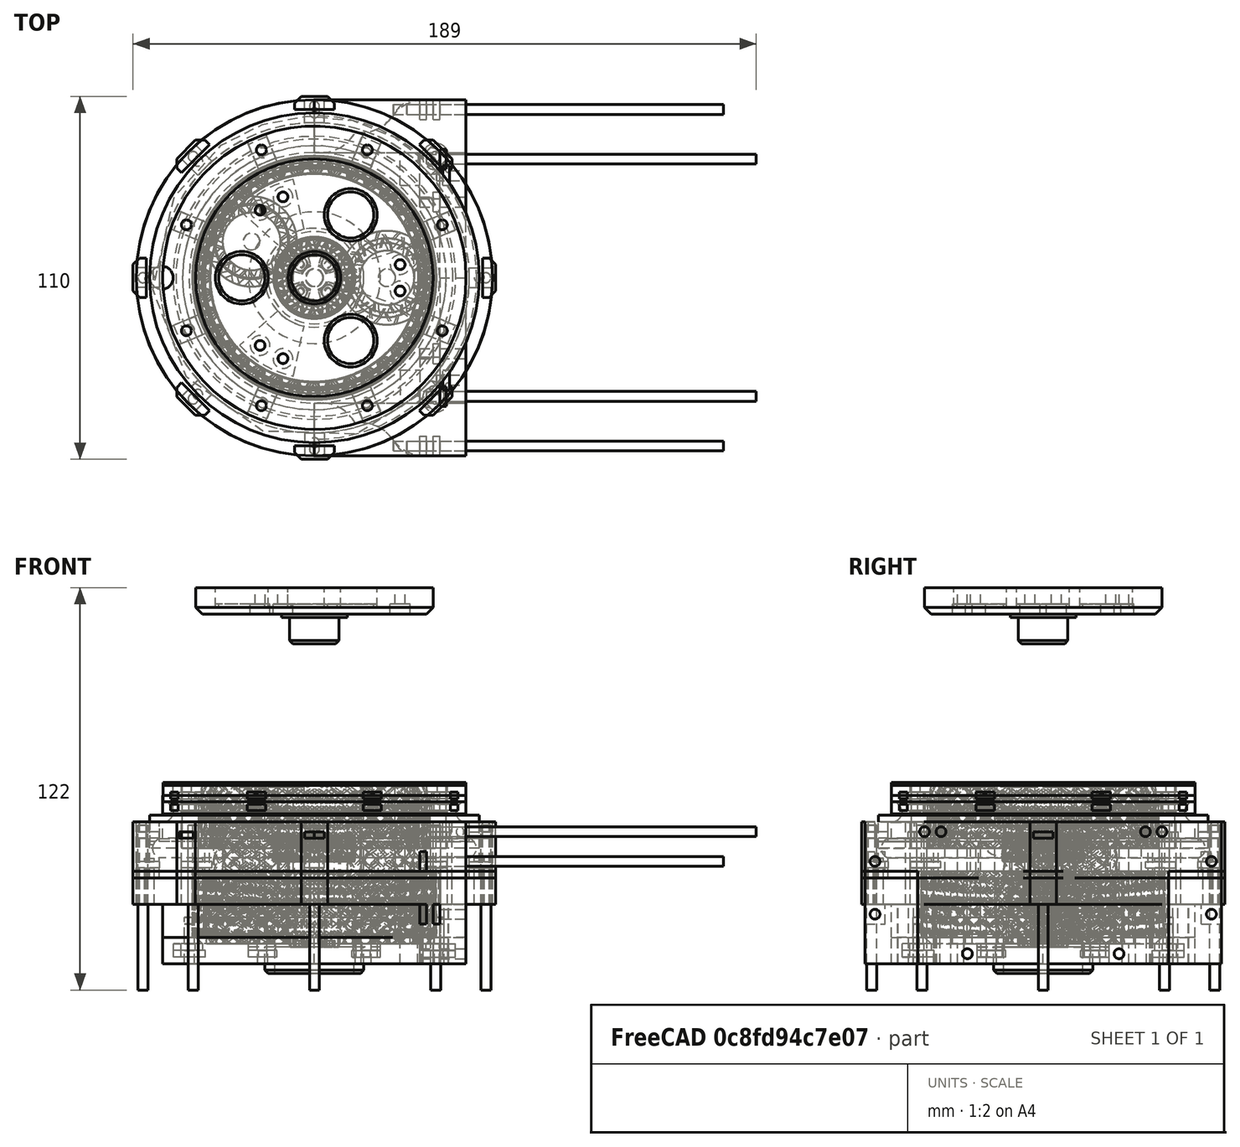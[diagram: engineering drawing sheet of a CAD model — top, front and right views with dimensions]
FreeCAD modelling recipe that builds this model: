
FCSTD DOCUMENT  (FreeCAD 0.19R24276 (Git))
Label: J-midi-thin_039
License: All rights reserved
LicenseURL: http://en.wikipedia.org/wiki/All_rights_reserved
objects: Part::Cylinder×488, Part::Box×269, Part::Compound×195, Part::Cut×182, Part::FeaturePython×78, Part::Chamfer×34, Part::Wedge×24, Part::Fillet×4, Part::Torus×3, Part::Mirroring×3, Mesh::Feature×1
note: 1280 computed .brp shape members not serialized (recipe doc carries the construction recipe); baked Part::Feature solids carry a one-line shape summary decoded from their .brp

FEATURE [Part::Torus] Torus004  label="Anuloid004"
  Angle1 = -180
  Angle2 = 180
  Angle3 = 360
  AttacherType = Attacher::AttachEngine3D
  Placement = pos=(0,0,29) rot=(0,0,1;0rad)
  Radius1 = 46
  Radius2 = 3.1
FEATURE [Part::Torus] Torus005  label="Anuloid005"
  Angle1 = -180
  Angle2 = 180
  Angle3 = 360
  AttacherType = Attacher::AttachEngine3D
  Placement = pos=(0,0,29) rot=(0,0,1;0rad)
  Radius1 = 46
  Radius2 = 3.1
FEATURE [Part::FeaturePython] Tube002  # WARN: FeaturePython — macro-defined, semantics opaque (R4)
  AttacherType = Attacher::AttachEngine3D
  Height = 17
  InnerRadius = 47
  OuterRadius = 54
  Placement = pos=(0,0,20) rot=(0,0,1;0rad)
FEATURE [Part::Cut] Cut009
  Base = -> Tube002
  Tool = -> Torus004
FEATURE [Part::Cylinder] Cylinder006  label="Válec006"
  Angle = 360
  AttacherType = Attacher::AttachEngine3D
  Height = 10
  Placement = pos=(-46.3,0,30) rot=(0,0,1;0rad)
  Radius = 3.5
FEATURE [Part::Cut] Cut010
  Base = -> Cut009
  Tool = -> Cylinder006
FEATURE [Part::Box] Box156  label="Krychle156"
  AttacherType = Attacher::AttachEngine3D
  Height = 17
  Length = 46
  Placement = pos=(0,-54,20) rot=(0,0,1;0rad)
  Width = 108
FEATURE [Part::Box] Box157  label="Krychle157"
  AttacherType = Attacher::AttachEngine3D
  Height = 2
  Length = 8
  Placement = pos=(46,-3,23) rot=(0,0,1;0rad)
  Width = 6
FEATURE [Part::Box] Box158  label="Krychle158"
  AttacherType = Attacher::AttachEngine3D
  Height = 2
  Length = 8
  Placement = pos=(34.6482,30.4056,23) rot=(0,0,1;0.785398rad)
  Width = 6
FEATURE [Part::Box] Box159  label="Krychle159"
  AttacherType = Attacher::AttachEngine3D
  Height = 2
  Length = 8
  Placement = pos=(3,46,23) rot=(0,0,1;1.5708rad)
  Width = 6
FEATURE [Part::Box] Box160  label="Krychle160"
  AttacherType = Attacher::AttachEngine3D
  Height = 2
  Length = 8
  Placement = pos=(-30.4056,34.6482,23) rot=(0,0,1;2.35619rad)
  Width = 6
FEATURE [Part::Box] Box161  label="Krychle161"
  AttacherType = Attacher::AttachEngine3D
  Height = 2
  Length = 8
  Placement = pos=(-46,3,23) rot=(0,0,1;3.14159rad)
  Width = 6
FEATURE [Part::Box] Box162  label="Krychle162"
  AttacherType = Attacher::AttachEngine3D
  Height = 2
  Length = 8
  Placement = pos=(-34.6482,-30.4056,23) rot=(0,0,1;3.92699rad)
  Width = 6
FEATURE [Part::Box] Box163  label="Krychle163"
  AttacherType = Attacher::AttachEngine3D
  Height = 2
  Length = 8
  Placement = pos=(-3,-46,23) rot=(0,0,-1;1.5708rad)
  Width = 6
FEATURE [Part::Box] Box164  label="Krychle164"
  AttacherType = Attacher::AttachEngine3D
  Height = 2
  Length = 8
  Placement = pos=(30.4056,-34.6482,23) rot=(0,0,-1;0.785398rad)
  Width = 6
FEATURE [Part::Compound] Compound297
  Links = -> [Box157,Box158,Box159,Box160,Box161,Box162,Box163,Box164]
FEATURE [Part::Cut] Cut151
  Base = -> Cut010
  Tool = -> Compound297
FEATURE [Part::Cylinder] Cylinder374  label="Válec374"
  Angle = 360
  AttacherType = Attacher::AttachEngine3D
  Height = 50
  Placement = pos=(50,0,-15) rot=(0,0,1;0rad)
  Radius = 1.5
FEATURE [Part::Cylinder] Cylinder375  label="Válec375"
  Angle = 360
  AttacherType = Attacher::AttachEngine3D
  Height = 50
  Placement = pos=(35.3553,35.3553,-15) rot=(0,0,1;0.785398rad)
  Radius = 1.5
FEATURE [Part::Cylinder] Cylinder376  label="Válec376"
  Angle = 360
  AttacherType = Attacher::AttachEngine3D
  Height = 50
  Placement = pos=(-7e-15,50,-15) rot=(0,0,1;1.5708rad)
  Radius = 1.5
FEATURE [Part::Cylinder] Cylinder377  label="Válec377"
  Angle = 360
  AttacherType = Attacher::AttachEngine3D
  Height = 50
  Placement = pos=(-35.3553,35.3553,-15) rot=(0,0,1;2.35619rad)
  Radius = 1.5
FEATURE [Part::Cylinder] Cylinder378  label="Válec378"
  Angle = 360
  AttacherType = Attacher::AttachEngine3D
  Height = 50
  Placement = pos=(-50,-2.3e-14,-15) rot=(0,0,1;3.14159rad)
  Radius = 1.5
FEATURE [Part::Cylinder] Cylinder379  label="Válec379"
  Angle = 360
  AttacherType = Attacher::AttachEngine3D
  Height = 50
  Placement = pos=(-35.3553,-35.3553,-15) rot=(0,0,1;3.92699rad)
  Radius = 1.5
FEATURE [Part::Cylinder] Cylinder380  label="Válec380"
  Angle = 360
  AttacherType = Attacher::AttachEngine3D
  Height = 50
  Placement = pos=(2.5e-14,-50,-15) rot=(0,0,-1;1.5708rad)
  Radius = 1.5
FEATURE [Part::Cylinder] Cylinder381  label="Válec381"
  Angle = 360
  AttacherType = Attacher::AttachEngine3D
  Height = 50
  Placement = pos=(35.3553,-35.3553,-15) rot=(0,0,-1;0.785398rad)
  Radius = 1.5
FEATURE [Part::Compound] Compound298
  Links = -> [Cylinder374,Cylinder375,Cylinder376,Cylinder377,Cylinder378,Cylinder379,Cylinder380,Cylinder381]
  Placement = pos=(0,0,-9) rot=(0,0,1;0rad)
FEATURE [Part::Cut] Cut152
  Base = -> Cut151
  Tool = -> Compound298
FEATURE [Part::Box] Box165  label="Krychle165"
  AttacherType = Attacher::AttachEngine3D
  Height = 2
  Length = 8
  Placement = pos=(3,46,23) rot=(0,0,1;1.5708rad)
  Width = 6
FEATURE [Part::Box] Box166  label="Krychle166"
  AttacherType = Attacher::AttachEngine3D
  Height = 2
  Length = 8
  Placement = pos=(-30.4056,34.6482,23) rot=(0,0,1;2.35619rad)
  Width = 6
FEATURE [Part::Box] Box167  label="Krychle167"
  AttacherType = Attacher::AttachEngine3D
  Height = 2
  Length = 8
  Placement = pos=(46,-3,23) rot=(0,0,1;0rad)
  Width = 6
FEATURE [Part::Box] Box168  label="Krychle168"
  AttacherType = Attacher::AttachEngine3D
  Height = 2
  Length = 8
  Placement = pos=(-46,3,23) rot=(0,0,1;3.14159rad)
  Width = 6
FEATURE [Part::Box] Box169  label="Krychle169"
  AttacherType = Attacher::AttachEngine3D
  Height = 2
  Length = 8
  Placement = pos=(-34.6482,-30.4056,23) rot=(0,0,1;3.92699rad)
  Width = 6
FEATURE [Part::Box] Box170  label="Krychle170"
  AttacherType = Attacher::AttachEngine3D
  Height = 2
  Length = 8
  Placement = pos=(30.4056,-34.6482,23) rot=(0,0,-1;0.785398rad)
  Width = 6
FEATURE [Part::Box] Box171  label="Krychle171"
  AttacherType = Attacher::AttachEngine3D
  Height = 2
  Length = 8
  Placement = pos=(34.6482,30.4056,23) rot=(0,0,1;0.785398rad)
  Width = 6
FEATURE [Part::Box] Box172  label="Krychle172"
  AttacherType = Attacher::AttachEngine3D
  Height = 2
  Length = 8
  Placement = pos=(-3,-46,23) rot=(0,0,-1;1.5708rad)
  Width = 6
FEATURE [Part::Compound] Compound300
  Links = -> [Box167,Box171,Box165,Box166,Box168,Box169,Box172,Box170]
FEATURE [Part::Cylinder] Cylinder  label="Válec"
  Angle = 360
  AttacherType = Attacher::AttachEngine3D
  Height = 17
  Placement = pos=(0,0,20) rot=(0,0,1;0rad)
  Radius = 47
FEATURE [Part::Cut] Cut153
  Base = -> Box156
  Tool = -> Cylinder
FEATURE [Part::Cut] Cut154
  Base = -> Cut153
  Tool = -> Torus005
FEATURE [Part::Box] Box173  label="Krychle173"
  AttacherType = Attacher::AttachEngine3D
  Height = 6
  Length = 2
  Placement = pos=(32,48,22) rot=(0,0,1;0rad)
  Width = 6
FEATURE [Part::Cylinder] Cylinder391  label="Válec391"
  Angle = 360
  AttacherType = Attacher::AttachEngine3D
  Height = 100
  Placement = pos=(24,51,25) rot=(0,1,0;1.5708rad)
  Radius = 1.5
FEATURE [Part::Cylinder] Cylinder392  label="Válec392"
  Angle = 360
  AttacherType = Attacher::AttachEngine3D
  Height = 100
  Placement = pos=(24,-51,25) rot=(0,1,0;1.5708rad)
  Radius = 1.5
FEATURE [Part::Box] Box174  label="Krychle174"
  AttacherType = Attacher::AttachEngine3D
  Height = 6
  Length = 2
  Placement = pos=(32,-54,22) rot=(0,0,1;0rad)
  Width = 6
FEATURE [Part::Box] Box175  label="Krychle175"
  AttacherType = Attacher::AttachEngine3D
  Height = 6
  Length = 2
  Placement = pos=(38,33,31) rot=(0,0,1;0rad)
  Width = 6
FEATURE [Part::Cylinder] Cylinder393  label="Válec393"
  Angle = 360
  AttacherType = Attacher::AttachEngine3D
  Height = 100
  Placement = pos=(34,36,34) rot=(0,1,0;1.5708rad)
  Radius = 1.5
FEATURE [Part::Cylinder] Cylinder394  label="Válec394"
  Angle = 360
  AttacherType = Attacher::AttachEngine3D
  Height = 100
  Placement = pos=(34,-36,34) rot=(0,1,0;1.5708rad)
  Radius = 1.5
FEATURE [Part::Compound] Compound301
  Links = -> [Cylinder391,Cylinder392,Cylinder393,Cylinder394]
FEATURE [Part::Box] Box176  label="Krychle176"
  AttacherType = Attacher::AttachEngine3D
  Height = 6
  Length = 2
  Placement = pos=(38,-39,31) rot=(0,0,1;0rad)
  Width = 6
FEATURE [Part::Compound] Compound302
  Links = -> [Box173,Box174,Box175,Box176]
FEATURE [Part::Cylinder] Cylinder395  label="Válec395"
  Angle = 360
  AttacherType = Attacher::AttachEngine3D
  Height = 100
  Placement = pos=(34,-36,34) rot=(0,1,0;1.5708rad)
  Radius = 1.5
FEATURE [Part::Cylinder] Cylinder396  label="Válec396"
  Angle = 360
  AttacherType = Attacher::AttachEngine3D
  Height = 100
  Placement = pos=(24,51,25) rot=(0,1,0;1.5708rad)
  Radius = 1.5
FEATURE [Part::Cylinder] Cylinder397  label="Válec397"
  Angle = 360
  AttacherType = Attacher::AttachEngine3D
  Height = 100
  Placement = pos=(24,-51,25) rot=(0,1,0;1.5708rad)
  Radius = 1.5
FEATURE [Part::Cylinder] Cylinder398  label="Válec398"
  Angle = 360
  AttacherType = Attacher::AttachEngine3D
  Height = 100
  Placement = pos=(34,36,34) rot=(0,1,0;1.5708rad)
  Radius = 1.5
FEATURE [Part::Compound] Compound303
  Links = -> [Cylinder396,Cylinder397,Cylinder398,Cylinder395]
FEATURE [Part::Box] Box177  label="Krychle177"
  AttacherType = Attacher::AttachEngine3D
  Height = 6
  Length = 2
  Placement = pos=(32,48,22) rot=(0,0,1;0rad)
  Width = 6
FEATURE [Part::Box] Box178  label="Krychle178"
  AttacherType = Attacher::AttachEngine3D
  Height = 6
  Length = 2
  Placement = pos=(32,-54,22) rot=(0,0,1;0rad)
  Width = 6
FEATURE [Part::Box] Box179  label="Krychle179"
  AttacherType = Attacher::AttachEngine3D
  Height = 6
  Length = 2
  Placement = pos=(38,33,31) rot=(0,0,1;0rad)
  Width = 6
FEATURE [Part::Box] Box180  label="Krychle180"
  AttacherType = Attacher::AttachEngine3D
  Height = 6
  Length = 2
  Placement = pos=(38,-39,31) rot=(0,0,1;0rad)
  Width = 6
FEATURE [Part::Compound] Compound304
  Links = -> [Box177,Box178,Box179,Box180]
FEATURE [Part::Cut] Cut155
  Base = -> Cut154
  Tool = -> Compound298
FEATURE [Part::Cut] Cut156
  Base = -> Cut155
  Tool = -> Compound300
FEATURE [Part::Cut] Cut157
  Base = -> Cut156
  Tool = -> Compound301
FEATURE [Part::Cut] Cut158
  Base = -> Cut157
  Tool = -> Compound304
FEATURE [Part::Cut] Cut159
  Base = -> Cut152
  Tool = -> Compound303
FEATURE [Part::Cut] Cut160
  Base = -> Cut159
  Tool = -> Compound302
FEATURE [Part::Compound] Compound305  label="J-midi_bearing-ring"
  Links = -> [Cut158,Cut160]
FEATURE [Part::Box] Box181  label="Krychle181"
  AttacherType = Attacher::AttachEngine3D
  Height = 17
  Length = 46
  Placement = pos=(0,-54,20) rot=(0,0,1;0rad)
  Width = 108
FEATURE [Part::Cylinder] Cylinder399  label="Válec399"
  Angle = 360
  AttacherType = Attacher::AttachEngine3D
  Height = 17
  Placement = pos=(0,0,20) rot=(0,0,1;0rad)
  Radius = 47
FEATURE [Part::Cut] Cut161
  Base = -> Box181
  Tool = -> Cylinder399
FEATURE [Part::Cylinder] Cylinder400  label="Válec400"
  Angle = 360
  AttacherType = Attacher::AttachEngine3D
  Height = 100
  Placement = pos=(24,51,25) rot=(0,1,0;1.5708rad)
  Radius = 1.5
FEATURE [Part::Cylinder] Cylinder401  label="Válec401"
  Angle = 360
  AttacherType = Attacher::AttachEngine3D
  Height = 100
  Placement = pos=(24,-51,25) rot=(0,1,0;1.5708rad)
  Radius = 1.5
FEATURE [Part::Cylinder] Cylinder402  label="Válec402"
  Angle = 360
  AttacherType = Attacher::AttachEngine3D
  Height = 100
  Placement = pos=(34,36,34) rot=(0,1,0;1.5708rad)
  Radius = 1.5
FEATURE [Part::Cylinder] Cylinder403  label="Válec403"
  Angle = 360
  AttacherType = Attacher::AttachEngine3D
  Height = 100
  Placement = pos=(34,-36,34) rot=(0,1,0;1.5708rad)
  Radius = 1.5
FEATURE [Part::Box] Box182  label="Krychle182"
  AttacherType = Attacher::AttachEngine3D
  Height = 6
  Length = 2
  Placement = pos=(32,48,22) rot=(0,0,1;0rad)
  Width = 6
FEATURE [Part::Box] Box183  label="Krychle183"
  AttacherType = Attacher::AttachEngine3D
  Height = 6
  Length = 2
  Placement = pos=(32,-54,22) rot=(0,0,1;0rad)
  Width = 6
FEATURE [Part::Box] Box184  label="Krychle184"
  AttacherType = Attacher::AttachEngine3D
  Height = 6
  Length = 2
  Placement = pos=(38,33,31) rot=(0,0,1;0rad)
  Width = 6
FEATURE [Part::Box] Box185  label="Krychle185"
  AttacherType = Attacher::AttachEngine3D
  Height = 6
  Length = 2
  Placement = pos=(38,-39,31) rot=(0,0,1;0rad)
  Width = 6
FEATURE [Part::Compound] Compound306
  Links = -> [Cylinder400,Cylinder401,Cylinder402,Cylinder403]
FEATURE [Part::Compound] Compound307
  Links = -> [Box182,Box183,Box184,Box185]
FEATURE [Part::FeaturePython] Tube109  label="ZKL-61816-003"  # WARN: FeaturePython — macro-defined, semantics opaque (R4)
  AttacherType = Attacher::AttachEngine3D
  Height = 11
  InnerRadius = 40
  OuterRadius = 50
  Placement = pos=(0,0,20) rot=(0,0,1;0rad)
FEATURE [Part::Cylinder] Cylinder1160  label="Válec1160"
  Angle = 360
  AttacherType = Attacher::AttachEngine3D
  Height = 50
  Placement = pos=(52,0,0) rot=(0,0,1;0rad)
  Radius = 1.5
FEATURE [Part::Cylinder] Cylinder1161  label="Válec1161"
  Angle = 360
  AttacherType = Attacher::AttachEngine3D
  Height = 50
  Placement = pos=(36.7696,36.7696,0) rot=(0,0,1;0.785398rad)
  Radius = 1.5
FEATURE [Part::Cylinder] Cylinder1162  label="Válec1162"
  Angle = 360
  AttacherType = Attacher::AttachEngine3D
  Height = 50
  Placement = pos=(-7e-15,52,0) rot=(0,0,1;1.5708rad)
  Radius = 1.5
FEATURE [Part::Cylinder] Cylinder1163  label="Válec1163"
  Angle = 360
  AttacherType = Attacher::AttachEngine3D
  Height = 50
  Placement = pos=(-36.7696,36.7696,0) rot=(0,0,1;2.35619rad)
  Radius = 1.5
FEATURE [Part::Cylinder] Cylinder1164  label="Válec1164"
  Angle = 360
  AttacherType = Attacher::AttachEngine3D
  Height = 50
  Placement = pos=(-52,-2.1e-14,0) rot=(0,0,1;3.14159rad)
  Radius = 1.5
FEATURE [Part::Cylinder] Cylinder1165  label="Válec1165"
  Angle = 360
  AttacherType = Attacher::AttachEngine3D
  Height = 50
  Placement = pos=(-36.7696,-36.7696,0) rot=(0,0,1;3.92699rad)
  Radius = 1.5
FEATURE [Part::Cylinder] Cylinder1166  label="Válec1166"
  Angle = 360
  AttacherType = Attacher::AttachEngine3D
  Height = 50
  Placement = pos=(2e-14,-52,0) rot=(0,0,-1;1.5708rad)
  Radius = 1.5
FEATURE [Part::Cylinder] Cylinder1167  label="Válec1167"
  Angle = 360
  AttacherType = Attacher::AttachEngine3D
  Height = 50
  Placement = pos=(36.7696,-36.7696,0) rot=(0,0,-1;0.785398rad)
  Radius = 1.5
FEATURE [Part::Compound] Compound879
  Links = -> [Cylinder1160,Cylinder1161,Cylinder1162,Cylinder1163,Cylinder1164,Cylinder1165,Cylinder1166,Cylinder1167]
  Placement = pos=(0,0,-14) rot=(0,0,1;0rad)
FEATURE [Part::Box] Box459  label="Krychle459"
  AttacherType = Attacher::AttachEngine3D
  Height = 2
  Length = 8
  Placement = pos=(47,-3,34) rot=(0,0,1;0rad)
  Width = 6
FEATURE [Part::Box] Box460  label="Krychle460"
  AttacherType = Attacher::AttachEngine3D
  Height = 2
  Length = 8
  Placement = pos=(35.3553,31.1127,34) rot=(0,0,1;0.785398rad)
  Width = 6
FEATURE [Part::Box] Box461  label="Krychle461"
  AttacherType = Attacher::AttachEngine3D
  Height = 2
  Length = 8
  Placement = pos=(3,47,34) rot=(0,0,1;1.5708rad)
  Width = 6
FEATURE [Part::Box] Box462  label="Krychle462"
  AttacherType = Attacher::AttachEngine3D
  Height = 2
  Length = 8
  Placement = pos=(-31.1127,35.3553,34) rot=(0,0,1;2.35619rad)
  Width = 6
FEATURE [Part::Box] Box463  label="Krychle463"
  AttacherType = Attacher::AttachEngine3D
  Height = 2
  Length = 8
  Placement = pos=(-47,3,34) rot=(0,0,1;3.14159rad)
  Width = 6
FEATURE [Part::Box] Box464  label="Krychle464"
  AttacherType = Attacher::AttachEngine3D
  Height = 2
  Length = 8
  Placement = pos=(-35.3553,-31.1127,34) rot=(0,0,1;3.92699rad)
  Width = 6
FEATURE [Part::Box] Box465  label="Krychle465"
  AttacherType = Attacher::AttachEngine3D
  Height = 2
  Length = 8
  Placement = pos=(-3,-47,34) rot=(0,0,-1;1.5708rad)
  Width = 6
FEATURE [Part::Box] Box466  label="Krychle466"
  AttacherType = Attacher::AttachEngine3D
  Height = 2
  Length = 8
  Placement = pos=(31.1127,-35.3553,34) rot=(0,0,-1;0.785398rad)
  Width = 6
FEATURE [Part::Compound] Compound881
  Links = -> [Box459,Box460,Box461,Box462,Box463,Box464,Box465,Box466]
  Placement = pos=(0,0,-2) rot=(0,0,1;0rad)
FEATURE [Part::Box] Box458  label="Krychle458"
  AttacherType = Attacher::AttachEngine3D
  Height = 17
  Length = 4
  Placement = pos=(51,-6,20) rot=(0,0,1;0rad)
  Width = 12
FEATURE [Part::Chamfer] Chamfer001
  Base = -> Box458
  Edges = 2 edges r=2: [Edge5,Edge7]
FEATURE [Part::Chamfer] Chamfer002
  Base = -> Box458
  Edges = 2 edges r=2: [Edge5,Edge7]
  Placement = pos=(0,0,0) rot=(0,0,1;0.785398rad)
FEATURE [Part::Chamfer] Chamfer003
  Base = -> Box458
  Edges = 2 edges r=2: [Edge5,Edge7]
  Placement = pos=(0,0,0) rot=(0,0,1;1.5708rad)
FEATURE [Part::Chamfer] Chamfer004
  Base = -> Box458
  Edges = 2 edges r=2: [Edge5,Edge7]
  Placement = pos=(0,0,0) rot=(0,0,1;2.35619rad)
FEATURE [Part::Chamfer] Chamfer005
  Base = -> Box458
  Edges = 2 edges r=2: [Edge5,Edge7]
  Placement = pos=(0,0,0) rot=(0,0,1;3.14159rad)
FEATURE [Part::Chamfer] Chamfer006
  Base = -> Box458
  Edges = 2 edges r=2: [Edge5,Edge7]
  Placement = pos=(0,0,0) rot=(0,0,1;3.92699rad)
FEATURE [Part::Chamfer] Chamfer007
  Base = -> Box458
  Edges = 2 edges r=2: [Edge5,Edge7]
  Placement = pos=(0,0,0) rot=(0,0,-1;1.5708rad)
FEATURE [Part::Chamfer] Chamfer008
  Base = -> Box458
  Edges = 2 edges r=2: [Edge5,Edge7]
  Placement = pos=(0,0,0) rot=(0,0,-1;0.785398rad)
FEATURE [Part::Compound] Compound878
  Links = -> [Chamfer001,Chamfer002,Chamfer003,Chamfer004,Chamfer005,Chamfer006,Chamfer007,Chamfer008]
FEATURE [Part::Box] Box467  label="Krychle467"
  AttacherType = Attacher::AttachEngine3D
  Height = 2
  Length = 8
  Placement = pos=(47,-3,34) rot=(0,0,1;0rad)
  Width = 6
FEATURE [Part::Box] Box468  label="Krychle468"
  AttacherType = Attacher::AttachEngine3D
  Height = 2
  Length = 8
  Placement = pos=(35.3553,31.1127,34) rot=(0,0,1;0.785398rad)
  Width = 6
FEATURE [Part::Box] Box469  label="Krychle469"
  AttacherType = Attacher::AttachEngine3D
  Height = 2
  Length = 8
  Placement = pos=(3,47,34) rot=(0,0,1;1.5708rad)
  Width = 6
FEATURE [Part::Box] Box470  label="Krychle470"
  AttacherType = Attacher::AttachEngine3D
  Height = 2
  Length = 8
  Placement = pos=(-31.1127,35.3553,34) rot=(0,0,1;2.35619rad)
  Width = 6
FEATURE [Part::Box] Box471  label="Krychle471"
  AttacherType = Attacher::AttachEngine3D
  Height = 2
  Length = 8
  Placement = pos=(-47,3,34) rot=(0,0,1;3.14159rad)
  Width = 6
FEATURE [Part::Box] Box472  label="Krychle472"
  AttacherType = Attacher::AttachEngine3D
  Height = 2
  Length = 8
  Placement = pos=(-35.3553,-31.1127,34) rot=(0,0,1;3.92699rad)
  Width = 6
FEATURE [Part::Box] Box473  label="Krychle473"
  AttacherType = Attacher::AttachEngine3D
  Height = 2
  Length = 8
  Placement = pos=(-3,-47,34) rot=(0,0,-1;1.5708rad)
  Width = 6
FEATURE [Part::Box] Box474  label="Krychle474"
  AttacherType = Attacher::AttachEngine3D
  Height = 2
  Length = 8
  Placement = pos=(31.1127,-35.3553,34) rot=(0,0,-1;0.785398rad)
  Width = 6
FEATURE [Part::Compound] Compound882
  Links = -> [Box467,Box468,Box469,Box470,Box471,Box472,Box473,Box474]
  Placement = pos=(0,0,-2) rot=(0,0,1;0rad)
FEATURE [Part::Cylinder] Cylinder1168  label="Válec1168"
  Angle = 360
  AttacherType = Attacher::AttachEngine3D
  Height = 50
  Placement = pos=(52,0,0) rot=(0,0,1;0rad)
  Radius = 1.5
FEATURE [Part::Cylinder] Cylinder1169  label="Válec1169"
  Angle = 360
  AttacherType = Attacher::AttachEngine3D
  Height = 50
  Placement = pos=(36.7696,36.7696,0) rot=(0,0,1;0.785398rad)
  Radius = 1.5
FEATURE [Part::Cylinder] Cylinder1170  label="Válec1170"
  Angle = 360
  AttacherType = Attacher::AttachEngine3D
  Height = 50
  Placement = pos=(-7e-15,52,0) rot=(0,0,1;1.5708rad)
  Radius = 1.5
FEATURE [Part::Cylinder] Cylinder1171  label="Válec1171"
  Angle = 360
  AttacherType = Attacher::AttachEngine3D
  Height = 50
  Placement = pos=(-36.7696,36.7696,0) rot=(0,0,1;2.35619rad)
  Radius = 1.5
FEATURE [Part::Cylinder] Cylinder1172  label="Válec1172"
  Angle = 360
  AttacherType = Attacher::AttachEngine3D
  Height = 50
  Placement = pos=(-52,-2.1e-14,0) rot=(0,0,1;3.14159rad)
  Radius = 1.5
FEATURE [Part::Cylinder] Cylinder1173  label="Válec1173"
  Angle = 360
  AttacherType = Attacher::AttachEngine3D
  Height = 50
  Placement = pos=(-36.7696,-36.7696,0) rot=(0,0,1;3.92699rad)
  Radius = 1.5
FEATURE [Part::Cylinder] Cylinder1174  label="Válec1174"
  Angle = 360
  AttacherType = Attacher::AttachEngine3D
  Height = 50
  Placement = pos=(2e-14,-52,0) rot=(0,0,-1;1.5708rad)
  Radius = 1.5
FEATURE [Part::Cylinder] Cylinder1175  label="Válec1175"
  Angle = 360
  AttacherType = Attacher::AttachEngine3D
  Height = 50
  Placement = pos=(36.7696,-36.7696,0) rot=(0,0,-1;0.785398rad)
  Radius = 1.5
FEATURE [Part::Compound] Compound883
  Links = -> [Cylinder1168,Cylinder1169,Cylinder1170,Cylinder1171,Cylinder1172,Cylinder1173,Cylinder1174,Cylinder1175]
  Placement = pos=(0,0,-14) rot=(0,0,1;0rad)
FEATURE [Part::FeaturePython] Tube110  label="ZKL-61816-004"  # WARN: FeaturePython — macro-defined, semantics opaque (R4)
  AttacherType = Attacher::AttachEngine3D
  Height = 11
  InnerRadius = 40
  OuterRadius = 50
  Placement = pos=(0,0,20) rot=(0,0,1;0rad)
FEATURE [Part::Cut] Cut
  Base = -> Cut161
  Tool = -> Tube109
FEATURE [Part::Cut] Cut162
  Base = -> Cut
  Tool = -> Compound881
FEATURE [Part::Cylinder] Cylinder714  label="Válec714"
  Angle = 360
  AttacherType = Attacher::AttachEngine3D
  Height = 60
  Placement = pos=(41,0,-54) rot=(0,0,1;0rad)
  Radius = 1.5
FEATURE [Part::Cylinder] Cylinder715  label="Válec715"
  Angle = 360
  AttacherType = Attacher::AttachEngine3D
  Height = 40
  Placement = pos=(202,50,-30) rot=(0,0,1;0rad)
  Radius = 12
FEATURE [Part::Box] Box334  label="Krychle334"
  AttacherType = Attacher::AttachEngine3D
  Height = 2
  Length = 8
  Placement = pos=(37,-3,-4) rot=(0,0,1;0rad)
  Width = 6
FEATURE [Part::Cylinder] Cylinder716  label="Válec716"
  Angle = 360
  AttacherType = Attacher::AttachEngine3D
  Height = 40
  Placement = pos=(214,56,-30) rot=(0,0,1;0rad)
  Radius = 12
FEATURE [Part::Cylinder] Cylinder717  label="Válec717"
  Angle = 360
  AttacherType = Attacher::AttachEngine3D
  Height = 10
  Radius = 46
FEATURE [Part::Box] Box335  label="Krychle335"
  AttacherType = Attacher::AttachEngine3D
  Height = 28
  Length = 6
  Placement = pos=(26,28,-8) rot=(0,0,1;0rad)
  Width = 10
FEATURE [Part::Cylinder] Cylinder718  label="Válec718"
  Angle = 360
  AttacherType = Attacher::AttachEngine3D
  Height = 40
  Placement = pos=(256,0,-30) rot=(0,0,1;0rad)
  Radius = 10
FEATURE [Part::Box] Box336  label="Krychle336"
  AttacherType = Attacher::AttachEngine3D
  Height = 28
  Length = 8
  Placement = pos=(238,0,-8) rot=(0,0,1;0rad)
  Width = 38
FEATURE [Part::Cylinder] Cylinder719  label="Válec719"
  Angle = 360
  AttacherType = Attacher::AttachEngine3D
  Height = 10
  Radius = 54
FEATURE [Part::Box] Box337  label="Krychle337"
  AttacherType = Attacher::AttachEngine3D
  Height = 28
  Length = 6
  Placement = pos=(32,24,-8) rot=(0,0,1;0rad)
  Width = 14
FEATURE [Part::Cylinder] Cylinder720  label="Válec720"
  Angle = 360
  AttacherType = Attacher::AttachEngine3D
  Height = 40
  Placement = pos=(202,50,-30) rot=(0,0,1;0rad)
  Radius = 12
FEATURE [Part::Box] Box338  label="Krychle338"
  AttacherType = Attacher::AttachEngine3D
  Height = 28
  Length = 8
  Placement = pos=(238,0,-8) rot=(0,0,1;0rad)
  Width = 38
FEATURE [Part::Box] Box339  label="Krychle339"
  AttacherType = Attacher::AttachEngine3D
  Height = 2
  Length = 8
  Placement = pos=(28.2843,24.0416,-4) rot=(0,0,1;0.785398rad)
  Width = 6
FEATURE [Part::Box] Box340  label="Krychle340"
  AttacherType = Attacher::AttachEngine3D
  Height = 2
  Length = 8
  Placement = pos=(-28.2843,-24.0416,-4) rot=(0,0,1;3.92699rad)
  Width = 6
FEATURE [Part::Cylinder] Cylinder721  label="Válec721"
  Angle = 360
  AttacherType = Attacher::AttachEngine3D
  Height = 40
  Placement = pos=(214,56,-30) rot=(0,0,1;0rad)
  Radius = 12
FEATURE [Part::Box] Box341  label="Krychle341"
  AttacherType = Attacher::AttachEngine3D
  Height = 28
  Length = 6
  Placement = pos=(26,28,-8) rot=(0,0,1;0rad)
  Width = 10
FEATURE [Part::Compound] Compound705
  Links = -> [Box341,Box337]
FEATURE [Part::Box] Box342  label="Krychle342"
  AttacherType = Attacher::AttachEngine3D
  Height = 28
  Length = 46
  Placement = pos=(200,38,-8) rot=(0,0,1;0rad)
  Width = 16
FEATURE [Part::Compound] Compound709
  Links = -> [Box336,Box342]
FEATURE [Part::Box] Box343  label="Krychle343"
  AttacherType = Attacher::AttachEngine3D
  Height = 28
  Length = 6
  Placement = pos=(32,24,-8) rot=(0,0,1;0rad)
  Width = 14
FEATURE [Part::Box] Box344  label="Krychle344"
  AttacherType = Attacher::AttachEngine3D
  Height = 2
  Length = 8
  Placement = pos=(3,37,-4) rot=(0,0,1;1.5708rad)
  Width = 6
FEATURE [Part::Cylinder] Cylinder722  label="Válec722"
  Angle = 360
  AttacherType = Attacher::AttachEngine3D
  Height = 40
  Placement = pos=(256,0,-30) rot=(0,0,1;0rad)
  Radius = 10
FEATURE [Part::Compound] Compound711
  Links = -> [Cylinder722,Cylinder721]
FEATURE [Part::Cylinder] Cylinder723  label="Válec723"
  Angle = 360
  AttacherType = Attacher::AttachEngine3D
  Height = 60
  Placement = pos=(28.9914,28.9914,-54) rot=(0,0,1;0.785398rad)
  Radius = 1.5
FEATURE [Part::Box] Box345  label="Krychle345"
  AttacherType = Attacher::AttachEngine3D
  Height = 28
  Length = 46
  Placement = pos=(200,38,-8) rot=(0,0,1;0rad)
  Width = 16
FEATURE [Part::Compound] Compound706
  Links = -> [Box338,Box345]
FEATURE [Part::Cut] Cut337
  Base = -> Compound706
  Tool = -> Compound711
FEATURE [Part::Box] Box346  label="Krychle346"
  AttacherType = Attacher::AttachEngine3D
  Height = 2
  Length = 8
  Placement = pos=(24.0416,-28.2843,-4) rot=(0,0,-1;0.785398rad)
  Width = 6
FEATURE [Part::Cylinder] Cylinder724  label="Válec724"
  Angle = 360
  AttacherType = Attacher::AttachEngine3D
  Height = 60
  Placement = pos=(28.9914,-28.9914,-54) rot=(0,0,-1;0.785398rad)
  Radius = 1.5
FEATURE [Part::Box] Box347  label="Krychle347"
  AttacherType = Attacher::AttachEngine3D
  Height = 2
  Length = 8
  Placement = pos=(-3,-37,-4) rot=(0,0,-1;1.5708rad)
  Width = 6
FEATURE [Part::Cylinder] Cylinder725  label="Válec725"
  Angle = 360
  AttacherType = Attacher::AttachEngine3D
  Height = 60
  Placement = pos=(-41,-1.1e-14,-54) rot=(0,0,1;3.14159rad)
  Radius = 1.5
FEATURE [Part::Cylinder] Cylinder726  label="Válec726"
  Angle = 360
  AttacherType = Attacher::AttachEngine3D
  Height = 60
  Placement = pos=(1.2e-14,-41,-54) rot=(0,0,-1;1.5708rad)
  Radius = 1.5
FEATURE [Part::Cylinder] Cylinder727  label="Válec727"
  Angle = 360
  AttacherType = Attacher::AttachEngine3D
  Height = 60
  Placement = pos=(-28.9914,-28.9914,-54) rot=(0,0,1;3.92699rad)
  Radius = 1.5
FEATURE [Part::Cylinder] Cylinder728  label="Válec728"
  Angle = 360
  AttacherType = Attacher::AttachEngine3D
  Height = 60
  Placement = pos=(28.9914,-28.9914,-54) rot=(0,0,-1;0.785398rad)
  Radius = 1.5
FEATURE [Part::Box] Box348  label="Krychle348"
  AttacherType = Attacher::AttachEngine3D
  Height = 2
  Length = 8
  Placement = pos=(37,-3,-4) rot=(0,0,1;0rad)
  Width = 6
FEATURE [Part::Cylinder] Cylinder729  label="Válec729"
  Angle = 360
  AttacherType = Attacher::AttachEngine3D
  Height = 60
  Placement = pos=(41,0,-54) rot=(0,0,1;0rad)
  Radius = 1.5
FEATURE [Part::Box] Box349  label="Krychle349"
  AttacherType = Attacher::AttachEngine3D
  Height = 2
  Length = 8
  Placement = pos=(-37,3,-4) rot=(0,0,1;3.14159rad)
  Width = 6
FEATURE [Part::Cylinder] Cylinder730  label="Válec730"
  Angle = 360
  AttacherType = Attacher::AttachEngine3D
  Height = 60
  Placement = pos=(1.2e-14,-41,-54) rot=(0,0,-1;1.5708rad)
  Radius = 1.5
FEATURE [Part::Box] Box350  label="Krychle350"
  AttacherType = Attacher::AttachEngine3D
  Height = 2
  Length = 8
  Placement = pos=(28.2843,24.0416,-4) rot=(0,0,1;0.785398rad)
  Width = 6
FEATURE [Part::Box] Box351  label="Krychle351"
  AttacherType = Attacher::AttachEngine3D
  Height = 2
  Length = 8
  Placement = pos=(-28.2843,-24.0416,-4) rot=(0,0,1;3.92699rad)
  Width = 6
FEATURE [Part::Cylinder] Cylinder731  label="Válec731"
  Angle = 360
  AttacherType = Attacher::AttachEngine3D
  Height = 60
  Placement = pos=(-4e-15,41,-54) rot=(0,0,1;1.5708rad)
  Radius = 1.5
FEATURE [Part::Box] Box352  label="Krychle352"
  AttacherType = Attacher::AttachEngine3D
  Height = 2
  Length = 8
  Placement = pos=(-3,-37,-4) rot=(0,0,-1;1.5708rad)
  Width = 6
FEATURE [Part::Box] Box353  label="Krychle353"
  AttacherType = Attacher::AttachEngine3D
  Height = 2
  Length = 8
  Placement = pos=(-24.0416,28.2843,-4) rot=(0,0,1;2.35619rad)
  Width = 6
FEATURE [Part::Cylinder] Cylinder732  label="Válec732"
  Angle = 360
  AttacherType = Attacher::AttachEngine3D
  Height = 60
  Placement = pos=(-28.9914,28.9914,-54) rot=(0,0,1;2.35619rad)
  Radius = 1.5
FEATURE [Part::Cylinder] Cylinder733  label="Válec733"
  Angle = 360
  AttacherType = Attacher::AttachEngine3D
  Height = 60
  Placement = pos=(28.9914,-28.9914,-54) rot=(0,0,-1;0.785398rad)
  Radius = 1.5
FEATURE [Part::Box] Box354  label="Krychle354"
  AttacherType = Attacher::AttachEngine3D
  Height = 2
  Length = 8
  Placement = pos=(-24.0416,28.2843,-4) rot=(0,0,1;2.35619rad)
  Width = 6
FEATURE [Part::Cylinder] Cylinder734  label="Válec734"
  Angle = 360
  AttacherType = Attacher::AttachEngine3D
  Height = 60
  Placement = pos=(-41,-1.1e-14,-54) rot=(0,0,1;3.14159rad)
  Radius = 1.5
FEATURE [Part::Cylinder] Cylinder735  label="Válec735"
  Angle = 360
  AttacherType = Attacher::AttachEngine3D
  Height = 60
  Placement = pos=(28.9914,28.9914,-54) rot=(0,0,1;0.785398rad)
  Radius = 1.5
FEATURE [Part::Box] Box355  label="Krychle355"
  AttacherType = Attacher::AttachEngine3D
  Height = 2
  Length = 8
  Placement = pos=(24.0416,-28.2843,-4) rot=(0,0,-1;0.785398rad)
  Width = 6
FEATURE [Part::Cylinder] Cylinder736  label="Válec736"
  Angle = 360
  AttacherType = Attacher::AttachEngine3D
  Height = 60
  Placement = pos=(-28.9914,28.9914,-54) rot=(0,0,1;2.35619rad)
  Radius = 1.5
FEATURE [Part::Cylinder] Cylinder737  label="Válec737"
  Angle = 360
  AttacherType = Attacher::AttachEngine3D
  Height = 60
  Placement = pos=(-4e-15,41,-54) rot=(0,0,1;1.5708rad)
  Radius = 1.5
FEATURE [Part::Box] Box356  label="Krychle356"
  AttacherType = Attacher::AttachEngine3D
  Height = 2
  Length = 8
  Placement = pos=(3,37,-4) rot=(0,0,1;1.5708rad)
  Width = 6
FEATURE [Part::Cylinder] Cylinder738  label="Válec738"
  Angle = 360
  AttacherType = Attacher::AttachEngine3D
  Height = 60
  Placement = pos=(-28.9914,-28.9914,-54) rot=(0,0,1;3.92699rad)
  Radius = 1.5
FEATURE [Part::Cylinder] Cylinder739  label="Válec739"
  Angle = 360
  AttacherType = Attacher::AttachEngine3D
  Height = 60
  Placement = pos=(28,-51,7) rot=(0,1,0;1.5708rad)
  Radius = 1.5
FEATURE [Part::Cylinder] Cylinder740  label="Válec740"
  Angle = 360
  AttacherType = Attacher::AttachEngine3D
  Height = 60
  Placement = pos=(-4e-15,41,-54) rot=(0,0,1;1.5708rad)
  Radius = 1.5
FEATURE [Part::Box] Box357  label="Krychle357"
  AttacherType = Attacher::AttachEngine3D
  Height = 2
  Length = 8
  Placement = pos=(-37,3,-4) rot=(0,0,1;3.14159rad)
  Width = 6
FEATURE [Part::Box] Box358  label="Krychle358"
  AttacherType = Attacher::AttachEngine3D
  Height = 6
  Length = 2
  Placement = pos=(36,18,-8) rot=(0,0,1;0rad)
  Width = 6
FEATURE [Part::Box] Box359  label="Krychle359"
  AttacherType = Attacher::AttachEngine3D
  Height = 6
  Length = 2
  Placement = pos=(32,-54,4) rot=(0,0,1;0rad)
  Width = 6
FEATURE [Part::Cylinder] Cylinder741  label="Válec741"
  Angle = 360
  AttacherType = Attacher::AttachEngine3D
  Height = 50
  Placement = pos=(-50,-2.3e-14,-15) rot=(0,0,1;3.14159rad)
  Radius = 1.5
FEATURE [Part::Cylinder] Cylinder742  label="Válec742"
  Angle = 360
  AttacherType = Attacher::AttachEngine3D
  Height = 60
  Placement = pos=(28,51,7) rot=(0,1,0;1.5708rad)
  Radius = 1.5
FEATURE [Part::Box] Box360  label="Krychle360"
  AttacherType = Attacher::AttachEngine3D
  Height = 6
  Length = 2
  Placement = pos=(36,20,-8) rot=(0,0,1;0rad)
  Width = 6
FEATURE [Part::Cylinder] Cylinder743  label="Válec743"
  Angle = 360
  AttacherType = Attacher::AttachEngine3D
  Height = 60
  Placement = pos=(41,0,-54) rot=(0,0,1;0rad)
  Radius = 1.5
FEATURE [Part::Cylinder] Cylinder744  label="Válec744"
  Angle = 360
  AttacherType = Attacher::AttachEngine3D
  Height = 60
  Placement = pos=(-28.9914,-28.9914,-54) rot=(0,0,1;3.92699rad)
  Radius = 1.5
FEATURE [Part::Cylinder] Cylinder745  label="Válec745"
  Angle = 360
  AttacherType = Attacher::AttachEngine3D
  Height = 60
  Placement = pos=(28,-51,7) rot=(0,1,0;1.5708rad)
  Radius = 1.5
FEATURE [Part::Box] Box361  label="Krychle361"
  AttacherType = Attacher::AttachEngine3D
  Height = 6
  Length = 2
  Placement = pos=(32,-54,4) rot=(0,0,1;0rad)
  Width = 6
FEATURE [Part::Cylinder] Cylinder746  label="Válec746"
  Angle = 360
  AttacherType = Attacher::AttachEngine3D
  Height = 60
  Placement = pos=(-28.9914,28.9914,-54) rot=(0,0,1;2.35619rad)
  Radius = 1.5
FEATURE [Part::Cylinder] Cylinder747  label="Válec747"
  Angle = 360
  AttacherType = Attacher::AttachEngine3D
  Height = 60
  Placement = pos=(32,-21,-5) rot=(0,1,0;1.5708rad)
  Radius = 1.5
FEATURE [Part::Box] Box362  label="Krychle362"
  AttacherType = Attacher::AttachEngine3D
  Height = 6
  Length = 2
  Placement = pos=(36,-24,-8) rot=(0,0,1;0rad)
  Width = 6
FEATURE [Part::Cylinder] Cylinder748  label="Válec748"
  Angle = 360
  AttacherType = Attacher::AttachEngine3D
  Height = 60
  Placement = pos=(1.2e-14,-41,-54) rot=(0,0,-1;1.5708rad)
  Radius = 1.5
FEATURE [Part::Box] Box363  label="Krychle363"
  AttacherType = Attacher::AttachEngine3D
  Height = 6
  Length = 2
  Placement = pos=(32,48,4) rot=(0,0,1;0rad)
  Width = 6
FEATURE [Part::Compound] Compound703
  Links = -> [Box358,Box362,Box363,Box359]
FEATURE [Part::Cylinder] Cylinder749  label="Válec749"
  Angle = 360
  AttacherType = Attacher::AttachEngine3D
  Height = 60
  Placement = pos=(28.9914,28.9914,-54) rot=(0,0,1;0.785398rad)
  Radius = 1.5
FEATURE [Part::Cylinder] Cylinder750  label="Válec750"
  Angle = 360
  AttacherType = Attacher::AttachEngine3D
  Height = 60
  Placement = pos=(32,21,-5) rot=(0,1,0;1.5708rad)
  Radius = 1.5
FEATURE [Part::Compound] Compound710
  Links = -> [Cylinder750,Cylinder747,Cylinder742,Cylinder739]
FEATURE [Part::Cylinder] Cylinder751  label="Válec751"
  Angle = 360
  AttacherType = Attacher::AttachEngine3D
  Height = 60
  Placement = pos=(-41,-1.1e-14,-54) rot=(0,0,1;3.14159rad)
  Radius = 1.5
FEATURE [Part::Cylinder] Cylinder752  label="Válec752"
  Angle = 360
  AttacherType = Attacher::AttachEngine3D
  Height = 50
  Placement = pos=(50,0,-15) rot=(0,0,1;0rad)
  Radius = 1.5
FEATURE [Part::Box] Box364  label="Krychle364"
  AttacherType = Attacher::AttachEngine3D
  Height = 6
  Length = 2
  Placement = pos=(32,48,4) rot=(0,0,1;0rad)
  Width = 6
FEATURE [Part::Box] Box365  label="Krychle365"
  AttacherType = Attacher::AttachEngine3D
  Height = 6
  Length = 2
  Placement = pos=(36,-26,-8) rot=(0,0,1;0rad)
  Width = 6
FEATURE [Part::Cylinder] Cylinder753  label="Válec753"
  Angle = 360
  AttacherType = Attacher::AttachEngine3D
  Height = 60
  Placement = pos=(32,23,-5) rot=(0,1,0;1.5708rad)
  Radius = 1.5
FEATURE [Part::Cylinder] Cylinder754  label="Válec754"
  Angle = 360
  AttacherType = Attacher::AttachEngine3D
  Height = 50
  Placement = pos=(2.5e-14,-50,-15) rot=(0,0,-1;1.5708rad)
  Radius = 1.5
FEATURE [Part::Cylinder] Cylinder755  label="Válec755"
  Angle = 360
  AttacherType = Attacher::AttachEngine3D
  Height = 50
  Placement = pos=(-35.3553,-35.3553,-15) rot=(0,0,1;3.92699rad)
  Radius = 1.5
FEATURE [Part::Cylinder] Cylinder756  label="Válec756"
  Angle = 360
  AttacherType = Attacher::AttachEngine3D
  Height = 50
  Placement = pos=(35.3553,-35.3553,-15) rot=(0,0,-1;0.785398rad)
  Radius = 1.5
FEATURE [Part::Cylinder] Cylinder757  label="Válec757"
  Angle = 360
  AttacherType = Attacher::AttachEngine3D
  Height = 60
  Placement = pos=(28,51,7) rot=(0,1,0;1.5708rad)
  Radius = 1.5
FEATURE [Part::Cylinder] Cylinder758  label="Válec758"
  Angle = 360
  AttacherType = Attacher::AttachEngine3D
  Height = 50
  Placement = pos=(-35.3553,35.3553,-15) rot=(0,0,1;2.35619rad)
  Radius = 1.5
FEATURE [Part::Cylinder] Cylinder759  label="Válec759"
  Angle = 360
  AttacherType = Attacher::AttachEngine3D
  Height = 50
  Placement = pos=(35.3553,35.3553,-15) rot=(0,0,1;0.785398rad)
  Radius = 1.5
FEATURE [Part::Cylinder] Cylinder760  label="Válec760"
  Angle = 360
  AttacherType = Attacher::AttachEngine3D
  Height = 60
  Placement = pos=(32,-23,-5) rot=(0,1,0;1.5708rad)
  Radius = 1.5
FEATURE [Part::Cylinder] Cylinder761  label="Válec761"
  Angle = 360
  AttacherType = Attacher::AttachEngine3D
  Height = 50
  Placement = pos=(50,0,-15) rot=(0,0,1;0rad)
  Radius = 1.5
FEATURE [Part::Box] Box366  label="Krychle366"
  AttacherType = Attacher::AttachEngine3D
  Height = 6
  Length = 2
  Placement = pos=(36,20,-8) rot=(0,0,1;0rad)
  Width = 6
FEATURE [Part::Cylinder] Cylinder762  label="Válec762"
  Angle = 360
  AttacherType = Attacher::AttachEngine3D
  Height = 50
  Placement = pos=(-50,-2.3e-14,-15) rot=(0,0,1;3.14159rad)
  Radius = 1.5
FEATURE [Part::Cylinder] Cylinder763  label="Válec763"
  Angle = 360
  AttacherType = Attacher::AttachEngine3D
  Height = 50
  Placement = pos=(-35.3553,-35.3553,-15) rot=(0,0,1;3.92699rad)
  Radius = 1.5
FEATURE [Part::Cylinder] Cylinder764  label="Válec764"
  Angle = 360
  AttacherType = Attacher::AttachEngine3D
  Height = 50
  Placement = pos=(-7e-15,50,-15) rot=(0,0,1;1.5708rad)
  Radius = 1.5
FEATURE [Part::Cylinder] Cylinder765  label="Válec765"
  Angle = 360
  AttacherType = Attacher::AttachEngine3D
  Height = 50
  Placement = pos=(35.3553,-35.3553,-15) rot=(0,0,-1;0.785398rad)
  Radius = 1.5
FEATURE [Part::Box] Box367  label="Krychle367"
  AttacherType = Attacher::AttachEngine3D
  Height = 6
  Length = 2
  Placement = pos=(36,-26,-8) rot=(0,0,1;0rad)
  Width = 6
FEATURE [Part::Box] Box368  label="Krychle368"
  AttacherType = Attacher::AttachEngine3D
  Height = 6
  Length = 2
  Placement = pos=(32,48,4) rot=(0,0,1;0rad)
  Width = 6
FEATURE [Part::Cylinder] Cylinder766  label="Válec766"
  Angle = 360
  AttacherType = Attacher::AttachEngine3D
  Height = 50
  Placement = pos=(-35.3553,35.3553,-15) rot=(0,0,1;2.35619rad)
  Radius = 1.5
FEATURE [Part::Cylinder] Cylinder767  label="Válec767"
  Angle = 360
  AttacherType = Attacher::AttachEngine3D
  Height = 50
  Placement = pos=(-7e-15,50,-15) rot=(0,0,1;1.5708rad)
  Radius = 1.5
FEATURE [Part::Cylinder] Cylinder768  label="Válec768"
  Angle = 360
  AttacherType = Attacher::AttachEngine3D
  Height = 50
  Placement = pos=(35.3553,35.3553,-15) rot=(0,0,1;0.785398rad)
  Radius = 1.5
FEATURE [Part::Cylinder] Cylinder769  label="Válec769"
  Angle = 360
  AttacherType = Attacher::AttachEngine3D
  Height = 60
  Placement = pos=(28,51,7) rot=(0,1,0;1.5708rad)
  Radius = 1.5
FEATURE [Part::Compound] Compound704
  Links = -> [Cylinder753,Cylinder760,Cylinder769,Cylinder745]
FEATURE [Part::Cylinder] Cylinder770  label="Válec770"
  Angle = 360
  AttacherType = Attacher::AttachEngine3D
  Height = 60
  Placement = pos=(32,-23,-5) rot=(0,1,0;1.5708rad)
  Radius = 1.5
FEATURE [Part::Cylinder] Cylinder771  label="Válec771"
  Angle = 360
  AttacherType = Attacher::AttachEngine3D
  Height = 50
  Placement = pos=(2.5e-14,-50,-15) rot=(0,0,-1;1.5708rad)
  Radius = 1.5
FEATURE [Part::Box] Box369  label="Krychle369"
  AttacherType = Attacher::AttachEngine3D
  Height = 6
  Length = 2
  Placement = pos=(32,-54,4) rot=(0,0,1;0rad)
  Width = 6
FEATURE [Part::Cylinder] Cylinder772  label="Válec772"
  Angle = 360
  AttacherType = Attacher::AttachEngine3D
  Height = 60
  Placement = pos=(28,-51,7) rot=(0,1,0;1.5708rad)
  Radius = 1.5
FEATURE [Part::Cylinder] Cylinder773  label="Válec773"
  Angle = 360
  AttacherType = Attacher::AttachEngine3D
  Height = 50
  Placement = pos=(35.36,35.36,-40) rot=(0,0,1;0.785398rad)
  Radius = 4
FEATURE [Part::Cylinder] Cylinder774  label="Válec774"
  Angle = 360
  AttacherType = Attacher::AttachEngine3D
  Height = 60
  Placement = pos=(32,23,-5) rot=(0,1,0;1.5708rad)
  Radius = 1.5
FEATURE [Part::Cylinder] Cylinder775  label="Válec775"
  Angle = 360
  AttacherType = Attacher::AttachEngine3D
  Height = 50
  Placement = pos=(35.36,-35.36,-40) rot=(0,0,1;0.785398rad)
  Radius = 4
FEATURE [Part::Compound] Compound712
  Links = -> [Box335,Box343]
FEATURE [Part::Compound] Compound713
  Links = -> [Cylinder718,Cylinder716]
FEATURE [Part::Compound] Compound715
  Links = -> [Cylinder774,Cylinder770,Cylinder757,Cylinder772]
FEATURE [Part::Compound] Compound716
  Links = -> [Box350,Box356,Box354,Box357,Box351,Box352,Box355,Box348]
  Placement = pos=(0,0,0) rot=(0,0,1;0.392699rad)
FEATURE [Part::Compound] Compound717
  Links = -> [Cylinder749,Cylinder740,Cylinder746,Cylinder751,Cylinder744,Cylinder748,Cylinder733,Cylinder743]
  Placement = pos=(0,0,0) rot=(0,0,1;0.392699rad)
FEATURE [Part::Compound] Compound719
  Links = -> [Box339,Box344,Box353,Box349,Box340,Box347,Box346,Box334]
  Placement = pos=(0,0,0) rot=(0,0,1;0.392699rad)
FEATURE [Part::Compound] Compound721
  Links = -> [Cylinder773,Cylinder775]
FEATURE [Part::Compound] Compound722
  Links = -> [Cylinder761,Cylinder768,Cylinder764,Cylinder758,Cylinder762,Cylinder763,Cylinder771,Cylinder765]
FEATURE [Part::Compound] Compound723
  Links = -> [Cylinder752,Cylinder759,Cylinder767,Cylinder766,Cylinder741,Cylinder755,Cylinder754,Cylinder756]
FEATURE [Part::Compound] Compound724
  Links = -> [Box366,Box367,Box368,Box369]
FEATURE [Part::Compound] Compound725
  Links = -> [Box360,Box365,Box364,Box361]
FEATURE [Part::Compound] Compound726
  Links = -> [Cylinder735,Cylinder737,Cylinder732,Cylinder734,Cylinder738,Cylinder730,Cylinder724,Cylinder729]
  Placement = pos=(0,0,0) rot=(0,0,1;0.392699rad)
FEATURE [Part::Compound] Compound727
  Links = -> [Cylinder723,Cylinder731,Cylinder736,Cylinder725,Cylinder727,Cylinder726,Cylinder728,Cylinder714]
  Placement = pos=(0,0,0) rot=(0,0,1;0.392699rad)
FEATURE [Part::FeaturePython] wormgear040  # WARN: FeaturePython — macro-defined, semantics opaque (R4)
  AttacherType = Attacher::AttachEngine3D
  Placement = pos=(0,0,0) rot=(0,0,-1;0.090757rad)
  beta = 39.8457
  clearance = 0.25
  diameter = 70.1
  head = 0
  height = 20
  module = 1.5
  pressure_angle = 20
  reverse_pitch = true
  teeth = 39
  version = 0.0.3
FEATURE [Part::Cut] Cut339
  Base = -> Cylinder719
  Placement = pos=(0,0,10) rot=(0,0,1;0.034907rad)
  Tool = -> wormgear040
FEATURE [Part::FeaturePython] wormgear041  # WARN: FeaturePython — macro-defined, semantics opaque (R4)
  AttacherType = Attacher::AttachEngine3D
  beta = 39.8457
  clearance = 0.25
  diameter = 70.1
  head = 0
  height = 20
  module = 1.5
  pressure_angle = 20
  reverse_pitch = false
  teeth = 39
  version = 0.0.3
FEATURE [Part::Cut] Cut338
  Base = -> Cylinder717
  Tool = -> wormgear041
FEATURE [Part::Compound] Compound707
  Links = -> [Cut339,Cut338]
FEATURE [Part::Cut] Cut335
  Base = -> Compound707
  Tool = -> Compound717
FEATURE [Part::Cut] Cut333
  Base = -> Cut335
  Tool = -> Compound710
FEATURE [Part::FeaturePython] Tube077  # WARN: FeaturePython — macro-defined, semantics opaque (R4)
  AttacherType = Attacher::AttachEngine3D
  Height = 8
  InnerRadius = 38
  OuterRadius = 46
  Placement = pos=(0,0,-8) rot=(0,0,1;0rad)
FEATURE [Part::Cut] Cut340
  Base = -> Compound709
  Tool = -> Compound713
FEATURE [Part::Cut] Cut331
  Base = -> Cut340
  Placement = pos=(-200,0,0) rot=(0,0,1;0rad)
  Tool = -> Cylinder720
FEATURE [Part::Compound] Compound708
  Links = -> [Cut331,Compound705]
FEATURE [Part::Cut] Cut341
  Base = -> Tube077
  Tool = -> Compound727
FEATURE [Part::Cut] Cut344
  Base = -> Cut333
  Tool = -> Compound703
FEATURE [Part::Cut] Cut332
  Base = -> Cut344
  Tool = -> Compound723
FEATURE [Part::Cut] Cut345
  Base = -> Cut337
  Placement = pos=(-200,0,0) rot=(0,0,1;0rad)
  Tool = -> Cylinder715
FEATURE [Part::Compound] Compound714
  Links = -> [Cut345,Compound712]
FEATURE [Part::Mirroring] mirror012  label="Compound196 (mirrored)001"
  Base = (0,0,0)
  Normal = (1e-16,-1,0)
  Source = -> Compound714
FEATURE [Part::Compound] Compound720
  Links = -> [mirror012,Compound708]
FEATURE [Part::Cut] Cut342
  Base = -> Compound720
  Tool = -> Compound716
FEATURE [Part::Cut] Cut336
  Base = -> Cut342
  Tool = -> Compound726
FEATURE [Part::Cut] Cut346
  Base = -> Cut336
  Tool = -> Compound722
FEATURE [Part::Cut] Cut334
  Base = -> Cut346
  Tool = -> Compound724
FEATURE [Part::Cut] Cut343
  Base = -> Cut334
  Tool = -> Compound715
FEATURE [Part::Cut] Cut347
  Base = -> Cut343
  Tool = -> Compound721
FEATURE [Part::Fillet] Fillet022
  Base = -> Cut347
  Edges = 1 edges r=8: [Edge273]
FEATURE [Part::Fillet] Fillet021
  Base = -> Fillet022
  Edges = 1 edges r=8: [Edge173]
FEATURE [Part::Cut] Cut350
  Base = -> Cut341
  Tool = -> Compound719
FEATURE [Part::Cut] Cut349
  Base = -> Cut350
  Tool = -> Compound725
FEATURE [Part::Cut] Cut348
  Base = -> Cut349
  Tool = -> Compound704
FEATURE [Part::Compound] Compound718  label="J-midi_monoblok-m1.5"
  Links = -> [Cut332,Cut348,Fillet021]
  Placement = pos=(0,0,2) rot=(0,0,1;0rad)
FEATURE [Part::Cut] Cut351
  Base = -> Compound878
  Tool = -> Compound879
FEATURE [Part::Cylinder] Cylinder1176  label="Válec1176"
  Angle = 360
  AttacherType = Attacher::AttachEngine3D
  Height = 50
  Placement = pos=(52,0,0) rot=(0,0,1;0rad)
  Radius = 1.5
FEATURE [Part::Cylinder] Cylinder1177  label="Válec1177"
  Angle = 360
  AttacherType = Attacher::AttachEngine3D
  Height = 50
  Placement = pos=(36.7696,36.7696,0) rot=(0,0,1;0.785398rad)
  Radius = 1.5
FEATURE [Part::Cylinder] Cylinder1178  label="Válec1178"
  Angle = 360
  AttacherType = Attacher::AttachEngine3D
  Height = 50
  Placement = pos=(-7e-15,52,0) rot=(0,0,1;1.5708rad)
  Radius = 1.5
FEATURE [Part::Cylinder] Cylinder1179  label="Válec1179"
  Angle = 360
  AttacherType = Attacher::AttachEngine3D
  Height = 50
  Placement = pos=(-36.7696,36.7696,0) rot=(0,0,1;2.35619rad)
  Radius = 1.5
FEATURE [Part::Cylinder] Cylinder1180  label="Válec1180"
  Angle = 360
  AttacherType = Attacher::AttachEngine3D
  Height = 50
  Placement = pos=(-52,-2.1e-14,0) rot=(0,0,1;3.14159rad)
  Radius = 1.5
FEATURE [Part::Cylinder] Cylinder1181  label="Válec1181"
  Angle = 360
  AttacherType = Attacher::AttachEngine3D
  Height = 50
  Placement = pos=(-36.7696,-36.7696,0) rot=(0,0,1;3.92699rad)
  Radius = 1.5
FEATURE [Part::Cylinder] Cylinder1182  label="Válec1182"
  Angle = 360
  AttacherType = Attacher::AttachEngine3D
  Height = 50
  Placement = pos=(2e-14,-52,0) rot=(0,0,-1;1.5708rad)
  Radius = 1.5
FEATURE [Part::Cylinder] Cylinder1183  label="Válec1183"
  Angle = 360
  AttacherType = Attacher::AttachEngine3D
  Height = 50
  Placement = pos=(36.7696,-36.7696,0) rot=(0,0,-1;0.785398rad)
  Radius = 1.5
FEATURE [Part::Compound] Compound884
  Links = -> [Cylinder1176,Cylinder1177,Cylinder1178,Cylinder1179,Cylinder1180,Cylinder1181,Cylinder1182,Cylinder1183]
  Placement = pos=(0,0,-14) rot=(0,0,1;0rad)
FEATURE [Part::Cut] Cut352
  Base = -> Cut162
  Tool = -> Compound884
FEATURE [Part::Cut] Cut353
  Base = -> Cut351
  Tool = -> Compound882
FEATURE [Part::FeaturePython] Tube107  # WARN: FeaturePython — macro-defined, semantics opaque (R4)
  AttacherType = Attacher::AttachEngine3D
  Height = 17
  InnerRadius = 47
  OuterRadius = 54
  Placement = pos=(0,0,20) rot=(0,0,1;0rad)
FEATURE [Part::Cut] Cut354
  Base = -> Tube107
  Tool = -> Tube110
FEATURE [Part::Cylinder] Cylinder1184  label="Válec1184"
  Angle = 360
  AttacherType = Attacher::AttachEngine3D
  Height = 50
  Placement = pos=(52,0,0) rot=(0,0,1;0rad)
  Radius = 1.5
FEATURE [Part::Cylinder] Cylinder1185  label="Válec1185"
  Angle = 360
  AttacherType = Attacher::AttachEngine3D
  Height = 50
  Placement = pos=(36.7696,36.7696,0) rot=(0,0,1;0.785398rad)
  Radius = 1.5
FEATURE [Part::Cylinder] Cylinder1186  label="Válec1186"
  Angle = 360
  AttacherType = Attacher::AttachEngine3D
  Height = 50
  Placement = pos=(-7e-15,52,0) rot=(0,0,1;1.5708rad)
  Radius = 1.5
FEATURE [Part::Cylinder] Cylinder1187  label="Válec1187"
  Angle = 360
  AttacherType = Attacher::AttachEngine3D
  Height = 50
  Placement = pos=(-36.7696,36.7696,0) rot=(0,0,1;2.35619rad)
  Radius = 1.5
FEATURE [Part::Cylinder] Cylinder1188  label="Válec1188"
  Angle = 360
  AttacherType = Attacher::AttachEngine3D
  Height = 50
  Placement = pos=(-52,-2.1e-14,0) rot=(0,0,1;3.14159rad)
  Radius = 1.5
FEATURE [Part::Cylinder] Cylinder1189  label="Válec1189"
  Angle = 360
  AttacherType = Attacher::AttachEngine3D
  Height = 50
  Placement = pos=(-36.7696,-36.7696,0) rot=(0,0,1;3.92699rad)
  Radius = 1.5
FEATURE [Part::Cylinder] Cylinder1190  label="Válec1190"
  Angle = 360
  AttacherType = Attacher::AttachEngine3D
  Height = 50
  Placement = pos=(2e-14,-52,0) rot=(0,0,-1;1.5708rad)
  Radius = 1.5
FEATURE [Part::Cylinder] Cylinder1191  label="Válec1191"
  Angle = 360
  AttacherType = Attacher::AttachEngine3D
  Height = 50
  Placement = pos=(36.7696,-36.7696,0) rot=(0,0,-1;0.785398rad)
  Radius = 1.5
FEATURE [Part::Compound] Compound885
  Links = -> [Cylinder1184,Cylinder1185,Cylinder1186,Cylinder1187,Cylinder1188,Cylinder1189,Cylinder1190,Cylinder1191]
  Placement = pos=(0,0,-14) rot=(0,0,1;0rad)
FEATURE [Part::Box] Box475  label="Krychle475"
  AttacherType = Attacher::AttachEngine3D
  Height = 2
  Length = 8
  Placement = pos=(47,-3,34) rot=(0,0,1;0rad)
  Width = 6
FEATURE [Part::Box] Box476  label="Krychle476"
  AttacherType = Attacher::AttachEngine3D
  Height = 2
  Length = 8
  Placement = pos=(35.3553,31.1127,34) rot=(0,0,1;0.785398rad)
  Width = 6
FEATURE [Part::Box] Box477  label="Krychle477"
  AttacherType = Attacher::AttachEngine3D
  Height = 2
  Length = 8
  Placement = pos=(3,47,34) rot=(0,0,1;1.5708rad)
  Width = 6
FEATURE [Part::Box] Box478  label="Krychle478"
  AttacherType = Attacher::AttachEngine3D
  Height = 2
  Length = 8
  Placement = pos=(-31.1127,35.3553,34) rot=(0,0,1;2.35619rad)
  Width = 6
FEATURE [Part::Box] Box479  label="Krychle479"
  AttacherType = Attacher::AttachEngine3D
  Height = 2
  Length = 8
  Placement = pos=(-47,3,34) rot=(0,0,1;3.14159rad)
  Width = 6
FEATURE [Part::Box] Box480  label="Krychle480"
  AttacherType = Attacher::AttachEngine3D
  Height = 2
  Length = 8
  Placement = pos=(-35.3553,-31.1127,34) rot=(0,0,1;3.92699rad)
  Width = 6
FEATURE [Part::Box] Box481  label="Krychle481"
  AttacherType = Attacher::AttachEngine3D
  Height = 2
  Length = 8
  Placement = pos=(-3,-47,34) rot=(0,0,-1;1.5708rad)
  Width = 6
FEATURE [Part::Box] Box482  label="Krychle482"
  AttacherType = Attacher::AttachEngine3D
  Height = 2
  Length = 8
  Placement = pos=(31.1127,-35.3553,34) rot=(0,0,-1;0.785398rad)
  Width = 6
FEATURE [Part::Compound] Compound886
  Links = -> [Box475,Box476,Box477,Box478,Box479,Box480,Box481,Box482]
  Placement = pos=(0,0,-2) rot=(0,0,1;0rad)
FEATURE [Part::Cut] Cut355
  Base = -> Cut354
  Tool = -> Compound885
FEATURE [Part::Cut] Cut356
  Base = -> Cut355
  Tool = -> Compound886
FEATURE [Part::Cylinder] Cylinder1192  label="Válec1192"
  Angle = 360
  AttacherType = Attacher::AttachEngine3D
  Height = 100
  Placement = pos=(24,51,25) rot=(0,1,0;1.5708rad)
  Radius = 1.5
FEATURE [Part::Cylinder] Cylinder1193  label="Válec1193"
  Angle = 360
  AttacherType = Attacher::AttachEngine3D
  Height = 100
  Placement = pos=(24,-51,25) rot=(0,1,0;1.5708rad)
  Radius = 1.5
FEATURE [Part::Cylinder] Cylinder1194  label="Válec1194"
  Angle = 360
  AttacherType = Attacher::AttachEngine3D
  Height = 100
  Placement = pos=(37,31,34) rot=(0,1,0;1.5708rad)
  Radius = 1.5
FEATURE [Part::Cylinder] Cylinder1195  label="Válec1195"
  Angle = 360
  AttacherType = Attacher::AttachEngine3D
  Height = 100
  Placement = pos=(37,-31,34) rot=(0,1,0;1.5708rad)
  Radius = 1.5
FEATURE [Part::Compound] Compound887
  Links = -> [Cylinder1192,Cylinder1193,Cylinder1194,Cylinder1195]
FEATURE [Part::Box] Box483  label="Krychle483"
  AttacherType = Attacher::AttachEngine3D
  Height = 6
  Length = 2
  Placement = pos=(32,48,22) rot=(0,0,1;0rad)
  Width = 6
FEATURE [Part::Box] Box484  label="Krychle484"
  AttacherType = Attacher::AttachEngine3D
  Height = 6
  Length = 2
  Placement = pos=(32,-54,22) rot=(0,0,1;0rad)
  Width = 6
FEATURE [Part::Box] Box485  label="Krychle485"
  AttacherType = Attacher::AttachEngine3D
  Height = 6
  Length = 2
  Placement = pos=(39,28,31) rot=(0,0,1;0rad)
  Width = 6
FEATURE [Part::Box] Box486  label="Krychle486"
  AttacherType = Attacher::AttachEngine3D
  Height = 6
  Length = 2
  Placement = pos=(39,-34,31) rot=(0,0,1;0rad)
  Width = 6
FEATURE [Part::Compound] Compound888
  Links = -> [Box483,Box484,Box485,Box486]
FEATURE [Part::Cut] Cut357
  Base = -> Cut356
  Tool = -> Compound887
FEATURE [Part::Cut] Cut358
  Base = -> Cut357
  Tool = -> Compound888
FEATURE [Part::Cylinder] Cylinder1196  label="Válec1196"
  Angle = 360
  AttacherType = Attacher::AttachEngine3D
  Height = 100
  Placement = pos=(24,51,25) rot=(0,1,0;1.5708rad)
  Radius = 1.5
FEATURE [Part::Cylinder] Cylinder1197  label="Válec1197"
  Angle = 360
  AttacherType = Attacher::AttachEngine3D
  Height = 100
  Placement = pos=(24,-51,25) rot=(0,1,0;1.5708rad)
  Radius = 1.5
FEATURE [Part::Cylinder] Cylinder1198  label="Válec1198"
  Angle = 360
  AttacherType = Attacher::AttachEngine3D
  Height = 100
  Placement = pos=(37,31,34) rot=(0,1,0;1.5708rad)
  Radius = 1.5
FEATURE [Part::Cylinder] Cylinder1199  label="Válec1199"
  Angle = 360
  AttacherType = Attacher::AttachEngine3D
  Height = 100
  Placement = pos=(37,-31,34) rot=(0,1,0;1.5708rad)
  Radius = 1.5
FEATURE [Part::Compound] Compound889
  Links = -> [Cylinder1196,Cylinder1197,Cylinder1198,Cylinder1199]
FEATURE [Part::Box] Box487  label="Krychle487"
  AttacherType = Attacher::AttachEngine3D
  Height = 6
  Length = 2
  Placement = pos=(32,48,22) rot=(0,0,1;0rad)
  Width = 6
FEATURE [Part::Box] Box488  label="Krychle488"
  AttacherType = Attacher::AttachEngine3D
  Height = 6
  Length = 2
  Placement = pos=(32,-54,22) rot=(0,0,1;0rad)
  Width = 6
FEATURE [Part::Box] Box489  label="Krychle489"
  AttacherType = Attacher::AttachEngine3D
  Height = 6
  Length = 2
  Placement = pos=(39,28,31) rot=(0,0,1;0rad)
  Width = 6
FEATURE [Part::Box] Box490  label="Krychle490"
  AttacherType = Attacher::AttachEngine3D
  Height = 6
  Length = 2
  Placement = pos=(39,-34,31) rot=(0,0,1;0rad)
  Width = 6
FEATURE [Part::Compound] Compound890
  Links = -> [Box487,Box488,Box489,Box490]
FEATURE [Part::Cylinder] Cylinder1200  label="Válec1200"
  Angle = 360
  AttacherType = Attacher::AttachEngine3D
  Height = 100
  Placement = pos=(24,51,25) rot=(0,1,0;1.5708rad)
  Radius = 1.5
FEATURE [Part::Cylinder] Cylinder1201  label="Válec1201"
  Angle = 360
  AttacherType = Attacher::AttachEngine3D
  Height = 100
  Placement = pos=(24,-51,25) rot=(0,1,0;1.5708rad)
  Radius = 1.5
FEATURE [Part::Cylinder] Cylinder1202  label="Válec1202"
  Angle = 360
  AttacherType = Attacher::AttachEngine3D
  Height = 100
  Placement = pos=(37,31,34) rot=(0,1,0;1.5708rad)
  Radius = 1.5
FEATURE [Part::Cylinder] Cylinder1203  label="Válec1203"
  Angle = 360
  AttacherType = Attacher::AttachEngine3D
  Height = 100
  Placement = pos=(37,-31,34) rot=(0,1,0;1.5708rad)
  Radius = 1.5
FEATURE [Part::Compound] Compound891
  Links = -> [Cylinder1200,Cylinder1201,Cylinder1202,Cylinder1203]
FEATURE [Part::Box] Box491  label="Krychle491"
  AttacherType = Attacher::AttachEngine3D
  Height = 6
  Length = 2
  Placement = pos=(32,48,22) rot=(0,0,1;0rad)
  Width = 6
FEATURE [Part::Box] Box492  label="Krychle492"
  AttacherType = Attacher::AttachEngine3D
  Height = 6
  Length = 2
  Placement = pos=(32,-54,22) rot=(0,0,1;0rad)
  Width = 6
FEATURE [Part::Box] Box493  label="Krychle493"
  AttacherType = Attacher::AttachEngine3D
  Height = 6
  Length = 2
  Placement = pos=(39,28,31) rot=(0,0,1;0rad)
  Width = 6
FEATURE [Part::Box] Box494  label="Krychle494"
  AttacherType = Attacher::AttachEngine3D
  Height = 6
  Length = 2
  Placement = pos=(39,-34,31) rot=(0,0,1;0rad)
  Width = 6
FEATURE [Part::Compound] Compound892
  Links = -> [Box491,Box492,Box493,Box494]
FEATURE [Part::Cut] Cut359
  Base = -> Cut352
  Tool = -> Compound892
FEATURE [Part::Cut] Cut360
  Base = -> Cut359
  Tool = -> Compound891
FEATURE [Part::Cut] Cut361
  Base = -> Cut353
  Tool = -> Compound889
FEATURE [Part::Cut] Cut362
  Base = -> Cut361
  Tool = -> Compound890
FEATURE [Part::Compound] Compound  label="J-midi-thin_bearing-ring"
  Links = -> [Cut358,Cut360,Cut362]
FEATURE [Part::FeaturePython] wormgear067  # WARN: FeaturePython — macro-defined, semantics opaque (R4)
  AttacherType = Attacher::AttachEngine3D
  beta = 39.4866
  clearance = 0.25
  diameter = 71
  head = 0
  height = 20
  module = 1.5
  pressure_angle = 20
  reverse_pitch = false
  teeth = 39
  version = 0.0.3
FEATURE [Part::FeaturePython] wormgear068  # WARN: FeaturePython — macro-defined, semantics opaque (R4)
  AttacherType = Attacher::AttachEngine3D
  Placement = pos=(0,0,0) rot=(0,0,-1;0.176278rad)
  beta = 39.4866
  clearance = 0.25
  diameter = 71
  head = 0
  height = 20
  module = 1.5
  pressure_angle = 20
  reverse_pitch = true
  teeth = 39
  version = 0.0.3
FEATURE [Part::Cylinder] Cylinder1211  label="Válec1211"
  Angle = 360
  AttacherType = Attacher::AttachEngine3D
  Height = 10
  Radius = 46
FEATURE [Part::Cut] Cut447
  Base = -> Cylinder1211
  Placement = pos=(0,0,2) rot=(0,0,1;0rad)
  Tool = -> wormgear067
FEATURE [Part::Cylinder] Cylinder1212  label="Válec1212"
  Angle = 360
  AttacherType = Attacher::AttachEngine3D
  Height = 10
  Radius = 54
FEATURE [Part::Cut] Cut448
  Base = -> Cylinder1212
  Placement = pos=(0,0,12) rot=(0,0,1;0.034907rad)
  Tool = -> wormgear068
FEATURE [Part::Cylinder] Cylinder1213  label="Válec1213"
  Angle = 360
  AttacherType = Attacher::AttachEngine3D
  Height = 50
  Placement = pos=(-7e-15,52,0) rot=(0,0,1;1.5708rad)
  Radius = 1.5
FEATURE [Part::Cylinder] Cylinder1214  label="Válec1214"
  Angle = 360
  AttacherType = Attacher::AttachEngine3D
  Height = 50
  Placement = pos=(52,0,0) rot=(0,0,1;0rad)
  Radius = 1.5
FEATURE [Part::Cylinder] Cylinder1215  label="Válec1215"
  Angle = 360
  AttacherType = Attacher::AttachEngine3D
  Height = 50
  Placement = pos=(36.7696,36.7696,0) rot=(0,0,1;0.785398rad)
  Radius = 1.5
FEATURE [Part::Cylinder] Cylinder1216  label="Válec1216"
  Angle = 360
  AttacherType = Attacher::AttachEngine3D
  Height = 50
  Placement = pos=(-52,-2.1e-14,0) rot=(0,0,1;3.14159rad)
  Radius = 1.5
FEATURE [Part::Cylinder] Cylinder1217  label="Válec1217"
  Angle = 360
  AttacherType = Attacher::AttachEngine3D
  Height = 50
  Placement = pos=(-36.7696,-36.7696,0) rot=(0,0,1;3.92699rad)
  Radius = 1.5
FEATURE [Part::Cylinder] Cylinder1218  label="Válec1218"
  Angle = 360
  AttacherType = Attacher::AttachEngine3D
  Height = 50
  Placement = pos=(2e-14,-52,0) rot=(0,0,-1;1.5708rad)
  Radius = 1.5
FEATURE [Part::Cylinder] Cylinder1219  label="Válec1219"
  Angle = 360
  AttacherType = Attacher::AttachEngine3D
  Height = 50
  Placement = pos=(36.7696,-36.7696,0) rot=(0,0,-1;0.785398rad)
  Radius = 1.5
FEATURE [Part::Cylinder] Cylinder1220  label="Válec1220"
  Angle = 360
  AttacherType = Attacher::AttachEngine3D
  Height = 50
  Placement = pos=(-36.7696,36.7696,0) rot=(0,0,1;2.35619rad)
  Radius = 1.5
FEATURE [Part::Box] Box511  label="Krychle511"
  AttacherType = Attacher::AttachEngine3D
  Height = 10
  Length = 4
  Placement = pos=(51,-6,12) rot=(0,0,1;0rad)
  Width = 12
FEATURE [Part::Cylinder] Cylinder1221  label="Válec1221"
  Angle = 360
  AttacherType = Attacher::AttachEngine3D
  Height = 50
  Placement = pos=(36.7696,36.7696,0) rot=(0,0,1;0.785398rad)
  Radius = 1.5
FEATURE [Part::Cylinder] Cylinder1222  label="Válec1222"
  Angle = 360
  AttacherType = Attacher::AttachEngine3D
  Height = 50
  Placement = pos=(36.7696,-36.7696,0) rot=(0,0,-1;0.785398rad)
  Radius = 1.5
FEATURE [Part::Cylinder] Cylinder1223  label="Válec1223"
  Angle = 360
  AttacherType = Attacher::AttachEngine3D
  Height = 50
  Placement = pos=(52,0,0) rot=(0,0,1;0rad)
  Radius = 1.5
FEATURE [Part::Cylinder] Cylinder1224  label="Válec1224"
  Angle = 360
  AttacherType = Attacher::AttachEngine3D
  Height = 50
  Placement = pos=(-52,-2.1e-14,0) rot=(0,0,1;3.14159rad)
  Radius = 1.5
FEATURE [Part::Cylinder] Cylinder1225  label="Válec1225"
  Angle = 360
  AttacherType = Attacher::AttachEngine3D
  Height = 50
  Placement = pos=(-36.7696,-36.7696,0) rot=(0,0,1;3.92699rad)
  Radius = 1.5
FEATURE [Part::Cylinder] Cylinder1226  label="Válec1226"
  Angle = 360
  AttacherType = Attacher::AttachEngine3D
  Height = 50
  Placement = pos=(-7e-15,52,0) rot=(0,0,1;1.5708rad)
  Radius = 1.5
FEATURE [Part::Cylinder] Cylinder1227  label="Válec1227"
  Angle = 360
  AttacherType = Attacher::AttachEngine3D
  Height = 50
  Placement = pos=(2e-14,-52,0) rot=(0,0,-1;1.5708rad)
  Radius = 1.5
FEATURE [Part::Cylinder] Cylinder1228  label="Válec1228"
  Angle = 360
  AttacherType = Attacher::AttachEngine3D
  Height = 50
  Placement = pos=(-36.7696,36.7696,0) rot=(0,0,1;2.35619rad)
  Radius = 1.5
FEATURE [Part::Compound] Compound898
  Links = -> [Cut448,Cut447]
FEATURE [Part::Compound] Compound899
  Links = -> [Cylinder1214,Cylinder1215,Cylinder1213,Cylinder1220,Cylinder1216,Cylinder1217,Cylinder1218,Cylinder1219]
  Placement = pos=(0,0,-7) rot=(0,0,1;0rad)
FEATURE [Part::Chamfer] Chamfer017
  Base = -> Box511
  Edges = 2 edges r=2: [Edge5,Edge7]
FEATURE [Part::Chamfer] Chamfer018
  Base = -> Box511
  Edges = 2 edges r=2: [Edge5,Edge7]
  Placement = pos=(0,0,0) rot=(0,0,1;0.785398rad)
FEATURE [Part::Chamfer] Chamfer019
  Base = -> Box511
  Edges = 2 edges r=2: [Edge5,Edge7]
  Placement = pos=(0,0,0) rot=(0,0,1;1.5708rad)
FEATURE [Part::Chamfer] Chamfer020
  Base = -> Box511
  Edges = 2 edges r=2: [Edge5,Edge7]
  Placement = pos=(0,0,0) rot=(0,0,1;2.35619rad)
FEATURE [Part::Chamfer] Chamfer021
  Base = -> Box511
  Edges = 2 edges r=2: [Edge5,Edge7]
  Placement = pos=(0,0,0) rot=(0,0,1;3.14159rad)
FEATURE [Part::Chamfer] Chamfer022
  Base = -> Box511
  Edges = 2 edges r=2: [Edge5,Edge7]
  Placement = pos=(0,0,0) rot=(0,0,1;3.92699rad)
FEATURE [Part::Chamfer] Chamfer023
  Base = -> Box511
  Edges = 2 edges r=2: [Edge5,Edge7]
  Placement = pos=(0,0,0) rot=(0,0,-1;1.5708rad)
FEATURE [Part::Chamfer] Chamfer024
  Base = -> Box511
  Edges = 2 edges r=2: [Edge5,Edge7]
  Placement = pos=(0,0,0) rot=(0,0,-1;0.785398rad)
FEATURE [Part::Compound] Compound901
  Links = -> [Chamfer017,Chamfer018,Chamfer019,Chamfer020,Chamfer021,Chamfer022,Chamfer023,Chamfer024]
FEATURE [Part::Cut] Cut449
  Base = -> Compound901
  Tool = -> Compound899
FEATURE [Part::Compound] Compound902
  Links = -> [Cylinder1223,Cylinder1221,Cylinder1226,Cylinder1228,Cylinder1224,Cylinder1225,Cylinder1227,Cylinder1222]
  Placement = pos=(0,0,-7) rot=(0,0,1;0rad)
FEATURE [Part::Cut] Cut450
  Base = -> Compound898
  Tool = -> Compound902
FEATURE [Part::Cylinder] Cylinder1237  label="Válec1237"
  Angle = 360
  AttacherType = Attacher::AttachEngine3D
  Height = 40
  Placement = pos=(214,56,-30) rot=(0,0,1;0rad)
  Radius = 12
FEATURE [Part::Cylinder] Cylinder1238  label="Válec1238"
  Angle = 360
  AttacherType = Attacher::AttachEngine3D
  Height = 40
  Placement = pos=(202,50,-28) rot=(0,0,1;0rad)
  Radius = 12
FEATURE [Part::Cylinder] Cylinder1239  label="Válec1239"
  Angle = 360
  AttacherType = Attacher::AttachEngine3D
  Height = 40
  Placement = pos=(202,50,-28) rot=(0,0,1;0rad)
  Radius = 12
FEATURE [Part::Box] Box512  label="Krychle512"
  AttacherType = Attacher::AttachEngine3D
  Height = 28
  Length = 6
  Placement = pos=(26,28,-6) rot=(0,0,1;0rad)
  Width = 10
FEATURE [Part::Cylinder] Cylinder1240  label="Válec1240"
  Angle = 360
  AttacherType = Attacher::AttachEngine3D
  Height = 40
  Placement = pos=(256,0,-30) rot=(0,0,1;0rad)
  Radius = 10
FEATURE [Part::Box] Box513  label="Krychle513"
  AttacherType = Attacher::AttachEngine3D
  Height = 28
  Length = 8
  Placement = pos=(238,0,-6) rot=(0,0,1;0rad)
  Width = 38
FEATURE [Part::Box] Box514  label="Krychle514"
  AttacherType = Attacher::AttachEngine3D
  Height = 2
  Length = 8
  Placement = pos=(37,-3,-4) rot=(0,0,1;0rad)
  Width = 6
FEATURE [Part::Box] Box515  label="Krychle515"
  AttacherType = Attacher::AttachEngine3D
  Height = 28
  Length = 6
  Placement = pos=(32,24,-6) rot=(0,0,1;0rad)
  Width = 14
FEATURE [Part::Compound] Compound908
  Links = -> [Box512,Box515]
FEATURE [Part::Cylinder] Cylinder1241  label="Válec1241"
  Angle = 360
  AttacherType = Attacher::AttachEngine3D
  Height = 40
  Placement = pos=(214,56,-30) rot=(0,0,1;0rad)
  Radius = 12
FEATURE [Part::Compound] Compound909
  Links = -> [Cylinder1240,Cylinder1241]
  Placement = pos=(0,0,2) rot=(0,0,1;0rad)
FEATURE [Part::Box] Box516  label="Krychle516"
  AttacherType = Attacher::AttachEngine3D
  Height = 28
  Length = 46
  Placement = pos=(200,38,-6) rot=(0,0,1;0rad)
  Width = 16
FEATURE [Part::Box] Box517  label="Krychle517"
  AttacherType = Attacher::AttachEngine3D
  Height = 28
  Length = 8
  Placement = pos=(238,0,-6) rot=(0,0,1;0rad)
  Width = 38
FEATURE [Part::Compound] Compound911
  Links = -> [Box517,Box516]
FEATURE [Part::Cut] Cut452
  Base = -> Compound911
  Tool = -> Compound909
FEATURE [Part::Cut] Cut457
  Base = -> Cut452
  Placement = pos=(-200,0,0) rot=(0,0,1;0rad)
  Tool = -> Cylinder1238
FEATURE [Part::Box] Box518  label="Krychle518"
  AttacherType = Attacher::AttachEngine3D
  Height = 28
  Length = 6
  Placement = pos=(26,28,-6) rot=(0,0,1;0rad)
  Width = 10
FEATURE [Part::Box] Box519  label="Krychle519"
  AttacherType = Attacher::AttachEngine3D
  Height = 28
  Length = 6
  Placement = pos=(32,24,-6) rot=(0,0,1;0rad)
  Width = 14
FEATURE [Part::Cylinder] Cylinder1242  label="Válec1242"
  Angle = 360
  AttacherType = Attacher::AttachEngine3D
  Height = 60
  Placement = pos=(1.2e-14,-41,-54) rot=(0,0,-1;1.5708rad)
  Radius = 1.5
FEATURE [Part::Box] Box520  label="Krychle520"
  AttacherType = Attacher::AttachEngine3D
  Height = 2
  Length = 8
  Placement = pos=(3,37,-4) rot=(0,0,1;1.5708rad)
  Width = 6
FEATURE [Part::Box] Box521  label="Krychle521"
  AttacherType = Attacher::AttachEngine3D
  Height = 2
  Length = 8
  Placement = pos=(28.2843,24.0416,-4) rot=(0,0,1;0.785398rad)
  Width = 6
FEATURE [Part::Box] Box522  label="Krychle522"
  AttacherType = Attacher::AttachEngine3D
  Height = 2
  Length = 8
  Placement = pos=(-24.0416,28.2843,-4) rot=(0,0,1;2.35619rad)
  Width = 6
FEATURE [Part::Box] Box523  label="Krychle523"
  AttacherType = Attacher::AttachEngine3D
  Height = 2
  Length = 8
  Placement = pos=(-3,-37,-4) rot=(0,0,-1;1.5708rad)
  Width = 6
FEATURE [Part::Cylinder] Cylinder1243  label="Válec1243"
  Angle = 360
  AttacherType = Attacher::AttachEngine3D
  Height = 40
  Placement = pos=(256,0,-30) rot=(0,0,1;0rad)
  Radius = 10
FEATURE [Part::Box] Box524  label="Krychle524"
  AttacherType = Attacher::AttachEngine3D
  Height = 28
  Length = 46
  Placement = pos=(200,38,-6) rot=(0,0,1;0rad)
  Width = 16
FEATURE [Part::Compound] Compound910
  Links = -> [Box513,Box524]
FEATURE [Part::Cylinder] Cylinder1244  label="Válec1244"
  Angle = 360
  AttacherType = Attacher::AttachEngine3D
  Height = 60
  Placement = pos=(28.9914,-28.9914,-54) rot=(0,0,-1;0.785398rad)
  Radius = 1.5
FEATURE [Part::Cylinder] Cylinder1245  label="Válec1245"
  Angle = 360
  AttacherType = Attacher::AttachEngine3D
  Height = 60
  Placement = pos=(41,0,-54) rot=(0,0,1;0rad)
  Radius = 1.5
FEATURE [Part::Box] Box525  label="Krychle525"
  AttacherType = Attacher::AttachEngine3D
  Height = 2
  Length = 8
  Placement = pos=(24.0416,-28.2843,-4) rot=(0,0,-1;0.785398rad)
  Width = 6
FEATURE [Part::Cylinder] Cylinder1246  label="Válec1246"
  Angle = 360
  AttacherType = Attacher::AttachEngine3D
  Height = 60
  Placement = pos=(28.9914,28.9914,-54) rot=(0,0,1;0.785398rad)
  Radius = 1.5
FEATURE [Part::Box] Box526  label="Krychle526"
  AttacherType = Attacher::AttachEngine3D
  Height = 2
  Length = 8
  Placement = pos=(-37,3,-4) rot=(0,0,1;3.14159rad)
  Width = 6
FEATURE [Part::Cylinder] Cylinder1247  label="Válec1247"
  Angle = 360
  AttacherType = Attacher::AttachEngine3D
  Height = 60
  Placement = pos=(-28.9914,28.9914,-54) rot=(0,0,1;2.35619rad)
  Radius = 1.5
FEATURE [Part::Box] Box527  label="Krychle527"
  AttacherType = Attacher::AttachEngine3D
  Height = 2
  Length = 8
  Placement = pos=(-28.2843,-24.0416,-4) rot=(0,0,1;3.92699rad)
  Width = 6
FEATURE [Part::Cylinder] Cylinder1248  label="Válec1248"
  Angle = 360
  AttacherType = Attacher::AttachEngine3D
  Height = 60
  Placement = pos=(-4e-15,41,-54) rot=(0,0,1;1.5708rad)
  Radius = 1.5
FEATURE [Part::Compound] Compound913
  Links = -> [Cylinder1243,Cylinder1237]
  Placement = pos=(0,0,2) rot=(0,0,1;0rad)
FEATURE [Part::Cut] Cut453
  Base = -> Compound910
  Tool = -> Compound913
FEATURE [Part::Cut] Cut455
  Base = -> Cut453
  Placement = pos=(-200,0,0) rot=(0,0,1;0rad)
  Tool = -> Cylinder1239
FEATURE [Part::Compound] Compound907
  Links = -> [Cut455,Compound908]
FEATURE [Part::Mirroring] mirror013  label="Compound196 (mirrored)002"
  Base = (0,0,0)
  Normal = (1e-16,-1,0)
  Source = -> Compound907
FEATURE [Part::Compound] Compound914
  Links = -> [Box518,Box519]
FEATURE [Part::Compound] Compound912
  Links = -> [Cut457,Compound914]
FEATURE [Part::Compound] Compound917
  Links = -> [mirror013,Compound912]
FEATURE [Part::Compound] Compound918
  Links = -> [Box521,Box520,Box522,Box526,Box527,Box523,Box525,Box514]
  Placement = pos=(0,0,0) rot=(0,0,1;0.392699rad)
FEATURE [Part::Cut] Cut454
  Base = -> Compound917
  Tool = -> Compound918
FEATURE [Part::Cylinder] Cylinder1249  label="Válec1249"
  Angle = 360
  AttacherType = Attacher::AttachEngine3D
  Height = 60
  Placement = pos=(-28.9914,-28.9914,-54) rot=(0,0,1;3.92699rad)
  Radius = 1.5
FEATURE [Part::Cylinder] Cylinder1250  label="Válec1250"
  Angle = 360
  AttacherType = Attacher::AttachEngine3D
  Height = 60
  Placement = pos=(-41,-1.1e-14,-54) rot=(0,0,1;3.14159rad)
  Radius = 1.5
FEATURE [Part::Compound] Compound906
  Links = -> [Cylinder1246,Cylinder1248,Cylinder1247,Cylinder1250,Cylinder1249,Cylinder1242,Cylinder1244,Cylinder1245]
  Placement = pos=(0,0,0) rot=(0,0,1;0.392699rad)
FEATURE [Part::Cut] Cut458
  Base = -> Cut454
  Tool = -> Compound906
FEATURE [Part::Cylinder] Cylinder1251  label="Válec1251"
  Angle = 360
  AttacherType = Attacher::AttachEngine3D
  Height = 60
  Placement = pos=(32,51,7) rot=(0,1,0;1.5708rad)
  Radius = 1.5
FEATURE [Part::Box] Box528  label="Krychle528"
  AttacherType = Attacher::AttachEngine3D
  Height = 6
  Length = 2
  Placement = pos=(36,-54,4) rot=(0,0,1;0rad)
  Width = 6
FEATURE [Part::Box] Box529  label="Krychle529"
  AttacherType = Attacher::AttachEngine3D
  Height = 6
  Length = 2
  Placement = pos=(36,-26,-8) rot=(0,0,1;0rad)
  Width = 6
FEATURE [Part::Box] Box530  label="Krychle530"
  AttacherType = Attacher::AttachEngine3D
  Height = 6
  Length = 2
  Placement = pos=(36,20,-8) rot=(0,0,1;0rad)
  Width = 6
FEATURE [Part::Cylinder] Cylinder1252  label="Válec1252"
  Angle = 360
  AttacherType = Attacher::AttachEngine3D
  Height = 50
  Placement = pos=(36.77,36.77,-40) rot=(0,0,1;0.785398rad)
  Radius = 4
FEATURE [Part::Cylinder] Cylinder1253  label="Válec1253"
  Angle = 360
  AttacherType = Attacher::AttachEngine3D
  Height = 60
  Placement = pos=(32,23,-5) rot=(0,1,0;1.5708rad)
  Radius = 1.5
FEATURE [Part::Cylinder] Cylinder1254  label="Válec1254"
  Angle = 360
  AttacherType = Attacher::AttachEngine3D
  Height = 60
  Placement = pos=(32,-23,-5) rot=(0,1,0;1.5708rad)
  Radius = 1.5
FEATURE [Part::Cylinder] Cylinder1255  label="Válec1255"
  Angle = 360
  AttacherType = Attacher::AttachEngine3D
  Height = 60
  Placement = pos=(32,-51,7) rot=(0,1,0;1.5708rad)
  Radius = 1.5
FEATURE [Part::Compound] Compound904
  Links = -> [Cylinder1253,Cylinder1254,Cylinder1251,Cylinder1255]
  Placement = pos=(0,0,2) rot=(0,0,1;0rad)
FEATURE [Part::Cylinder] Cylinder1256  label="Válec1256"
  Angle = 360
  AttacherType = Attacher::AttachEngine3D
  Height = 50
  Placement = pos=(36.77,-36.77,-40) rot=(0,0,1;0.785398rad)
  Radius = 4
FEATURE [Part::Compound] Compound905
  Links = -> [Cylinder1252,Cylinder1256]
  Placement = pos=(0,0,2) rot=(0,0,1;0rad)
FEATURE [Part::Box] Box531  label="Krychle531"
  AttacherType = Attacher::AttachEngine3D
  Height = 6
  Length = 2
  Placement = pos=(36,48,4) rot=(0,0,1;0rad)
  Width = 6
FEATURE [Part::Compound] Compound916
  Links = -> [Box530,Box529,Box531,Box528]
  Placement = pos=(0,0,2) rot=(0,0,1;0rad)
FEATURE [Part::Cylinder] Cylinder1257  label="Válec1257"
  Angle = 360
  AttacherType = Attacher::AttachEngine3D
  Height = 50
  Placement = pos=(-36.7696,36.7696,0) rot=(0,0,1;2.35619rad)
  Radius = 1.5
FEATURE [Part::Cylinder] Cylinder1258  label="Válec1258"
  Angle = 360
  AttacherType = Attacher::AttachEngine3D
  Height = 50
  Placement = pos=(36.7696,36.7696,0) rot=(0,0,1;0.785398rad)
  Radius = 1.5
FEATURE [Part::Cylinder] Cylinder1259  label="Válec1259"
  Angle = 360
  AttacherType = Attacher::AttachEngine3D
  Height = 50
  Placement = pos=(36.7696,-36.7696,0) rot=(0,0,-1;0.785398rad)
  Radius = 1.5
FEATURE [Part::Cylinder] Cylinder1260  label="Válec1260"
  Angle = 360
  AttacherType = Attacher::AttachEngine3D
  Height = 50
  Placement = pos=(-52,-2.1e-14,0) rot=(0,0,1;3.14159rad)
  Radius = 1.5
FEATURE [Part::Cylinder] Cylinder1261  label="Válec1261"
  Angle = 360
  AttacherType = Attacher::AttachEngine3D
  Height = 50
  Placement = pos=(-36.7696,-36.7696,0) rot=(0,0,1;3.92699rad)
  Radius = 1.5
FEATURE [Part::Cylinder] Cylinder1262  label="Válec1262"
  Angle = 360
  AttacherType = Attacher::AttachEngine3D
  Height = 50
  Placement = pos=(52,0,0) rot=(0,0,1;0rad)
  Radius = 1.5
FEATURE [Part::Cylinder] Cylinder1263  label="Válec1263"
  Angle = 360
  AttacherType = Attacher::AttachEngine3D
  Height = 50
  Placement = pos=(-7e-15,52,0) rot=(0,0,1;1.5708rad)
  Radius = 1.5
FEATURE [Part::Cylinder] Cylinder1264  label="Válec1264"
  Angle = 360
  AttacherType = Attacher::AttachEngine3D
  Height = 50
  Placement = pos=(2e-14,-52,0) rot=(0,0,-1;1.5708rad)
  Radius = 1.5
FEATURE [Part::Compound] Compound915
  Links = -> [Cylinder1262,Cylinder1258,Cylinder1263,Cylinder1257,Cylinder1260,Cylinder1261,Cylinder1264,Cylinder1259]
FEATURE [Part::Cut] Cut459
  Base = -> Cut458
  Tool = -> Compound915
FEATURE [Part::Cut] Cut456
  Base = -> Cut459
  Tool = -> Compound916
FEATURE [Part::Cut] Cut451
  Base = -> Cut456
  Tool = -> Compound904
FEATURE [Part::Cylinder] Cylinder1265  label="Válec1265"
  Angle = 360
  AttacherType = Attacher::AttachEngine3D
  Height = 60
  Placement = pos=(41,0,-54) rot=(0,0,1;0rad)
  Radius = 1.5
FEATURE [Part::Box] Box532  label="Krychle532"
  AttacherType = Attacher::AttachEngine3D
  Height = 2
  Length = 8
  Placement = pos=(37,-3,-4) rot=(0,0,1;0rad)
  Width = 6
FEATURE [Part::Cylinder] Cylinder1266  label="Válec1266"
  Angle = 360
  AttacherType = Attacher::AttachEngine3D
  Height = 60
  Placement = pos=(-41,-1.1e-14,-54) rot=(0,0,1;3.14159rad)
  Radius = 1.5
FEATURE [Part::Cylinder] Cylinder1267  label="Válec1267"
  Angle = 360
  AttacherType = Attacher::AttachEngine3D
  Height = 60
  Placement = pos=(-28.9914,-28.9914,-54) rot=(0,0,1;3.92699rad)
  Radius = 1.5
FEATURE [Part::Box] Box533  label="Krychle533"
  AttacherType = Attacher::AttachEngine3D
  Height = 2
  Length = 8
  Placement = pos=(3,37,-4) rot=(0,0,1;1.5708rad)
  Width = 6
FEATURE [Part::Box] Box534  label="Krychle534"
  AttacherType = Attacher::AttachEngine3D
  Height = 2
  Length = 8
  Placement = pos=(-37,3,-4) rot=(0,0,1;3.14159rad)
  Width = 6
FEATURE [Part::Cylinder] Cylinder1268  label="Válec1268"
  Angle = 360
  AttacherType = Attacher::AttachEngine3D
  Height = 60
  Placement = pos=(28.9914,-28.9914,-54) rot=(0,0,-1;0.785398rad)
  Radius = 1.5
FEATURE [Part::Box] Box535  label="Krychle535"
  AttacherType = Attacher::AttachEngine3D
  Height = 2
  Length = 8
  Placement = pos=(28.2843,24.0416,-4) rot=(0,0,1;0.785398rad)
  Width = 6
FEATURE [Part::Box] Box536  label="Krychle536"
  AttacherType = Attacher::AttachEngine3D
  Height = 2
  Length = 8
  Placement = pos=(-28.2843,-24.0416,-4) rot=(0,0,1;3.92699rad)
  Width = 6
FEATURE [Part::Cylinder] Cylinder1269  label="Válec1269"
  Angle = 360
  AttacherType = Attacher::AttachEngine3D
  Height = 60
  Placement = pos=(28.9914,28.9914,-54) rot=(0,0,1;0.785398rad)
  Radius = 1.5
FEATURE [Part::Box] Box537  label="Krychle537"
  AttacherType = Attacher::AttachEngine3D
  Height = 2
  Length = 8
  Placement = pos=(-3,-37,-4) rot=(0,0,-1;1.5708rad)
  Width = 6
FEATURE [Part::Box] Box538  label="Krychle538"
  AttacherType = Attacher::AttachEngine3D
  Height = 2
  Length = 8
  Placement = pos=(24.0416,-28.2843,-4) rot=(0,0,-1;0.785398rad)
  Width = 6
FEATURE [Part::Cylinder] Cylinder1270  label="Válec1270"
  Angle = 360
  AttacherType = Attacher::AttachEngine3D
  Height = 60
  Placement = pos=(1.2e-14,-41,-54) rot=(0,0,-1;1.5708rad)
  Radius = 1.5
FEATURE [Part::Cut] Cut460
  Base = -> Cut451
  Tool = -> Compound905
FEATURE [Part::FeaturePython] Tube112  # WARN: FeaturePython — macro-defined, semantics opaque (R4)
  AttacherType = Attacher::AttachEngine3D
  Height = 8
  InnerRadius = 38
  OuterRadius = 46
  Placement = pos=(0,0,-8) rot=(0,0,1;0rad)
FEATURE [Part::Box] Box539  label="Krychle539"
  AttacherType = Attacher::AttachEngine3D
  Height = 2
  Length = 8
  Placement = pos=(-24.0416,28.2843,-4) rot=(0,0,1;2.35619rad)
  Width = 6
FEATURE [Part::Compound] Compound921
  Links = -> [Box535,Box533,Box539,Box534,Box536,Box537,Box538,Box532]
  Placement = pos=(0,0,0) rot=(0,0,1;0.392699rad)
FEATURE [Part::Cylinder] Cylinder1271  label="Válec1271"
  Angle = 360
  AttacherType = Attacher::AttachEngine3D
  Height = 60
  Placement = pos=(-28.9914,28.9914,-54) rot=(0,0,1;2.35619rad)
  Radius = 1.5
FEATURE [Part::Cylinder] Cylinder1272  label="Válec1272"
  Angle = 360
  AttacherType = Attacher::AttachEngine3D
  Height = 60
  Placement = pos=(-4e-15,41,-54) rot=(0,0,1;1.5708rad)
  Radius = 1.5
FEATURE [Part::Compound] Compound919
  Links = -> [Cylinder1269,Cylinder1272,Cylinder1271,Cylinder1266,Cylinder1267,Cylinder1270,Cylinder1268,Cylinder1265]
  Placement = pos=(0,0,0) rot=(0,0,1;0.392699rad)
FEATURE [Part::Cut] Cut461
  Base = -> Tube112
  Tool = -> Compound919
FEATURE [Part::Cut] Cut462
  Base = -> Cut461
  Tool = -> Compound921
FEATURE [Part::Box] Box540  label="Krychle540"
  AttacherType = Attacher::AttachEngine3D
  Height = 6
  Length = 2
  Placement = pos=(36,20,-8) rot=(0,0,1;0rad)
  Width = 6
FEATURE [Part::Cylinder] Cylinder1273  label="Válec1273"
  Angle = 360
  AttacherType = Attacher::AttachEngine3D
  Height = 60
  Placement = pos=(28,-51,7) rot=(0,1,0;1.5708rad)
  Radius = 1.5
FEATURE [Part::Cylinder] Cylinder1274  label="Válec1274"
  Angle = 360
  AttacherType = Attacher::AttachEngine3D
  Height = 60
  Placement = pos=(32,-23,-5) rot=(0,1,0;1.5708rad)
  Radius = 1.5
FEATURE [Part::Cylinder] Cylinder1275  label="Válec1275"
  Angle = 360
  AttacherType = Attacher::AttachEngine3D
  Height = 60
  Placement = pos=(32,23,-5) rot=(0,1,0;1.5708rad)
  Radius = 1.5
FEATURE [Part::Box] Box541  label="Krychle541"
  AttacherType = Attacher::AttachEngine3D
  Height = 6
  Length = 2
  Placement = pos=(32,-54,4) rot=(0,0,1;0rad)
  Width = 6
FEATURE [Part::Box] Box542  label="Krychle542"
  AttacherType = Attacher::AttachEngine3D
  Height = 6
  Length = 2
  Placement = pos=(32,48,4) rot=(0,0,1;0rad)
  Width = 6
FEATURE [Part::Box] Box543  label="Krychle543"
  AttacherType = Attacher::AttachEngine3D
  Height = 6
  Length = 2
  Placement = pos=(36,-26,-8) rot=(0,0,1;0rad)
  Width = 6
FEATURE [Part::Compound] Compound922
  Links = -> [Box540,Box543,Box542,Box541]
FEATURE [Part::Cut] Cut463
  Base = -> Cut462
  Tool = -> Compound922
FEATURE [Part::Cylinder] Cylinder1276  label="Válec1276"
  Angle = 360
  AttacherType = Attacher::AttachEngine3D
  Height = 60
  Placement = pos=(28,51,7) rot=(0,1,0;1.5708rad)
  Radius = 1.5
FEATURE [Part::Compound] Compound920
  Links = -> [Cylinder1275,Cylinder1274,Cylinder1276,Cylinder1273]
FEATURE [Part::Cut] Cut464
  Base = -> Cut463
  Placement = pos=(0,0,2) rot=(0,0,1;0rad)
  Tool = -> Compound920
FEATURE [Part::Cylinder] Cylinder1277  label="Válec1277"
  Angle = 360
  AttacherType = Attacher::AttachEngine3D
  Height = 60
  Placement = pos=(41,0,-54) rot=(0,0,1;0rad)
  Radius = 1.5
FEATURE [Part::Cylinder] Cylinder1278  label="Válec1278"
  Angle = 360
  AttacherType = Attacher::AttachEngine3D
  Height = 60
  Placement = pos=(-41,-1.1e-14,-54) rot=(0,0,1;3.14159rad)
  Radius = 1.5
FEATURE [Part::Cylinder] Cylinder1279  label="Válec1279"
  Angle = 360
  AttacherType = Attacher::AttachEngine3D
  Height = 60
  Placement = pos=(-28.9914,-28.9914,-54) rot=(0,0,1;3.92699rad)
  Radius = 1.5
FEATURE [Part::Cylinder] Cylinder1280  label="Válec1280"
  Angle = 360
  AttacherType = Attacher::AttachEngine3D
  Height = 60
  Placement = pos=(28.9914,-28.9914,-54) rot=(0,0,-1;0.785398rad)
  Radius = 1.5
FEATURE [Part::Cylinder] Cylinder1281  label="Válec1281"
  Angle = 360
  AttacherType = Attacher::AttachEngine3D
  Height = 60
  Placement = pos=(28.9914,28.9914,-54) rot=(0,0,1;0.785398rad)
  Radius = 1.5
FEATURE [Part::Cylinder] Cylinder1282  label="Válec1282"
  Angle = 360
  AttacherType = Attacher::AttachEngine3D
  Height = 60
  Placement = pos=(-28.9914,28.9914,-54) rot=(0,0,1;2.35619rad)
  Radius = 1.5
FEATURE [Part::Cylinder] Cylinder1283  label="Válec1283"
  Angle = 360
  AttacherType = Attacher::AttachEngine3D
  Height = 60
  Placement = pos=(1.2e-14,-41,-54) rot=(0,0,-1;1.5708rad)
  Radius = 1.5
FEATURE [Part::Cylinder] Cylinder1284  label="Válec1284"
  Angle = 360
  AttacherType = Attacher::AttachEngine3D
  Height = 60
  Placement = pos=(-4e-15,41,-54) rot=(0,0,1;1.5708rad)
  Radius = 1.5
FEATURE [Part::Compound] Compound923
  Links = -> [Cylinder1281,Cylinder1284,Cylinder1282,Cylinder1278,Cylinder1279,Cylinder1283,Cylinder1280,Cylinder1277]
  Placement = pos=(0,0,0) rot=(0,0,1;0.392699rad)
FEATURE [Part::Cut] Cut465
  Base = -> Cut450
  Tool = -> Compound923
FEATURE [Part::Fillet] Fillet
  Base = -> Cut460
  Edges = 2 edges r=12: [Edge83,Edge290]
FEATURE [Part::Compound] Compound924  label="J-midi-thin_monoblok_v1.0"
  Links = -> [Cut449,Cut464,Cut465,Fillet]
FEATURE [Part::Wedge] Wedge020  label="Klín020"
  AttacherType = Attacher::AttachEngine3D
  Placement = pos=(0,0,12) rot=(0,0,-1;1.5708rad)
  X2max = 0
  X2min = 0
  Xmax = 10
  Xmin = -10
  Ymax = 0
  Ymin = -32
  Z2max = 12
  Z2min = 0
  Zmax = 12
  Zmin = 0
FEATURE [Part::Wedge] Wedge021  label="Klín021"
  AttacherType = Attacher::AttachEngine3D
  Placement = pos=(0,0,12) rot=(0,0,1;0rad)
  X2max = 0
  X2min = 0
  Xmax = 10
  Xmin = -10
  Ymax = 0
  Ymin = -32
  Z2max = 12
  Z2min = 0
  Zmax = 12
  Zmin = 0
FEATURE [Part::Wedge] Wedge022  label="Klín022"
  AttacherType = Attacher::AttachEngine3D
  Placement = pos=(0,0,12) rot=(0,0,1;3.14159rad)
  X2max = 0
  X2min = 0
  Xmax = 10
  Xmin = -10
  Ymax = 0
  Ymin = -32
  Z2max = 12
  Z2min = 0
  Zmax = 12
  Zmin = 0
FEATURE [Part::Wedge] Wedge023  label="Klín023"
  AttacherType = Attacher::AttachEngine3D
  Placement = pos=(0,0,12) rot=(0,0,1;1.5708rad)
  X2max = 0
  X2min = 0
  Xmax = 10
  Xmin = -10
  Ymax = 0
  Ymin = -32
  Z2max = 12
  Z2min = 0
  Zmax = 12
  Zmin = 0
FEATURE [Part::Cylinder] Cylinder1024  label="Válec1024"
  Angle = 360
  AttacherType = Attacher::AttachEngine3D
  Height = 20
  Placement = pos=(-4.25,4.25,-88) rot=(0,0,-1;1.5708rad)
  Radius = 1
FEATURE [Part::Cylinder] Cylinder1025  label="Válec1025"
  Angle = 360
  AttacherType = Attacher::AttachEngine3D
  Height = 20
  Placement = pos=(-4.25,-4.25,-88) rot=(0,0,1;0rad)
  Radius = 1
FEATURE [Part::Cylinder] Cylinder1026  label="Válec1026"
  Angle = 360
  AttacherType = Attacher::AttachEngine3D
  Height = 2
  Placement = pos=(-4.25,-4.25,-88) rot=(0,0,1;0rad)
  Radius = 2
FEATURE [Part::Cylinder] Cylinder1027  label="Válec1027"
  Angle = 360
  AttacherType = Attacher::AttachEngine3D
  Height = 20
  Placement = pos=(-4.25,4.25,-88) rot=(0,0,-1;1.5708rad)
  Radius = 1
FEATURE [Part::Cylinder] Cylinder1028  label="Válec1028"
  Angle = 360
  AttacherType = Attacher::AttachEngine3D
  Height = 20
  Placement = pos=(-4.25,-4.25,-88) rot=(0,0,1;0rad)
  Radius = 1
FEATURE [Part::Cylinder] Cylinder1029  label="Válec1029"
  Angle = 360
  AttacherType = Attacher::AttachEngine3D
  Height = 20
  Placement = pos=(4.25,4.25,-88) rot=(0,0,1;3.14159rad)
  Radius = 1
FEATURE [Part::Cylinder] Cylinder1030  label="Válec1030"
  Angle = 360
  AttacherType = Attacher::AttachEngine3D
  Height = 50
  Placement = pos=(0,0,-10) rot=(0,0,1;0rad)
  Radius = 2.6
FEATURE [Part::Cylinder] Cylinder1031  label="Válec1031"
  Angle = 360
  AttacherType = Attacher::AttachEngine3D
  Height = 20
  Placement = pos=(-4.25,-4.25,-88) rot=(0,0,1;0rad)
  Radius = 1
FEATURE [Part::Cylinder] Cylinder1032  label="Válec1032"
  Angle = 360
  AttacherType = Attacher::AttachEngine3D
  Height = 20
  Placement = pos=(4.25,4.25,-88) rot=(0,0,1;3.14159rad)
  Radius = 1
FEATURE [Part::Cylinder] Cylinder1033  label="Válec1033"
  Angle = 360
  AttacherType = Attacher::AttachEngine3D
  Height = 2
  Placement = pos=(-4.25,4.25,-88) rot=(0,0,-1;1.5708rad)
  Radius = 2
FEATURE [Part::Cylinder] Cylinder1034  label="Válec1034"
  Angle = 360
  AttacherType = Attacher::AttachEngine3D
  Height = 2
  Placement = pos=(4.25,4.25,-88) rot=(0,0,1;3.14159rad)
  Radius = 2
FEATURE [Part::Cylinder] Cylinder1035  label="Válec1035"
  Angle = 360
  AttacherType = Attacher::AttachEngine3D
  Height = 4
  Placement = pos=(0,0,15) rot=(0,0,1;0rad)
  Radius = 8
FEATURE [Part::Cylinder] Cylinder1036  label="Válec1036"
  Angle = 360
  AttacherType = Attacher::AttachEngine3D
  Height = 20
  Placement = pos=(4.25,-4.25,-88) rot=(0,0,1;1.5708rad)
  Radius = 1
FEATURE [Part::Cylinder] Cylinder1037  label="Válec1037"
  Angle = 360
  AttacherType = Attacher::AttachEngine3D
  Height = 20
  Placement = pos=(4.25,-4.25,-88) rot=(0,0,1;1.5708rad)
  Radius = 1
FEATURE [Part::Cylinder] Cylinder1038  label="Válec1038"
  Angle = 360
  AttacherType = Attacher::AttachEngine3D
  Height = 20
  Placement = pos=(-4.25,4.25,-88) rot=(0,0,-1;1.5708rad)
  Radius = 1
FEATURE [Part::Cylinder] Cylinder1039  label="Válec1039"
  Angle = 360
  AttacherType = Attacher::AttachEngine3D
  Height = 2
  Placement = pos=(4.25,-4.25,-88) rot=(0,0,1;1.5708rad)
  Radius = 2
FEATURE [Part::Cylinder] Cylinder1040  label="Válec1040"
  Angle = 360
  AttacherType = Attacher::AttachEngine3D
  Height = 20
  Placement = pos=(4.25,-4.25,-88) rot=(0,0,1;1.5708rad)
  Radius = 1
FEATURE [Part::Compound] Compound826
  Links = -> [Cylinder1025,Cylinder1040,Cylinder1032,Cylinder1038]
  Placement = pos=(0,0,91) rot=(0,0,1;0rad)
FEATURE [Part::Cylinder] Cylinder1041  label="Válec1041"
  Angle = 360
  AttacherType = Attacher::AttachEngine3D
  Height = 20
  Placement = pos=(4.25,4.25,-88) rot=(0,0,1;3.14159rad)
  Radius = 1
FEATURE [Part::FeaturePython] Tube086  # WARN: FeaturePython — macro-defined, semantics opaque (R4)
  AttacherType = Attacher::AttachEngine3D
  Height = 12
  InnerRadius = 4.1
  OuterRadius = 8
  Placement = pos=(0,0,12) rot=(0,0,1;0rad)
FEATURE [Part::FeaturePython] Tube087  # WARN: FeaturePython — macro-defined, semantics opaque (R4)
  AttacherType = Attacher::AttachEngine3D
  Height = 10
  InnerRadius = 2.6
  OuterRadius = 8
  Placement = pos=(0,0,19) rot=(0,0,1;0rad)
FEATURE [Part::FeaturePython] wormgear047  # WARN: FeaturePython — macro-defined, semantics opaque (R4)
  AttacherType = Attacher::AttachEngine3D
  Placement = pos=(0,0,29) rot=(0,0,1;0.994838rad)
  beta = 32.6192
  clearance = 0.25
  diameter = 22.5
  head = 0
  height = 8
  module = 1.2
  pressure_angle = 20
  reverse_pitch = false
  teeth = 12
  version = 0.0.3
FEATURE [Part::Cut] Cut377
  Base = -> wormgear047
  Tool = -> Cylinder1030
FEATURE [Part::Compound] Compound827
  Links = -> [Cylinder1026,Cylinder1039,Cylinder1034,Cylinder1033]
  Placement = pos=(0,0,91) rot=(0,0,1;0rad)
FEATURE [Part::Compound] Compound829
  Links = -> [Cylinder1031,Cylinder1037,Cylinder1041,Cylinder1027]
  Placement = pos=(0,0,91) rot=(0,0,1;0rad)
FEATURE [Part::Cut] Cut372
  Base = -> Tube087
  Tool = -> Compound829
FEATURE [Part::Compound] Compound830
  Links = -> [Wedge021,Wedge023,Wedge022,Wedge020]
FEATURE [Part::Cut] Cut376
  Base = -> Tube086
  Placement = pos=(0,0,-9) rot=(0,0,1;0rad)
  Tool = -> Compound830
FEATURE [Part::Chamfer] Chamfer026
  Base = -> Cut376
  Edges = 8 edges r=1: [Edge7,Edge8,Edge21,Edge22,Edge31,Edge32,Edge45,Edge46]
FEATURE [Part::Cut] Cut375
  Base = -> Chamfer026
  Tool = -> Compound827
FEATURE [Part::Cut] Cut374
  Base = -> Cut375
  Tool = -> Compound826
FEATURE [Part::Compound] Compound831
  Links = -> [Cylinder1028,Cylinder1036,Cylinder1029,Cylinder1024]
  Placement = pos=(0,0,91) rot=(0,0,1;0rad)
FEATURE [Part::Cut] Cut373
  Base = -> Cylinder1035
  Tool = -> Compound831
FEATURE [Part::Compound] Compound828  label="J-midi_inner-planeo-m1.2-reinforced_v3"
  Links = -> [Cut377,Cut374,Cut373,Cut372]
  Placement = pos=(0,0,-4) rot=(0,0,1;0rad)
FEATURE [Part::Wedge] Wedge038  label="Klín038"
  AttacherType = Attacher::AttachEngine3D
  Placement = pos=(0,0,12) rot=(0,0,1;0rad)
  X2max = 0
  X2min = 0
  Xmax = 10
  Xmin = -10
  Ymax = 0
  Ymin = -32
  Z2max = 12
  Z2min = 0
  Zmax = 12
  Zmin = 0
FEATURE [Part::Wedge] Wedge039  label="Klín039"
  AttacherType = Attacher::AttachEngine3D
  Placement = pos=(0,0,12) rot=(0,0,1;3.14159rad)
  X2max = 0
  X2min = 0
  Xmax = 10
  Xmin = -10
  Ymax = 0
  Ymin = -32
  Z2max = 12
  Z2min = 0
  Zmax = 12
  Zmin = 0
FEATURE [Part::Cylinder] Cylinder1285  label="Válec1285"
  Angle = 360
  AttacherType = Attacher::AttachEngine3D
  Height = 20
  Placement = pos=(4,4,-88) rot=(0,0,1;3.14159rad)
  Radius = 1
FEATURE [Part::Cylinder] Cylinder1286  label="Válec1286"
  Angle = 360
  AttacherType = Attacher::AttachEngine3D
  Height = 4
  Placement = pos=(0,0,15) rot=(0,0,1;0rad)
  Radius = 7.5
FEATURE [Part::Cylinder] Cylinder1287  label="Válec1287"
  Angle = 360
  AttacherType = Attacher::AttachEngine3D
  Height = 20
  Placement = pos=(-4,4,-88) rot=(0,0,-1;1.5708rad)
  Radius = 1
FEATURE [Part::Cylinder] Cylinder1288  label="Válec1288"
  Angle = 360
  AttacherType = Attacher::AttachEngine3D
  Height = 20
  Placement = pos=(4,-4,-88) rot=(0,0,1;1.5708rad)
  Radius = 1
FEATURE [Part::Cylinder] Cylinder1289  label="Válec1289"
  Angle = 360
  AttacherType = Attacher::AttachEngine3D
  Height = 20
  Placement = pos=(-4,4,-88) rot=(0,0,-1;1.5708rad)
  Radius = 1
FEATURE [Part::Cylinder] Cylinder1290  label="Válec1290"
  Angle = 360
  AttacherType = Attacher::AttachEngine3D
  Height = 2
  Placement = pos=(-4,-4,-88) rot=(0,0,1;0rad)
  Radius = 2
FEATURE [Part::Cylinder] Cylinder1291  label="Válec1291"
  Angle = 360
  AttacherType = Attacher::AttachEngine3D
  Height = 20
  Placement = pos=(-4,-4,-88) rot=(0,0,1;0rad)
  Radius = 1
FEATURE [Part::Cylinder] Cylinder1292  label="Válec1292"
  Angle = 360
  AttacherType = Attacher::AttachEngine3D
  Height = 2
  Placement = pos=(-4,4,-88) rot=(0,0,-1;1.5708rad)
  Radius = 2
FEATURE [Part::Cylinder] Cylinder1293  label="Válec1293"
  Angle = 360
  AttacherType = Attacher::AttachEngine3D
  Height = 2
  Placement = pos=(4,4,-88) rot=(0,0,1;3.14159rad)
  Radius = 2
FEATURE [Part::Cylinder] Cylinder1294  label="Válec1294"
  Angle = 360
  AttacherType = Attacher::AttachEngine3D
  Height = 20
  Placement = pos=(4,-4,-88) rot=(0,0,1;1.5708rad)
  Radius = 1
FEATURE [Part::Cylinder] Cylinder1295  label="Válec1295"
  Angle = 360
  AttacherType = Attacher::AttachEngine3D
  Height = 20
  Placement = pos=(4,-4,-88) rot=(0,0,1;1.5708rad)
  Radius = 1
FEATURE [Part::Cylinder] Cylinder1296  label="Válec1296"
  Angle = 360
  AttacherType = Attacher::AttachEngine3D
  Height = 2
  Placement = pos=(4,-4,-88) rot=(0,0,1;1.5708rad)
  Radius = 2
FEATURE [Part::Compound] Compound929
  Links = -> [Cylinder1290,Cylinder1296,Cylinder1293,Cylinder1292]
  Placement = pos=(0,0,91) rot=(0,0,1;0rad)
FEATURE [Part::Cylinder] Cylinder1297  label="Válec1297"
  Angle = 360
  AttacherType = Attacher::AttachEngine3D
  Height = 20
  Placement = pos=(4,4,-88) rot=(0,0,1;3.14159rad)
  Radius = 1
FEATURE [Part::Cylinder] Cylinder1298  label="Válec1298"
  Angle = 360
  AttacherType = Attacher::AttachEngine3D
  Height = 20
  Placement = pos=(-4,4,-88) rot=(0,0,-1;1.5708rad)
  Radius = 1
FEATURE [Part::Compound] Compound926
  Links = -> [Cylinder1291,Cylinder1295,Cylinder1297,Cylinder1298]
  Placement = pos=(0,0,91) rot=(0,0,1;0rad)
FEATURE [Part::Cylinder] Cylinder1299  label="Válec1299"
  Angle = 360
  AttacherType = Attacher::AttachEngine3D
  Height = 20
  Placement = pos=(4,4,-88) rot=(0,0,1;3.14159rad)
  Radius = 1
FEATURE [Part::Cylinder] Cylinder1300  label="Válec1300"
  Angle = 360
  AttacherType = Attacher::AttachEngine3D
  Height = 20
  Placement = pos=(-4,-4,-88) rot=(0,0,1;0rad)
  Radius = 1
FEATURE [Part::Compound] Compound925
  Links = -> [Cylinder1300,Cylinder1288,Cylinder1285,Cylinder1287]
  Placement = pos=(0,0,91) rot=(0,0,1;0rad)
FEATURE [Part::Cylinder] Cylinder1301  label="Válec1301"
  Angle = 360
  AttacherType = Attacher::AttachEngine3D
  Height = 20
  Placement = pos=(-4,-4,-88) rot=(0,0,1;0rad)
  Radius = 1
FEATURE [Part::Compound] Compound893
  Links = -> [Cylinder1301,Cylinder1294,Cylinder1299,Cylinder1289]
  Placement = pos=(0,0,91) rot=(0,0,1;0rad)
FEATURE [Part::Cut] Cut441
  Base = -> Cylinder1286
  Tool = -> Compound893
FEATURE [Part::Cylinder] Cylinder1302  label="Válec1302"
  Angle = 360
  AttacherType = Attacher::AttachEngine3D
  Height = 60
  Placement = pos=(0,0,-10) rot=(0,0,1;0rad)
  Radius = 2.75
FEATURE [Part::Wedge] Wedge036  label="Klín036"
  AttacherType = Attacher::AttachEngine3D
  Placement = pos=(0,0,12) rot=(0,0,1;1.5708rad)
  X2max = 0
  X2min = 0
  Xmax = 10
  Xmin = -10
  Ymax = 0
  Ymin = -32
  Z2max = 12
  Z2min = 0
  Zmax = 12
  Zmin = 0
FEATURE [Part::Wedge] Wedge037  label="Klín037"
  AttacherType = Attacher::AttachEngine3D
  Placement = pos=(0,0,12) rot=(0,0,-1;1.5708rad)
  X2max = 0
  X2min = 0
  Xmax = 10
  Xmin = -10
  Ymax = 0
  Ymin = -32
  Z2max = 12
  Z2min = 0
  Zmax = 12
  Zmin = 0
FEATURE [Part::Compound] Compound928
  Links = -> [Wedge038,Wedge036,Wedge039,Wedge037]
FEATURE [Part::FeaturePython] Tube106  # WARN: FeaturePython — macro-defined, semantics opaque (R4)
  AttacherType = Attacher::AttachEngine3D
  Height = 10
  InnerRadius = 2.75
  OuterRadius = 7.5
  Placement = pos=(0,0,19) rot=(0,0,1;0rad)
FEATURE [Part::Cut] Cut440
  Base = -> Tube106
  Tool = -> Compound926
FEATURE [Part::FeaturePython] wormgear069  # WARN: FeaturePython — macro-defined, semantics opaque (R4)
  AttacherType = Attacher::AttachEngine3D
  Placement = pos=(0,0,29) rot=(0,0,1;0.994838rad)
  beta = 40.6013
  clearance = 0.25
  diameter = 21
  head = 0.25
  height = 8
  module = 1.5
  pressure_angle = 20
  reverse_pitch = false
  teeth = 12
  version = 0.0.3
FEATURE [Part::Cut] Cut442
  Base = -> wormgear069
  Tool = -> Cylinder1302
FEATURE [Part::FeaturePython] Tube113  # WARN: FeaturePython — macro-defined, semantics opaque (R4)
  AttacherType = Attacher::AttachEngine3D
  Height = 12
  InnerRadius = 3.75
  OuterRadius = 7.5
  Placement = pos=(0,0,12) rot=(0,0,1;0rad)
FEATURE [Part::Cut] Cut445
  Base = -> Tube113
  Placement = pos=(0,0,-9) rot=(0,0,1;0rad)
  Tool = -> Compound928
FEATURE [Part::Chamfer] Chamfer031
  Base = -> Cut445
  Edges = 8 edges r=1: [Edge7,Edge8,Edge21,Edge22,Edge31,Edge32,Edge45,Edge46]
FEATURE [Part::Cut] Cut444
  Base = -> Chamfer031
  Tool = -> Compound929
FEATURE [Part::Cut] Cut443
  Base = -> Cut444
  Tool = -> Compound925
FEATURE [Part::Compound] Compound927  label="J-midi-thin_inner-planeo-m1.5-reinforced_v5"
  Links = -> [Cut442,Cut443,Cut441,Cut440]
  Placement = pos=(0,0,-4) rot=(0,0,1;0rad)
FEATURE [Part::FeaturePython] wormgear034  # WARN: FeaturePython — macro-defined, semantics opaque (R4)
  AttacherType = Attacher::AttachEngine3D
  Placement = pos=(0,0,20) rot=(0,0,1;0.488692rad)
  beta = 32.7776
  clearance = 0.25
  diameter = 20.5
  head = 0
  height = 9
  module = 1.2
  pressure_angle = 20
  reverse_pitch = false
  teeth = 11
  version = 0.0.3
FEATURE [Part::FeaturePython] wormgear035  # WARN: FeaturePython — macro-defined, semantics opaque (R4)
  AttacherType = Attacher::AttachEngine3D
  Placement = pos=(0,0,29) rot=(0,0,1;0.139626rad)
  beta = 32.7776
  clearance = 0.25
  diameter = 20.5
  head = 0
  height = 8
  module = 1.2
  pressure_angle = 20
  reverse_pitch = true
  teeth = 11
  version = 0.0.3
FEATURE [Part::FeaturePython] wormgear036  # WARN: FeaturePython — macro-defined, semantics opaque (R4)
  AttacherType = Attacher::AttachEngine3D
  Placement = pos=(0,0,10) rot=(0,0,1;0.612611rad)
  beta = 31.9642
  clearance = 0.2
  diameter = 25
  head = 0
  height = 10
  module = 1.2
  pressure_angle = 25
  reverse_pitch = true
  teeth = 13
  version = 0.0.3
FEATURE [Part::Cylinder] Cylinder690  label="Válec690"
  Angle = 360
  AttacherType = Attacher::AttachEngine3D
  Height = 50
  Placement = pos=(0,0,-10) rot=(0,0,1;0rad)
  Radius = 2.55
FEATURE [Part::Cylinder] Cylinder691  label="Válec691"
  Angle = 360
  AttacherType = Attacher::AttachEngine3D
  Height = 50
  Placement = pos=(0,0,-10) rot=(0,0,1;0rad)
  Radius = 2.55
FEATURE [Part::Cylinder] Cylinder692  label="Válec692"
  Angle = 360
  AttacherType = Attacher::AttachEngine3D
  Height = 50
  Placement = pos=(0,0,-10) rot=(0,0,1;0rad)
  Radius = 2.55
FEATURE [Part::Cylinder] Cylinder693  label="Válec693"
  Angle = 360
  AttacherType = Attacher::AttachEngine3D
  Height = 50
  Placement = pos=(0,0,-10) rot=(0,0,1;0rad)
  Radius = 2.55
FEATURE [Part::Cut] Cut317
  Base = -> wormgear036
  Tool = -> Cylinder691
FEATURE [Part::Cut] Cut319
  Base = -> wormgear034
  Tool = -> Cylinder693
FEATURE [Part::Cut] Cut320
  Base = -> wormgear035
  Tool = -> Cylinder690
FEATURE [Part::FeaturePython] wormgear037  # WARN: FeaturePython — macro-defined, semantics opaque (R4)
  AttacherType = Attacher::AttachEngine3D
  Placement = pos=(0,0,0) rot=(0,0,1;0.296706rad)
  beta = 31.9642
  clearance = 0.2
  diameter = 25
  head = 0
  height = 10
  module = 1.2
  pressure_angle = 25
  reverse_pitch = false
  teeth = 13
  version = 0.0.3
FEATURE [Part::Cut] Cut318
  Base = -> wormgear037
  Tool = -> Cylinder692
FEATURE [Part::Compound] Compound695  label="J-midi_outer-planeo-m1.2"
  Links = -> [Cut318,Cut320,Cut317,Cut319]
  Placement = pos=(-19.0526,11,0) rot=(0,0,-1;1.88496rad)
FEATURE [Part::Cylinder] Cylinder1044  label="Válec1044"
  Angle = 360
  AttacherType = Attacher::AttachEngine3D
  Height = 80
  Placement = pos=(0,0,-10) rot=(0,0,1;0rad)
  Radius = 2.65
FEATURE [Part::FeaturePython] wormgear056  # WARN: FeaturePython — macro-defined, semantics opaque (R4)
  AttacherType = Attacher::AttachEngine3D
  Placement = pos=(0,0,0) rot=(0,0,1;0.296706rad)
  beta = 40.3141
  clearance = 0.2
  diameter = 24.75
  head = 0.25
  height = 10
  module = 1.5
  pressure_angle = 25
  reverse_pitch = false
  teeth = 14
  version = 0.0.3
FEATURE [Part::FeaturePython] wormgear057  # WARN: FeaturePython — macro-defined, semantics opaque (R4)
  AttacherType = Attacher::AttachEngine3D
  Placement = pos=(0,0,20) rot=(0,0,1;0.471239rad)
  beta = 39.1737
  clearance = 0.25
  diameter = 20.25
  head = 0.25
  height = 9
  module = 1.5
  pressure_angle = 20
  reverse_pitch = false
  teeth = 11
  version = 0.0.3
FEATURE [Part::FeaturePython] wormgear058  # WARN: FeaturePython — macro-defined, semantics opaque (R4)
  AttacherType = Attacher::AttachEngine3D
  Placement = pos=(0,0,10) rot=(0,0,1;0.350811rad)
  beta = 40.3141
  clearance = 0.2
  diameter = 24.75
  head = 0.25
  height = 10
  module = 1.5
  pressure_angle = 25
  reverse_pitch = true
  teeth = 14
  version = 0.0.3
FEATURE [Part::FeaturePython] wormgear059  # WARN: FeaturePython — macro-defined, semantics opaque (R4)
  AttacherType = Attacher::AttachEngine3D
  Placement = pos=(0,0,29) rot=(0,0,1;0.418879rad)
  beta = 39.1737
  clearance = 0.25
  diameter = 20.25
  head = 0.25
  height = 8
  module = 1.5
  pressure_angle = 20
  reverse_pitch = true
  teeth = 11
  version = 0.0.3
FEATURE [Part::Compound] Compound834
  Links = -> [wormgear056,wormgear059,wormgear058,wormgear057]
FEATURE [Part::Cut] Cut380  label="J-midi-thin_outer-planeo-v4"
  Base = -> Compound834
  Placement = pos=(22,0,0) rot=(0,0,1;0.226893rad)
  Tool = -> Cylinder1044
FEATURE [Part::Box] Box298  label="Krychle298"
  AttacherType = Attacher::AttachEngine3D
  Height = 40
  Length = 50
  Placement = pos=(0,0,8) rot=(0,0,1;4.18879rad)
  Width = 100
FEATURE [Part::Box] Box299  label="Krychle299"
  AttacherType = Attacher::AttachEngine3D
  Height = 40
  Length = 50
  Placement = pos=(0,0,8) rot=(0,0,1;1.36136rad)
  Width = 50
FEATURE [Part::Box] Box300  label="Krychle300"
  AttacherType = Attacher::AttachEngine3D
  Height = 40
  Length = 50
  Placement = pos=(0,0,8) rot=(0,0,1;2.61799rad)
  Width = 100
FEATURE [Part::Box] Box301  label="Krychle301"
  AttacherType = Attacher::AttachEngine3D
  Height = 40
  Length = 50
  Placement = pos=(0,0,8) rot=(0,0,-1;0.837758rad)
  Width = 50
FEATURE [Part::Cylinder] Cylinder643  label="Válec643"
  Angle = 360
  AttacherType = Attacher::AttachEngine3D
  Height = 3
  Placement = pos=(26,4,-6) rot=(0,0,1;0rad)
  Radius = 3
FEATURE [Part::Cylinder] Cylinder644  label="Válec644"
  Angle = 360
  AttacherType = Attacher::AttachEngine3D
  Height = 60
  Placement = pos=(26,4,-6) rot=(0,0,1;0rad)
  Radius = 1.48
FEATURE [Part::Cylinder] Cylinder645  label="Válec645"
  Angle = 360
  AttacherType = Attacher::AttachEngine3D
  Height = 60
  Placement = pos=(26,-4,-6) rot=(0,0,1;0rad)
  Radius = 1.48
FEATURE [Part::Cylinder] Cylinder646  label="Válec646"
  Angle = 360
  AttacherType = Attacher::AttachEngine3D
  Height = 60
  Placement = pos=(26,4,-6) rot=(0,0,1;0rad)
  Radius = 1.48
FEATURE [Part::Cylinder] Cylinder647  label="Válec647"
  Angle = 360
  AttacherType = Attacher::AttachEngine3D
  Height = 60
  Placement = pos=(26,-4,-6) rot=(0,0,1;0rad)
  Radius = 1.48
FEATURE [Part::Cylinder] Cylinder648  label="Válec648"
  Angle = 360
  AttacherType = Attacher::AttachEngine3D
  Height = 3
  Placement = pos=(26,-4,-6) rot=(0,0,1;0rad)
  Radius = 3
FEATURE [Part::Cylinder] Cylinder649  label="Válec649"
  Angle = 360
  AttacherType = Attacher::AttachEngine3D
  Height = 8
  Radius = 36
FEATURE [Part::Cylinder] Cylinder650  label="Válec650"
  Angle = 360
  AttacherType = Attacher::AttachEngine3D
  Height = 20
  Placement = pos=(0,0,-4) rot=(0,0,1;0rad)
  Radius = 12
FEATURE [Part::Cylinder] Cylinder651  label="Válec651"
  Angle = 360
  AttacherType = Attacher::AttachEngine3D
  Height = 6
  Placement = pos=(-22,0,2) rot=(0,0,1;0rad)
  Radius = 8
FEATURE [Part::Cylinder] Cylinder652  label="Válec652"
  Angle = 360
  AttacherType = Attacher::AttachEngine3D
  Height = 6
  Placement = pos=(11,-19.0526,2) rot=(0,0,1;2.0944rad)
  Radius = 8
FEATURE [Part::Cylinder] Cylinder653  label="Válec653"
  Angle = 360
  AttacherType = Attacher::AttachEngine3D
  Height = 6
  Placement = pos=(11,19.0526,2) rot=(0,0,1;4.18879rad)
  Radius = 8
FEATURE [Part::FeaturePython] Tube  # WARN: FeaturePython — macro-defined, semantics opaque (R4)
  AttacherType = Attacher::AttachEngine3D
  Height = 8
  InnerRadius = 12
  OuterRadius = 15
  Placement = pos=(0,0,-9) rot=(0,0,1;0rad)
FEATURE [Part::FeaturePython] Tube049  # WARN: FeaturePython — macro-defined, semantics opaque (R4)
  AttacherType = Attacher::AttachEngine3D
  Height = 1
  InnerRadius = 12
  OuterRadius = 20
  Placement = pos=(0,0,-1) rot=(0,0,1;0rad)
FEATURE [Part::FeaturePython] Tube050  # WARN: FeaturePython — macro-defined, semantics opaque (R4)
  AttacherType = Attacher::AttachEngine3D
  Height = 39.5
  InnerRadius = 15
  OuterRadius = 30.5
  Placement = pos=(0,0,8) rot=(0,0,1;0rad)
FEATURE [Part::FeaturePython] Tube051  # WARN: FeaturePython — macro-defined, semantics opaque (R4)
  AttacherType = Attacher::AttachEngine3D
  Height = 1
  InnerRadius = 7
  OuterRadius = 8
  Placement = pos=(-22,0,2) rot=(0,0,1;0rad)
FEATURE [Part::FeaturePython] Tube052  # WARN: FeaturePython — macro-defined, semantics opaque (R4)
  AttacherType = Attacher::AttachEngine3D
  Height = 1
  InnerRadius = 7
  OuterRadius = 8
  Placement = pos=(11,19.0526,2) rot=(0,0,1;4.18879rad)
FEATURE [Part::FeaturePython] Tube053  # WARN: FeaturePython — macro-defined, semantics opaque (R4)
  AttacherType = Attacher::AttachEngine3D
  Height = 1
  InnerRadius = 7
  OuterRadius = 8
  Placement = pos=(11,-19.0526,2) rot=(0,0,1;2.0944rad)
FEATURE [Part::Cut] Cut290
  Base = -> Tube050
  Tool = -> Box298
FEATURE [Part::Cut] Cut292
  Base = -> Cut290
  Tool = -> Box300
FEATURE [Part::Cut] Cut288
  Base = -> Cut292
  Tool = -> Box301
FEATURE [Part::Cut] Cut289
  Base = -> Cut288
  Tool = -> Box299
FEATURE [Part::Cut] Cut295
  Base = -> Cylinder649
  Tool = -> Cylinder650
FEATURE [Part::Compound] Compound669
  Links = -> [Cylinder646,Cylinder647]
  Placement = pos=(0,0,0) rot=(0,0,1;2.0944rad)
FEATURE [Part::Compound] Compound670
  Links = -> [Cylinder643,Cylinder648]
  Placement = pos=(0,0,6) rot=(0,0,1;2.0944rad)
FEATURE [Part::Compound] Compound671
  Links = -> [Cylinder646,Cylinder647]
FEATURE [Part::Compound] Compound672
  Links = -> [Cylinder646,Cylinder647]
  Placement = pos=(0,0,0) rot=(0,0,1;4.18879rad)
FEATURE [Part::Compound] Compound673
  Links = -> [Cylinder644,Cylinder645]
  Placement = pos=(0,0,0) rot=(0,0,1;1.0472rad)
FEATURE [Part::Cut] Cut291
  Base = -> Cut289
  Placement = pos=(0,0,0) rot=(0,0,1;1.0472rad)
  Tool = -> Compound673
FEATURE [Part::Cut] Cut294
  Base = -> Cut289
  Placement = pos=(0,0,0) rot=(0,0,-1;1.0472rad)
  Tool = -> Compound673
FEATURE [Part::Cut] Cut298
  Base = -> Cut289
  Placement = pos=(0,0,0) rot=(0,0,1;3.14159rad)
  Tool = -> Compound673
FEATURE [Part::Compound] Compound674
  Links = -> [Cylinder643,Cylinder648]
  Placement = pos=(0,0,6) rot=(0,0,1;4.18879rad)
FEATURE [Part::Compound] Compound675
  Links = -> [Cylinder643,Cylinder648]
  Placement = pos=(0,0,6) rot=(0,0,1;0rad)
FEATURE [Part::Compound] Compound668
  Links = -> [Compound670,Compound674,Compound675]
FEATURE [Part::Compound] Compound676
  Links = -> [Compound669,Compound672,Compound671]
FEATURE [Part::Compound] Compound677
  Links = -> [Cylinder651,Cylinder652,Cylinder653]
FEATURE [Part::Cut] Cut296
  Base = -> Cut295
  Tool = -> Compound677
FEATURE [Part::Cut] Cut297
  Base = -> Cut296
  Tool = -> Compound668
FEATURE [Part::Cut] Cut293
  Base = -> Cut297
  Tool = -> Compound676
FEATURE [Part::Compound] Compound678
  Links = -> [Cut294,Cut298,Cut291]
FEATURE [Part::Compound] Compound680
  Links = -> [Tube053,Tube052,Tube051]
FEATURE [Part::Compound] Compound679  label="J-midi_pikovina001"
  Links = -> [Compound678,Cut293,Compound680]
FEATURE [Part::Compound] Compound681  label="J-midi_pikovina_fixo1"
  Links = -> [Tube,Tube049,Compound679]
FEATURE [Part::Chamfer] Chamfer032  label="auxi2"
  Base = -> Compound681
  Edges = 1 edges r=1: [Edge3]
FEATURE [Part::FeaturePython] Tube045  # WARN: FeaturePython — macro-defined, semantics opaque (R4)
  AttacherType = Attacher::AttachEngine3D
  Height = 1
  InnerRadius = 7
  OuterRadius = 8
  Placement = pos=(-22,0,2) rot=(0,0,1;0rad)
FEATURE [Part::FeaturePython] Tube046  # WARN: FeaturePython — macro-defined, semantics opaque (R4)
  AttacherType = Attacher::AttachEngine3D
  Height = 1
  InnerRadius = 7
  OuterRadius = 8
  Placement = pos=(11,-19.0526,2) rot=(0,0,1;2.0944rad)
FEATURE [Part::FeaturePython] Tube047  # WARN: FeaturePython — macro-defined, semantics opaque (R4)
  AttacherType = Attacher::AttachEngine3D
  Height = 1
  InnerRadius = 7
  OuterRadius = 8
  Placement = pos=(0,0,2) rot=(0,0,1;4.18879rad)
FEATURE [Part::FeaturePython] Tube048  # WARN: FeaturePython — macro-defined, semantics opaque (R4)
  AttacherType = Attacher::AttachEngine3D
  Height = 1
  InnerRadius = 7
  OuterRadius = 8
  Placement = pos=(11,19.0526,2) rot=(0,0,1;4.18879rad)
FEATURE [Part::Cylinder] Cylinder632  label="Válec632"
  Angle = 360
  AttacherType = Attacher::AttachEngine3D
  Height = 6
  Placement = pos=(11,19.0526,2) rot=(0,0,1;4.18879rad)
  Radius = 8
FEATURE [Part::Cylinder] Cylinder633  label="Válec633"
  Angle = 360
  AttacherType = Attacher::AttachEngine3D
  Height = 6
  Placement = pos=(-22,0,2) rot=(0,0,1;0rad)
  Radius = 8
FEATURE [Part::Cylinder] Cylinder634  label="Válec634"
  Angle = 360
  AttacherType = Attacher::AttachEngine3D
  Height = 6
  Placement = pos=(11,-19.0526,2) rot=(0,0,1;2.0944rad)
  Radius = 8
FEATURE [Part::Cylinder] Cylinder635  label="Válec635"
  Angle = 360
  AttacherType = Attacher::AttachEngine3D
  Height = 8
  Radius = 36
FEATURE [Part::Cylinder] Cylinder636  label="Válec636"
  Angle = 360
  AttacherType = Attacher::AttachEngine3D
  Height = 6
  Placement = pos=(0,0,2) rot=(0,0,1;0rad)
  Radius = 8
FEATURE [Part::Cylinder] Cylinder637  label="Válec637"
  Angle = 360
  AttacherType = Attacher::AttachEngine3D
  Height = 3
  Placement = pos=(26,-4,-6) rot=(0,0,1;0rad)
  Radius = 3
FEATURE [Part::Cylinder] Cylinder638  label="Válec638"
  Angle = 360
  AttacherType = Attacher::AttachEngine3D
  Height = 60
  Placement = pos=(26,4,-6) rot=(0,0,1;0rad)
  Radius = 1.5
FEATURE [Part::Cylinder] Cylinder639  label="Válec639"
  Angle = 360
  AttacherType = Attacher::AttachEngine3D
  Height = 60
  Placement = pos=(26,-4,-6) rot=(0,0,1;0rad)
  Radius = 1.5
FEATURE [Part::Compound] Compound657
  Links = -> [Cylinder638,Cylinder639]
  Placement = pos=(0,0,0) rot=(0,0,1;2.0944rad)
FEATURE [Part::Cylinder] Cylinder640  label="Válec640"
  Angle = 360
  AttacherType = Attacher::AttachEngine3D
  Height = 3
  Placement = pos=(26,4,-6) rot=(0,0,1;0rad)
  Radius = 3
FEATURE [Part::Compound] Compound658
  Links = -> [Cylinder640,Cylinder637]
  Placement = pos=(0,0,6) rot=(0,0,1;2.0944rad)
FEATURE [Part::Cylinder] Cylinder641  label="Válec641"
  Angle = 360
  AttacherType = Attacher::AttachEngine3D
  Height = 1
  Placement = pos=(0,0,-1) rot=(0,0,1;0rad)
  Radius = 10
FEATURE [Part::Cylinder] Cylinder642  label="Válec642"
  Angle = 360
  AttacherType = Attacher::AttachEngine3D
  Height = 8
  Placement = pos=(0,0,-9) rot=(0,0,1;0rad)
  Radius = 7.5
FEATURE [Part::Chamfer] Chamfer033
  Base = -> Cylinder642
  Edges = 1 edges r=1: [Edge3]
FEATURE [Part::Compound] Compound659
  Links = -> [Cylinder638,Cylinder639]
  Placement = pos=(0,0,0) rot=(0,0,1;4.18879rad)
FEATURE [Part::Compound] Compound660
  Links = -> [Cylinder638,Cylinder639]
FEATURE [Part::Compound] Compound661
  Links = -> [Compound657,Compound659,Compound660]
FEATURE [Part::Compound] Compound663
  Links = -> [Cylinder640,Cylinder637]
  Placement = pos=(0,0,6) rot=(0,0,1;0rad)
FEATURE [Part::Compound] Compound665
  Links = -> [Cylinder640,Cylinder637]
  Placement = pos=(0,0,6) rot=(0,0,1;4.18879rad)
FEATURE [Part::Compound] Compound664
  Links = -> [Compound658,Compound665,Compound663]
FEATURE [Part::Compound] Compound666
  Links = -> [Cylinder633,Cylinder634,Cylinder632,Cylinder636]
FEATURE [Part::Cut] Cut287
  Base = -> Cylinder635
  Tool = -> Compound666
FEATURE [Part::Cut] Cut286
  Base = -> Cut287
  Tool = -> Compound661
FEATURE [Part::Cut] Cut285
  Base = -> Cut286
  Tool = -> Compound664
FEATURE [Part::Compound] Compound662  label="J-midi_quikovina_fixo2"
  Links = -> [Tube045,Tube047,Tube046,Tube048,Cut285]
FEATURE [Part::Compound] Compound667  label="auxi1"
  Links = -> [Chamfer033,Cylinder641,Compound662]
  Placement = pos=(0,0,100) rot=(0,0,1;0rad)
FEATURE [Part::Chamfer] Chamfer  label="J-midi-thin_quikovina_fixo"
  Base = -> Compound667
  Edges = 1 edges r=2: [Edge35]
FEATURE [Part::Chamfer] Chamfer034  label="J-midi-thin_pikovina_fixo"
  Base = -> Chamfer032
  Edges = 1 edges r=2: [Edge71]
FEATURE [Part::Cylinder] Cylinder1303  label="Válec1303"
  Angle = 360
  AttacherType = Attacher::AttachEngine3D
  Height = 32
  Placement = pos=(-29.6985,-29.6985,33.5) rot=(0,0,-1;0.785398rad)
  Radius = 1.5
FEATURE [Part::Cylinder] Cylinder1304  label="Válec1304"
  Angle = 360
  AttacherType = Attacher::AttachEngine3D
  Height = 32
  Placement = pos=(-29.6985,29.6985,33.5) rot=(0,0,1;3.92699rad)
  Radius = 1.5
FEATURE [Part::Box] Box544  label="Krychle544"
  AttacherType = Attacher::AttachEngine3D
  Height = 2
  Length = 6
  Placement = pos=(-34.6482,-30.4056,33) rot=(0,0,-1;0.785398rad)
  Width = 8
FEATURE [Part::Box] Box545  label="Krychle545"
  AttacherType = Attacher::AttachEngine3D
  Height = 2
  Length = 6
  Placement = pos=(-3,-46,33) rot=(0,0,1;0rad)
  Width = 8
FEATURE [Part::Box] Box546  label="Krychle546"
  AttacherType = Attacher::AttachEngine3D
  Height = 2
  Length = 6
  Placement = pos=(46,-3,33) rot=(0,0,1;1.5708rad)
  Width = 8
FEATURE [Part::Box] Box547  label="Krychle547"
  AttacherType = Attacher::AttachEngine3D
  Height = 2
  Length = 6
  Placement = pos=(-30.4056,34.6482,33) rot=(0,0,1;3.92699rad)
  Width = 8
FEATURE [Part::Cylinder] Cylinder1305  label="Válec1305"
  Angle = 360
  AttacherType = Attacher::AttachEngine3D
  Height = 32
  Placement = pos=(0,-42,33.5) rot=(0,0,1;0rad)
  Radius = 1.5
FEATURE [Part::Cylinder] Cylinder1306  label="Válec1306"
  Angle = 360
  AttacherType = Attacher::AttachEngine3D
  Height = 32
  Placement = pos=(-1.4e-14,42,33.5) rot=(0,0,1;3.14159rad)
  Radius = 1.5
FEATURE [Part::Box] Box548  label="Krychle548"
  AttacherType = Attacher::AttachEngine3D
  Height = 2
  Length = 6
  Placement = pos=(30.4056,-34.6482,33) rot=(0,0,1;0.785398rad)
  Width = 8
FEATURE [Part::Box] Box549  label="Krychle549"
  AttacherType = Attacher::AttachEngine3D
  Height = 2
  Length = 6
  Placement = pos=(34.6482,30.4056,33) rot=(0,0,1;2.35619rad)
  Width = 8
FEATURE [Part::Cylinder] Cylinder1307  label="Válec1307"
  Angle = 360
  AttacherType = Attacher::AttachEngine3D
  Height = 32
  Placement = pos=(29.6985,-29.6985,33.5) rot=(0,0,1;0.785398rad)
  Radius = 1.5
FEATURE [Part::Cylinder] Cylinder1308  label="Válec1308"
  Angle = 360
  AttacherType = Attacher::AttachEngine3D
  Height = 32
  Placement = pos=(29.6985,29.6985,33.5) rot=(0,0,1;2.35619rad)
  Radius = 1.5
FEATURE [Part::Cylinder] Cylinder1309  label="Válec1309"
  Angle = 360
  AttacherType = Attacher::AttachEngine3D
  Height = 32
  Placement = pos=(-42,-2.4e-14,33.5) rot=(0,0,-1;1.5708rad)
  Radius = 1.5
FEATURE [Part::Cylinder] Cylinder1310  label="Válec1310"
  Angle = 360
  AttacherType = Attacher::AttachEngine3D
  Height = 32
  Placement = pos=(42,6e-15,33.5) rot=(0,0,1;1.5708rad)
  Radius = 1.5
FEATURE [Part::Box] Box550  label="Krychle550"
  AttacherType = Attacher::AttachEngine3D
  Height = 2
  Length = 6
  Placement = pos=(3,46,33) rot=(0,0,1;3.14159rad)
  Width = 8
FEATURE [Part::Box] Box551  label="Krychle551"
  AttacherType = Attacher::AttachEngine3D
  Height = 2
  Length = 6
  Placement = pos=(-46,3,33) rot=(0,0,-1;1.5708rad)
  Width = 8
FEATURE [Part::Compound] Compound930
  Links = -> [Box544,Box548,Box546,Box545,Box549,Box550,Box547,Box551]
  Placement = pos=(0,0,4.4) rot=(0,0,1;0.392699rad)
FEATURE [Part::Compound] Compound931
  Links = -> [Cylinder1305,Cylinder1307,Cylinder1310,Cylinder1308,Cylinder1306,Cylinder1304,Cylinder1309,Cylinder1303]
  Placement = pos=(0,0,0) rot=(0,0,1;0.392699rad)
FEATURE [Part::FeaturePython] Tube114  # WARN: FeaturePython — macro-defined, semantics opaque (R4)
  AttacherType = Attacher::AttachEngine3D
  Height = 16
  InnerRadius = 40
  OuterRadius = 46
  Placement = pos=(0,0,26) rot=(0,0,1;0rad)
FEATURE [Part::FeaturePython] Tube115  label="ZKL-61816-5"  # WARN: FeaturePython — macro-defined, semantics opaque (R4)
  AttacherType = Attacher::AttachEngine3D
  Height = 11
  InnerRadius = 40
  OuterRadius = 50
  Placement = pos=(0,0,25.4) rot=(0,0,1;0rad)
FEATURE [Part::Box] Box560  label="Krychle560"
  AttacherType = Attacher::AttachEngine3D
  Height = 2
  Length = 6
  Placement = pos=(3,46,33) rot=(0,0,1;3.14159rad)
  Width = 8
FEATURE [Part::Box] Box561  label="Krychle561"
  AttacherType = Attacher::AttachEngine3D
  Height = 2
  Length = 6
  Placement = pos=(30.4056,-34.6482,33) rot=(0,0,1;0.785398rad)
  Width = 8
FEATURE [Part::Cylinder] Cylinder1311  label="Válec1311"
  Angle = 360
  AttacherType = Attacher::AttachEngine3D
  Height = 8
  Radius = 40
FEATURE [Part::Box] Box562  label="Krychle562"
  AttacherType = Attacher::AttachEngine3D
  Height = 2
  Length = 6
  Placement = pos=(-34.6482,-30.4056,33) rot=(0,0,-1;0.785398rad)
  Width = 8
FEATURE [Part::Box] Box563  label="Krychle563"
  AttacherType = Attacher::AttachEngine3D
  Height = 2
  Length = 6
  Placement = pos=(34.6482,30.4056,33) rot=(0,0,1;2.35619rad)
  Width = 8
FEATURE [Part::Box] Box564  label="Krychle564"
  AttacherType = Attacher::AttachEngine3D
  Height = 2
  Length = 6
  Placement = pos=(-3,-46,33) rot=(0,0,1;0rad)
  Width = 8
FEATURE [Part::Box] Box565  label="Krychle565"
  AttacherType = Attacher::AttachEngine3D
  Height = 2
  Length = 6
  Placement = pos=(-30.4056,34.6482,33) rot=(0,0,1;3.92699rad)
  Width = 8
FEATURE [Part::Cylinder] Cylinder1312  label="Válec1312"
  Angle = 360
  AttacherType = Attacher::AttachEngine3D
  Height = 8
  Radius = 40
FEATURE [Part::Box] Box566  label="Krychle566"
  AttacherType = Attacher::AttachEngine3D
  Height = 2
  Length = 6
  Placement = pos=(-46,3,33) rot=(0,0,-1;1.5708rad)
  Width = 8
FEATURE [Part::Box] Box567  label="Krychle567"
  AttacherType = Attacher::AttachEngine3D
  Height = 2
  Length = 6
  Placement = pos=(46,-3,33) rot=(0,0,1;1.5708rad)
  Width = 8
FEATURE [Part::Compound] Compound932
  Links = -> [Box562,Box561,Box567,Box564,Box563,Box560,Box565,Box566]
  Placement = pos=(0,0,3.4) rot=(0,0,1;0.392699rad)
FEATURE [Part::Cut] Cut473
  Base = -> Tube114
  Tool = -> Tube115
FEATURE [Part::Cut] Cut475
  Base = -> Cut473
  Tool = -> Compound931
FEATURE [Part::Cut] Cut476
  Base = -> Cut475
  Placement = pos=(0,0,3) rot=(0,0,1;0rad)
  Tool = -> Compound930
FEATURE [Part::FeaturePython] wormgear070  # WARN: FeaturePython — macro-defined, semantics opaque (R4)
  AttacherType = Attacher::AttachEngine3D
  Placement = pos=(0,0,0) rot=(0,0,1;0.10472rad)
  beta = 38.7636
  clearance = 0.25
  diameter = 67.25
  head = 0
  height = 14
  module = 1.5
  pressure_angle = 20
  reverse_pitch = true
  teeth = 36
  version = 0.0.3
FEATURE [Part::Cut] Cut471
  Base = -> Cylinder1312
  Placement = pos=(0,0,33) rot=(0,0,1;0.53058rad)
  Tool = -> wormgear070
FEATURE [Part::Cut] Cut472
  Base = -> Cut471
  Tool = -> Compound932
FEATURE [Part::FeaturePython] wormgear071  # WARN: FeaturePython — macro-defined, semantics opaque (R4)
  AttacherType = Attacher::AttachEngine3D
  Placement = pos=(0,0,0) rot=(0,0,-1;0.1309rad)
  beta = 38.7636
  clearance = 0.25
  diameter = 67.25
  head = 0
  height = 14
  module = 1.5
  pressure_angle = 20
  reverse_pitch = false
  teeth = 36
  version = 0.0.3
FEATURE [Part::Cut] Cut470
  Base = -> Cylinder1311
  Placement = pos=(0,0,25) rot=(0,0,1;0.294961rad)
  Tool = -> wormgear071
FEATURE [Part::Compound] Compound933
  Links = -> [Cut472,Cut470]
  Placement = pos=(0,0,4) rot=(0,0,1;0rad)
FEATURE [Part::FeaturePython] Tube116  label="ZKL-61816-6"  # WARN: FeaturePython — macro-defined, semantics opaque (R4)
  AttacherType = Attacher::AttachEngine3D
  Height = 11
  InnerRadius = 40
  OuterRadius = 50
  Placement = pos=(0,0,25) rot=(0,0,1;0rad)
FEATURE [Part::Cut] Cut474
  Base = -> Compound933
  Tool = -> Tube116
FEATURE [Part::Torus] Torus006  label="Anuloid006"
  Angle1 = -180
  Angle2 = 180
  Angle3 = 360
  AttacherType = Attacher::AttachEngine3D
  Placement = pos=(0,0,29) rot=(0,0,1;0rad)
  Radius1 = 46
  Radius2 = 3.1
FEATURE [Part::Box] Box310  label="Krychle310"
  AttacherType = Attacher::AttachEngine3D
  Height = 2
  Length = 6
  Placement = pos=(30.4056,-34.6482,33) rot=(0,0,1;0.785398rad)
  Width = 8
FEATURE [Part::Cylinder] Cylinder694  label="Válec694"
  Angle = 360
  AttacherType = Attacher::AttachEngine3D
  Height = 20
  Placement = pos=(-46.3,0,29) rot=(0,0,1;0rad)
  Radius = 3.5
FEATURE [Part::Box] Box311  label="Krychle311"
  AttacherType = Attacher::AttachEngine3D
  Height = 2
  Length = 6
  Placement = pos=(3,46,33) rot=(0,0,1;3.14159rad)
  Width = 8
FEATURE [Part::Box] Box312  label="Krychle312"
  AttacherType = Attacher::AttachEngine3D
  Height = 2
  Length = 6
  Placement = pos=(-3,-46,33) rot=(0,0,1;0rad)
  Width = 8
FEATURE [Part::Cylinder] Cylinder695  label="Válec695"
  Angle = 360
  AttacherType = Attacher::AttachEngine3D
  Height = 8
  Radius = 40
FEATURE [Part::Cylinder] Cylinder696  label="Válec696"
  Angle = 360
  AttacherType = Attacher::AttachEngine3D
  Height = 8
  Radius = 40
FEATURE [Part::Box] Box313  label="Krychle313"
  AttacherType = Attacher::AttachEngine3D
  Height = 2
  Length = 6
  Placement = pos=(-46,3,33) rot=(0,0,-1;1.5708rad)
  Width = 8
FEATURE [Part::Box] Box314  label="Krychle314"
  AttacherType = Attacher::AttachEngine3D
  Height = 2
  Length = 6
  Placement = pos=(-3,-46,33) rot=(0,0,1;0rad)
  Width = 8
FEATURE [Part::Box] Box315  label="Krychle315"
  AttacherType = Attacher::AttachEngine3D
  Height = 2
  Length = 6
  Placement = pos=(-46,3,33) rot=(0,0,-1;1.5708rad)
  Width = 8
FEATURE [Part::Box] Box316  label="Krychle316"
  AttacherType = Attacher::AttachEngine3D
  Height = 2
  Length = 6
  Placement = pos=(-34.6482,-30.4056,33) rot=(0,0,-1;0.785398rad)
  Width = 8
FEATURE [Part::Box] Box317  label="Krychle317"
  AttacherType = Attacher::AttachEngine3D
  Height = 2
  Length = 6
  Placement = pos=(46,-3,33) rot=(0,0,1;1.5708rad)
  Width = 8
FEATURE [Part::Box] Box318  label="Krychle318"
  AttacherType = Attacher::AttachEngine3D
  Height = 2
  Length = 6
  Placement = pos=(34.6482,30.4056,33) rot=(0,0,1;2.35619rad)
  Width = 8
FEATURE [Part::Box] Box319  label="Krychle319"
  AttacherType = Attacher::AttachEngine3D
  Height = 2
  Length = 6
  Placement = pos=(30.4056,-34.6482,33) rot=(0,0,1;0.785398rad)
  Width = 8
FEATURE [Part::Box] Box320  label="Krychle320"
  AttacherType = Attacher::AttachEngine3D
  Height = 2
  Length = 6
  Placement = pos=(-30.4056,34.6482,33) rot=(0,0,1;3.92699rad)
  Width = 8
FEATURE [Part::Compound] Compound697
  Links = -> [Box316,Box310,Box317,Box314,Box318,Box311,Box320,Box313]
  Placement = pos=(0,0,0) rot=(0,0,1;0.392699rad)
FEATURE [Part::Box] Box321  label="Krychle321"
  AttacherType = Attacher::AttachEngine3D
  Height = 2
  Length = 6
  Placement = pos=(46,-3,33) rot=(0,0,1;1.5708rad)
  Width = 8
FEATURE [Part::Box] Box322  label="Krychle322"
  AttacherType = Attacher::AttachEngine3D
  Height = 2
  Length = 6
  Placement = pos=(3,46,33) rot=(0,0,1;3.14159rad)
  Width = 8
FEATURE [Part::Cylinder] Cylinder697  label="Válec697"
  Angle = 360
  AttacherType = Attacher::AttachEngine3D
  Height = 20
  Placement = pos=(-46.3,0,29) rot=(0,0,1;0rad)
  Radius = 3.5
FEATURE [Part::Cylinder] Cylinder698  label="Válec698"
  Angle = 360
  AttacherType = Attacher::AttachEngine3D
  Height = 12
  Placement = pos=(-29.6985,-29.6985,33.5) rot=(0,0,-1;0.785398rad)
  Radius = 1.5
FEATURE [Part::Cylinder] Cylinder699  label="Válec699"
  Angle = 360
  AttacherType = Attacher::AttachEngine3D
  Height = 12
  Placement = pos=(-29.6985,-29.6985,33.5) rot=(0,0,-1;0.785398rad)
  Radius = 1.5
FEATURE [Part::Cylinder] Cylinder700  label="Válec700"
  Angle = 360
  AttacherType = Attacher::AttachEngine3D
  Height = 12
  Placement = pos=(29.6985,-29.6985,33.5) rot=(0,0,1;0.785398rad)
  Radius = 1.5
FEATURE [Part::Box] Box323  label="Krychle323"
  AttacherType = Attacher::AttachEngine3D
  Height = 2
  Length = 6
  Placement = pos=(-34.6482,-30.4056,33) rot=(0,0,-1;0.785398rad)
  Width = 8
FEATURE [Part::Cylinder] Cylinder701  label="Válec701"
  Angle = 360
  AttacherType = Attacher::AttachEngine3D
  Height = 12
  Placement = pos=(0,-42,33.5) rot=(0,0,1;0rad)
  Radius = 1.5
FEATURE [Part::Cylinder] Cylinder702  label="Válec702"
  Angle = 360
  AttacherType = Attacher::AttachEngine3D
  Height = 12
  Placement = pos=(0,-42,33.5) rot=(0,0,1;0rad)
  Radius = 1.5
FEATURE [Part::Cylinder] Cylinder703  label="Válec703"
  Angle = 360
  AttacherType = Attacher::AttachEngine3D
  Height = 12
  Placement = pos=(-1.4e-14,42,33.5) rot=(0,0,1;3.14159rad)
  Radius = 1.5
FEATURE [Part::Cylinder] Cylinder704  label="Válec704"
  Angle = 360
  AttacherType = Attacher::AttachEngine3D
  Height = 12
  Placement = pos=(-42,-2.4e-14,33.5) rot=(0,0,-1;1.5708rad)
  Radius = 1.5
FEATURE [Part::Cylinder] Cylinder705  label="Válec705"
  Angle = 360
  AttacherType = Attacher::AttachEngine3D
  Height = 12
  Placement = pos=(-1.4e-14,42,33.5) rot=(0,0,1;3.14159rad)
  Radius = 1.5
FEATURE [Part::Box] Box324  label="Krychle324"
  AttacherType = Attacher::AttachEngine3D
  Height = 2
  Length = 6
  Placement = pos=(34.6482,30.4056,33) rot=(0,0,1;2.35619rad)
  Width = 8
FEATURE [Part::Cylinder] Cylinder706  label="Válec706"
  Angle = 360
  AttacherType = Attacher::AttachEngine3D
  Height = 12
  Placement = pos=(29.6985,29.6985,33.5) rot=(0,0,1;2.35619rad)
  Radius = 1.5
FEATURE [Part::FeaturePython] wormgear038  # WARN: FeaturePython — macro-defined, semantics opaque (R4)
  AttacherType = Attacher::AttachEngine3D
  Placement = pos=(0,0,0) rot=(0,0,-1;0.1309rad)
  beta = 33.2066
  clearance = 0.25
  diameter = 66
  head = 0
  height = 10
  module = 1.2
  pressure_angle = 20
  reverse_pitch = false
  teeth = 36
  version = 0.0.3
FEATURE [Part::FeaturePython] Tube075  # WARN: FeaturePython — macro-defined, semantics opaque (R4)
  AttacherType = Attacher::AttachEngine3D
  Height = 16
  InnerRadius = 40
  OuterRadius = 46
  Placement = pos=(0,0,21) rot=(0,0,1;0rad)
FEATURE [Part::FeaturePython] wormgear039  # WARN: FeaturePython — macro-defined, semantics opaque (R4)
  AttacherType = Attacher::AttachEngine3D
  Placement = pos=(0,0,0) rot=(0,0,1;0.10472rad)
  beta = 33.2066
  clearance = 0.25
  diameter = 66
  head = 0
  height = 10
  module = 1.2
  pressure_angle = 20
  reverse_pitch = true
  teeth = 36
  version = 0.0.3
FEATURE [Part::FeaturePython] Tube076  # WARN: FeaturePython — macro-defined, semantics opaque (R4)
  AttacherType = Attacher::AttachEngine3D
  Height = 1
  InnerRadius = 36
  OuterRadius = 46
  Placement = pos=(0,0,37) rot=(0,0,1;0rad)
FEATURE [Part::Box] Box325  label="Krychle325"
  AttacherType = Attacher::AttachEngine3D
  Height = 2
  Length = 6
  Placement = pos=(-34.6482,-30.4056,33) rot=(0,0,-1;0.785398rad)
  Width = 8
FEATURE [Part::Box] Box326  label="Krychle326"
  AttacherType = Attacher::AttachEngine3D
  Height = 2
  Length = 6
  Placement = pos=(-30.4056,34.6482,33) rot=(0,0,1;3.92699rad)
  Width = 8
FEATURE [Part::Compound] Compound700
  Links = -> [Box325,Box319,Box321,Box312,Box324,Box322,Box326,Box315]
  Placement = pos=(0,0,0) rot=(0,0,1;0.392699rad)
FEATURE [Part::Cylinder] Cylinder707  label="Válec707"
  Angle = 360
  AttacherType = Attacher::AttachEngine3D
  Height = 12
  Placement = pos=(-29.6985,29.6985,33.5) rot=(0,0,1;3.92699rad)
  Radius = 1.5
FEATURE [Part::Cylinder] Cylinder708  label="Válec708"
  Angle = 360
  AttacherType = Attacher::AttachEngine3D
  Height = 12
  Placement = pos=(42,6e-15,33.5) rot=(0,0,1;1.5708rad)
  Radius = 1.5
FEATURE [Part::Compound] Compound701
  Links = -> [Cylinder702,Cylinder700,Cylinder708,Cylinder706,Cylinder705,Cylinder707,Cylinder704,Cylinder699]
  Placement = pos=(0,0,0) rot=(0,0,1;0.392699rad)
FEATURE [Part::Box] Box327  label="Krychle327"
  AttacherType = Attacher::AttachEngine3D
  Height = 2
  Length = 6
  Placement = pos=(-30.4056,34.6482,33) rot=(0,0,1;3.92699rad)
  Width = 8
FEATURE [Part::Box] Box328  label="Krychle328"
  AttacherType = Attacher::AttachEngine3D
  Height = 2
  Length = 6
  Placement = pos=(-3,-46,33) rot=(0,0,1;0rad)
  Width = 8
FEATURE [Part::Box] Box329  label="Krychle329"
  AttacherType = Attacher::AttachEngine3D
  Height = 2
  Length = 6
  Placement = pos=(46,-3,33) rot=(0,0,1;1.5708rad)
  Width = 8
FEATURE [Part::Cylinder] Cylinder709  label="Válec709"
  Angle = 360
  AttacherType = Attacher::AttachEngine3D
  Height = 12
  Placement = pos=(-29.6985,29.6985,33.5) rot=(0,0,1;3.92699rad)
  Radius = 1.5
FEATURE [Part::Box] Box330  label="Krychle330"
  AttacherType = Attacher::AttachEngine3D
  Height = 2
  Length = 6
  Placement = pos=(-46,3,33) rot=(0,0,-1;1.5708rad)
  Width = 8
FEATURE [Part::Box] Box331  label="Krychle331"
  AttacherType = Attacher::AttachEngine3D
  Height = 2
  Length = 6
  Placement = pos=(30.4056,-34.6482,33) rot=(0,0,1;0.785398rad)
  Width = 8
FEATURE [Part::Cylinder] Cylinder710  label="Válec710"
  Angle = 360
  AttacherType = Attacher::AttachEngine3D
  Height = 12
  Placement = pos=(-42,-2.4e-14,33.5) rot=(0,0,-1;1.5708rad)
  Radius = 1.5
FEATURE [Part::Box] Box332  label="Krychle332"
  AttacherType = Attacher::AttachEngine3D
  Height = 2
  Length = 6
  Placement = pos=(3,46,33) rot=(0,0,1;3.14159rad)
  Width = 8
FEATURE [Part::Cylinder] Cylinder711  label="Válec711"
  Angle = 360
  AttacherType = Attacher::AttachEngine3D
  Height = 12
  Placement = pos=(29.6985,29.6985,33.5) rot=(0,0,1;2.35619rad)
  Radius = 1.5
FEATURE [Part::Box] Box333  label="Krychle333"
  AttacherType = Attacher::AttachEngine3D
  Height = 2
  Length = 6
  Placement = pos=(34.6482,30.4056,33) rot=(0,0,1;2.35619rad)
  Width = 8
FEATURE [Part::Compound] Compound696
  Links = -> [Box323,Box331,Box329,Box328,Box333,Box332,Box327,Box330]
  Placement = pos=(0,0,0) rot=(0,0,1;0.392699rad)
FEATURE [Part::Cylinder] Cylinder712  label="Válec712"
  Angle = 360
  AttacherType = Attacher::AttachEngine3D
  Height = 12
  Placement = pos=(42,6e-15,33.5) rot=(0,0,1;1.5708rad)
  Radius = 1.5
FEATURE [Part::Cylinder] Cylinder713  label="Válec713"
  Angle = 360
  AttacherType = Attacher::AttachEngine3D
  Height = 12
  Placement = pos=(29.6985,-29.6985,33.5) rot=(0,0,1;0.785398rad)
  Radius = 1.5
FEATURE [Part::Compound] Compound698
  Links = -> [Cylinder701,Cylinder713,Cylinder712,Cylinder711,Cylinder703,Cylinder709,Cylinder710,Cylinder698]
  Placement = pos=(0,0,0) rot=(0,0,1;0.392699rad)
FEATURE [Part::Cut] Cut322
  Base = -> Cylinder695
  Placement = pos=(0,0,29) rot=(0,0,1;0.392699rad)
  Tool = -> wormgear039
FEATURE [Part::Cut] Cut323
  Base = -> Tube076
  Tool = -> Cylinder697
FEATURE [Part::Cut] Cut324
  Base = -> Cylinder696
  Placement = pos=(0,0,21) rot=(0,0,1;0.258309rad)
  Tool = -> wormgear038
FEATURE [Part::Cut] Cut325
  Base = -> Tube075
  Tool = -> Torus006
FEATURE [Part::Cut] Cut326
  Base = -> Cut325
  Tool = -> Cylinder694
FEATURE [Part::Cut] Cut327
  Base = -> Cut322
  Tool = -> Compound697
FEATURE [Part::Compound] Compound699
  Links = -> [Cut327,Cut324]
FEATURE [Part::Cut] Cut328
  Base = -> Cut326
  Tool = -> Compound698
FEATURE [Part::Cut] Cut329
  Base = -> Cut328
  Tool = -> Compound696
FEATURE [Part::Cut] Cut330
  Base = -> Cut323
  Tool = -> Compound701
FEATURE [Part::Cut] Cut321
  Base = -> Cut330
  Tool = -> Compound700
FEATURE [Part::Compound] Compound702  label="J-midi_rybovina-podlozena-m1.2"
  Links = -> [Cut329,Cut321,Compound699]
  Placement = pos=(0,0,11) rot=(0,0,1;0rad)
FEATURE [Part::FeaturePython] Tube117  label="ZKL-61816-subwasher"  # WARN: FeaturePython — macro-defined, semantics opaque (R4)
  AttacherType = Attacher::AttachEngine3D
  Height = 0.4
  InnerRadius = 40
  OuterRadius = 42
  Placement = pos=(0,0,38) rot=(0,0,1;0rad)
FEATURE [Part::Cylinder] Cylinder1313  label="Válec1313"
  Angle = 360
  AttacherType = Attacher::AttachEngine3D
  Height = 32
  Placement = pos=(-29.6985,-29.6985,33.5) rot=(0,0,-1;0.785398rad)
  Radius = 1.5
FEATURE [Part::Cylinder] Cylinder1314  label="Válec1314"
  Angle = 360
  AttacherType = Attacher::AttachEngine3D
  Height = 32
  Placement = pos=(-29.6985,29.6985,33.5) rot=(0,0,1;3.92699rad)
  Radius = 1.5
FEATURE [Part::Cylinder] Cylinder1315  label="Válec1315"
  Angle = 360
  AttacherType = Attacher::AttachEngine3D
  Height = 32
  Placement = pos=(0,-42,33.5) rot=(0,0,1;0rad)
  Radius = 1.5
FEATURE [Part::Cylinder] Cylinder1316  label="Válec1316"
  Angle = 360
  AttacherType = Attacher::AttachEngine3D
  Height = 32
  Placement = pos=(-1.4e-14,42,33.5) rot=(0,0,1;3.14159rad)
  Radius = 1.5
FEATURE [Part::Cylinder] Cylinder1317  label="Válec1317"
  Angle = 360
  AttacherType = Attacher::AttachEngine3D
  Height = 32
  Placement = pos=(29.6985,-29.6985,33.5) rot=(0,0,1;0.785398rad)
  Radius = 1.5
FEATURE [Part::Cylinder] Cylinder1318  label="Válec1318"
  Angle = 360
  AttacherType = Attacher::AttachEngine3D
  Height = 32
  Placement = pos=(29.6985,29.6985,33.5) rot=(0,0,1;2.35619rad)
  Radius = 1.5
FEATURE [Part::Cylinder] Cylinder1319  label="Válec1319"
  Angle = 360
  AttacherType = Attacher::AttachEngine3D
  Height = 32
  Placement = pos=(-42,-2.4e-14,33.5) rot=(0,0,-1;1.5708rad)
  Radius = 1.5
FEATURE [Part::Cylinder] Cylinder1320  label="Válec1320"
  Angle = 360
  AttacherType = Attacher::AttachEngine3D
  Height = 32
  Placement = pos=(42,6e-15,33.5) rot=(0,0,1;1.5708rad)
  Radius = 1.5
FEATURE [Part::Compound] Compound934
  Links = -> [Cylinder1315,Cylinder1317,Cylinder1320,Cylinder1318,Cylinder1316,Cylinder1314,Cylinder1319,Cylinder1313]
  Placement = pos=(0,0,0) rot=(0,0,1;0.392699rad)
FEATURE [Part::Cut] Cut477
  Base = -> Tube117
  Placement = pos=(0,0,1) rot=(0,0,1;0rad)
  Tool = -> Compound934
FEATURE [Part::Compound] Compound935  label="J-midi-thin_actuator_v1"
  Links = -> [Cut477,Cut476,Cut474]
FEATURE [Part::Cylinder] Cylinder1321  label="Válec1321"
  Angle = 360
  AttacherType = Attacher::AttachEngine3D
  Height = 20
  Placement = pos=(4,4,-88) rot=(0,0,1;3.14159rad)
  Radius = 1
FEATURE [Part::Cylinder] Cylinder1322  label="Válec1322"
  Angle = 360
  AttacherType = Attacher::AttachEngine3D
  Height = 4
  Placement = pos=(0,0,15) rot=(0,0,1;0rad)
  Radius = 7.5
FEATURE [Part::Cylinder] Cylinder1323  label="Válec1323"
  Angle = 360
  AttacherType = Attacher::AttachEngine3D
  Height = 20
  Placement = pos=(-4,4,-88) rot=(0,0,-1;1.5708rad)
  Radius = 1
FEATURE [Part::Cylinder] Cylinder1324  label="Válec1324"
  Angle = 360
  AttacherType = Attacher::AttachEngine3D
  Height = 20
  Placement = pos=(4,-4,-88) rot=(0,0,1;1.5708rad)
  Radius = 1
FEATURE [Part::Cylinder] Cylinder1325  label="Válec1325"
  Angle = 360
  AttacherType = Attacher::AttachEngine3D
  Height = 20
  Placement = pos=(-4,4,-88) rot=(0,0,-1;1.5708rad)
  Radius = 1
FEATURE [Part::Cylinder] Cylinder1326  label="Válec1326"
  Angle = 360
  AttacherType = Attacher::AttachEngine3D
  Height = 2
  Placement = pos=(-4,-4,-88) rot=(0,0,1;0rad)
  Radius = 2
FEATURE [Part::Cylinder] Cylinder1327  label="Válec1327"
  Angle = 360
  AttacherType = Attacher::AttachEngine3D
  Height = 20
  Placement = pos=(-4,-4,-88) rot=(0,0,1;0rad)
  Radius = 1
FEATURE [Part::Cylinder] Cylinder1328  label="Válec1328"
  Angle = 360
  AttacherType = Attacher::AttachEngine3D
  Height = 2
  Placement = pos=(-4,4,-88) rot=(0,0,-1;1.5708rad)
  Radius = 2
FEATURE [Part::Cylinder] Cylinder1329  label="Válec1329"
  Angle = 360
  AttacherType = Attacher::AttachEngine3D
  Height = 2
  Placement = pos=(4,4,-88) rot=(0,0,1;3.14159rad)
  Radius = 2
FEATURE [Part::Cylinder] Cylinder1330  label="Válec1330"
  Angle = 360
  AttacherType = Attacher::AttachEngine3D
  Height = 20
  Placement = pos=(4,-4,-88) rot=(0,0,1;1.5708rad)
  Radius = 1
FEATURE [Part::Cylinder] Cylinder1331  label="Válec1331"
  Angle = 360
  AttacherType = Attacher::AttachEngine3D
  Height = 20
  Placement = pos=(4,-4,-88) rot=(0,0,1;1.5708rad)
  Radius = 1
FEATURE [Part::Cylinder] Cylinder1332  label="Válec1332"
  Angle = 360
  AttacherType = Attacher::AttachEngine3D
  Height = 2
  Placement = pos=(4,-4,-88) rot=(0,0,1;1.5708rad)
  Radius = 2
FEATURE [Part::Cylinder] Cylinder1333  label="Válec1333"
  Angle = 360
  AttacherType = Attacher::AttachEngine3D
  Height = 20
  Placement = pos=(4,4,-88) rot=(0,0,1;3.14159rad)
  Radius = 1
FEATURE [Part::Cylinder] Cylinder1334  label="Válec1334"
  Angle = 360
  AttacherType = Attacher::AttachEngine3D
  Height = 20
  Placement = pos=(-4,4,-88) rot=(0,0,-1;1.5708rad)
  Radius = 1
FEATURE [Part::Cylinder] Cylinder1335  label="Válec1335"
  Angle = 360
  AttacherType = Attacher::AttachEngine3D
  Height = 20
  Placement = pos=(4,4,-88) rot=(0,0,1;3.14159rad)
  Radius = 1
FEATURE [Part::Cylinder] Cylinder1336  label="Válec1336"
  Angle = 360
  AttacherType = Attacher::AttachEngine3D
  Height = 20
  Placement = pos=(-4,-4,-88) rot=(0,0,1;0rad)
  Radius = 1
FEATURE [Part::FeaturePython] Tube118  # WARN: FeaturePython — macro-defined, semantics opaque (R4)
  AttacherType = Attacher::AttachEngine3D
  Height = 10
  InnerRadius = 2.75
  OuterRadius = 7.5
  Placement = pos=(0,0,19) rot=(0,0,1;0rad)
FEATURE [Part::Compound] Compound936
  Links = -> [Cylinder1336,Cylinder1324,Cylinder1321,Cylinder1323]
  Placement = pos=(0,0,91) rot=(0,0,1;0rad)
FEATURE [Part::Compound] Compound937
  Links = -> [Cylinder1327,Cylinder1331,Cylinder1333,Cylinder1334]
  Placement = pos=(0,0,91) rot=(0,0,1;0rad)
FEATURE [Part::Cut] Cut478
  Base = -> Tube118
  Tool = -> Compound937
FEATURE [Part::Compound] Compound940
  Links = -> [Cylinder1326,Cylinder1332,Cylinder1329,Cylinder1328]
  Placement = pos=(0,0,91) rot=(0,0,1;0rad)
FEATURE [Part::Wedge] Wedge040  label="Klín040"
  AttacherType = Attacher::AttachEngine3D
  Placement = pos=(0,0,12) rot=(0,0,1;0rad)
  X2max = 0
  X2min = 0
  Xmax = 10
  Xmin = -10
  Ymax = 0
  Ymin = -32
  Z2max = 12
  Z2min = 0
  Zmax = 12
  Zmin = 0
FEATURE [Part::Wedge] Wedge041  label="Klín041"
  AttacherType = Attacher::AttachEngine3D
  Placement = pos=(0,0,12) rot=(0,0,1;3.14159rad)
  X2max = 0
  X2min = 0
  Xmax = 10
  Xmin = -10
  Ymax = 0
  Ymin = -32
  Z2max = 12
  Z2min = 0
  Zmax = 12
  Zmin = 0
FEATURE [Part::Cylinder] Cylinder1337  label="Válec1337"
  Angle = 360
  AttacherType = Attacher::AttachEngine3D
  Height = 20
  Placement = pos=(-4,-4,-88) rot=(0,0,1;0rad)
  Radius = 1
FEATURE [Part::Compound] Compound941
  Links = -> [Cylinder1337,Cylinder1330,Cylinder1335,Cylinder1325]
  Placement = pos=(0,0,91) rot=(0,0,1;0rad)
FEATURE [Part::Cut] Cut479
  Base = -> Cylinder1322
  Tool = -> Compound941
FEATURE [Part::Cylinder] Cylinder1338  label="Válec1338"
  Angle = 360
  AttacherType = Attacher::AttachEngine3D
  Height = 60
  Placement = pos=(0,0,-10) rot=(0,0,1;0rad)
  Radius = 2.75
FEATURE [Part::Wedge] Wedge042  label="Klín042"
  AttacherType = Attacher::AttachEngine3D
  Placement = pos=(0,0,12) rot=(0,0,1;1.5708rad)
  X2max = 0
  X2min = 0
  Xmax = 10
  Xmin = -10
  Ymax = 0
  Ymin = -32
  Z2max = 12
  Z2min = 0
  Zmax = 12
  Zmin = 0
FEATURE [Part::Wedge] Wedge043  label="Klín043"
  AttacherType = Attacher::AttachEngine3D
  Placement = pos=(0,0,12) rot=(0,0,-1;1.5708rad)
  X2max = 0
  X2min = 0
  Xmax = 10
  Xmin = -10
  Ymax = 0
  Ymin = -32
  Z2max = 12
  Z2min = 0
  Zmax = 12
  Zmin = 0
FEATURE [Part::Compound] Compound939
  Links = -> [Wedge040,Wedge042,Wedge041,Wedge043]
FEATURE [Part::FeaturePython] wormgear072  # WARN: FeaturePython — macro-defined, semantics opaque (R4)
  AttacherType = Attacher::AttachEngine3D
  Placement = pos=(0,0,29) rot=(0,0,1;0.994838rad)
  beta = 40.9407
  clearance = 0.25
  diameter = 20.75
  head = 0.25
  height = 8
  module = 1.5
  pressure_angle = 20
  reverse_pitch = false
  teeth = 12
  version = 0.0.3
FEATURE [Part::Cut] Cut480
  Base = -> wormgear072
  Tool = -> Cylinder1338
FEATURE [Part::FeaturePython] Tube119  # WARN: FeaturePython — macro-defined, semantics opaque (R4)
  AttacherType = Attacher::AttachEngine3D
  Height = 12
  InnerRadius = 3.75
  OuterRadius = 7.5
  Placement = pos=(0,0,12) rot=(0,0,1;0rad)
FEATURE [Part::Cut] Cut483
  Base = -> Tube119
  Placement = pos=(0,0,-9) rot=(0,0,1;0rad)
  Tool = -> Compound939
FEATURE [Part::Chamfer] Chamfer035
  Base = -> Cut483
  Edges = 8 edges r=1: [Edge7,Edge8,Edge21,Edge22,Edge31,Edge32,Edge45,Edge46]
FEATURE [Part::Cut] Cut482
  Base = -> Chamfer035
  Tool = -> Compound940
FEATURE [Part::Cut] Cut481
  Base = -> Cut482
  Tool = -> Compound936
FEATURE [Part::Compound] Compound938  label="J-midi-thin_inner-planeo-m1.5-reinforced_v5.5"
  Links = -> [Cut480,Cut481,Cut479,Cut478]
  Placement = pos=(0,0,-4) rot=(0,0,1;0rad)
FEATURE [Part::Wedge] Wedge044  label="Klín044"
  AttacherType = Attacher::AttachEngine3D
  Placement = pos=(0,0,12) rot=(0,0,1;1.5708rad)
  X2max = 0
  X2min = 0
  Xmax = 10
  Xmin = -10
  Ymax = 0
  Ymin = -32
  Z2max = 12
  Z2min = 0
  Zmax = 12
  Zmin = 0
FEATURE [Part::Wedge] Wedge045  label="Klín045"
  AttacherType = Attacher::AttachEngine3D
  Placement = pos=(0,0,12) rot=(0,0,-1;1.5708rad)
  X2max = 0
  X2min = 0
  Xmax = 10
  Xmin = -10
  Ymax = 0
  Ymin = -32
  Z2max = 12
  Z2min = 0
  Zmax = 12
  Zmin = 0
FEATURE [Part::Wedge] Wedge046  label="Klín046"
  AttacherType = Attacher::AttachEngine3D
  Placement = pos=(0,0,12) rot=(0,0,1;0rad)
  X2max = 0
  X2min = 0
  Xmax = 10
  Xmin = -10
  Ymax = 0
  Ymin = -32
  Z2max = 12
  Z2min = 0
  Zmax = 12
  Zmin = 0
FEATURE [Part::Wedge] Wedge047  label="Klín047"
  AttacherType = Attacher::AttachEngine3D
  Placement = pos=(0,0,12) rot=(0,0,1;3.14159rad)
  X2max = 0
  X2min = 0
  Xmax = 10
  Xmin = -10
  Ymax = 0
  Ymin = -32
  Z2max = 12
  Z2min = 0
  Zmax = 12
  Zmin = 0
FEATURE [Part::Compound] Compound945
  Links = -> [Wedge046,Wedge044,Wedge047,Wedge045]
FEATURE [Part::Cylinder] Cylinder1339  label="Válec1339"
  Angle = 360
  AttacherType = Attacher::AttachEngine3D
  Height = 20
  Placement = pos=(4,4,-88) rot=(0,0,1;3.14159rad)
  Radius = 1
FEATURE [Part::Cylinder] Cylinder1340  label="Válec1340"
  Angle = 360
  AttacherType = Attacher::AttachEngine3D
  Height = 4
  Placement = pos=(0,0,15) rot=(0,0,1;0rad)
  Radius = 7.5
FEATURE [Part::Cylinder] Cylinder1341  label="Válec1341"
  Angle = 360
  AttacherType = Attacher::AttachEngine3D
  Height = 20
  Placement = pos=(-4,4,-88) rot=(0,0,-1;1.5708rad)
  Radius = 1
FEATURE [Part::Cylinder] Cylinder1342  label="Válec1342"
  Angle = 360
  AttacherType = Attacher::AttachEngine3D
  Height = 20
  Placement = pos=(4,-4,-88) rot=(0,0,1;1.5708rad)
  Radius = 1
FEATURE [Part::Cylinder] Cylinder1343  label="Válec1343"
  Angle = 360
  AttacherType = Attacher::AttachEngine3D
  Height = 20
  Placement = pos=(-4,4,-88) rot=(0,0,-1;1.5708rad)
  Radius = 1
FEATURE [Part::Cylinder] Cylinder1344  label="Válec1344"
  Angle = 360
  AttacherType = Attacher::AttachEngine3D
  Height = 2
  Placement = pos=(-4,-4,-88) rot=(0,0,1;0rad)
  Radius = 2
FEATURE [Part::Cylinder] Cylinder1345  label="Válec1345"
  Angle = 360
  AttacherType = Attacher::AttachEngine3D
  Height = 20
  Placement = pos=(-4,-4,-88) rot=(0,0,1;0rad)
  Radius = 1
FEATURE [Part::Cylinder] Cylinder1346  label="Válec1346"
  Angle = 360
  AttacherType = Attacher::AttachEngine3D
  Height = 2
  Placement = pos=(-4,4,-88) rot=(0,0,-1;1.5708rad)
  Radius = 2
FEATURE [Part::Cylinder] Cylinder1347  label="Válec1347"
  Angle = 360
  AttacherType = Attacher::AttachEngine3D
  Height = 2
  Placement = pos=(4,4,-88) rot=(0,0,1;3.14159rad)
  Radius = 2
FEATURE [Part::Cylinder] Cylinder1348  label="Válec1348"
  Angle = 360
  AttacherType = Attacher::AttachEngine3D
  Height = 20
  Placement = pos=(4,-4,-88) rot=(0,0,1;1.5708rad)
  Radius = 1
FEATURE [Part::Cylinder] Cylinder1349  label="Válec1349"
  Angle = 360
  AttacherType = Attacher::AttachEngine3D
  Height = 20
  Placement = pos=(4,-4,-88) rot=(0,0,1;1.5708rad)
  Radius = 1
FEATURE [Part::Cylinder] Cylinder1350  label="Válec1350"
  Angle = 360
  AttacherType = Attacher::AttachEngine3D
  Height = 2
  Placement = pos=(4,-4,-88) rot=(0,0,1;1.5708rad)
  Radius = 2
FEATURE [Part::Compound] Compound946
  Links = -> [Cylinder1344,Cylinder1350,Cylinder1347,Cylinder1346]
  Placement = pos=(0,0,91) rot=(0,0,1;0rad)
FEATURE [Part::Cylinder] Cylinder1351  label="Válec1351"
  Angle = 360
  AttacherType = Attacher::AttachEngine3D
  Height = 20
  Placement = pos=(4,4,-88) rot=(0,0,1;3.14159rad)
  Radius = 1
FEATURE [Part::Cylinder] Cylinder1352  label="Válec1352"
  Angle = 360
  AttacherType = Attacher::AttachEngine3D
  Height = 20
  Placement = pos=(-4,4,-88) rot=(0,0,-1;1.5708rad)
  Radius = 1
FEATURE [Part::Compound] Compound943
  Links = -> [Cylinder1345,Cylinder1349,Cylinder1351,Cylinder1352]
  Placement = pos=(0,0,91) rot=(0,0,1;0rad)
FEATURE [Part::Cylinder] Cylinder1353  label="Válec1353"
  Angle = 360
  AttacherType = Attacher::AttachEngine3D
  Height = 20
  Placement = pos=(4,4,-88) rot=(0,0,1;3.14159rad)
  Radius = 1
FEATURE [Part::Cylinder] Cylinder1354  label="Válec1354"
  Angle = 360
  AttacherType = Attacher::AttachEngine3D
  Height = 20
  Placement = pos=(-4,-4,-88) rot=(0,0,1;0rad)
  Radius = 1
FEATURE [Part::Compound] Compound942
  Links = -> [Cylinder1354,Cylinder1342,Cylinder1339,Cylinder1341]
  Placement = pos=(0,0,91) rot=(0,0,1;0rad)
FEATURE [Part::Cylinder] Cylinder1355  label="Válec1355"
  Angle = 360
  AttacherType = Attacher::AttachEngine3D
  Height = 20
  Placement = pos=(-4,-4,-88) rot=(0,0,1;0rad)
  Radius = 1
FEATURE [Part::Compound] Compound947
  Links = -> [Cylinder1355,Cylinder1348,Cylinder1353,Cylinder1343]
  Placement = pos=(0,0,91) rot=(0,0,1;0rad)
FEATURE [Part::Cylinder] Cylinder1356  label="Válec1356"
  Angle = 360
  AttacherType = Attacher::AttachEngine3D
  Height = 60
  Placement = pos=(0,0,-10) rot=(0,0,1;0rad)
  Radius = 2.75
FEATURE [Part::FeaturePython] Tube120  # WARN: FeaturePython — macro-defined, semantics opaque (R4)
  AttacherType = Attacher::AttachEngine3D
  Height = 10
  InnerRadius = 2.75
  OuterRadius = 7.5
  Placement = pos=(0,0,19) rot=(0,0,1;0rad)
FEATURE [Part::FeaturePython] wormgear073  # WARN: FeaturePython — macro-defined, semantics opaque (R4)
  AttacherType = Attacher::AttachEngine3D
  Placement = pos=(0,0,29) rot=(0,0,1;0.994838rad)
  beta = 41.2847
  clearance = 0.25
  diameter = 20.5
  head = 0.25
  height = 8
  module = 1.5
  pressure_angle = 20
  reverse_pitch = false
  teeth = 12
  version = 0.0.3
FEATURE [Part::FeaturePython] Tube121  # WARN: FeaturePython — macro-defined, semantics opaque (R4)
  AttacherType = Attacher::AttachEngine3D
  Height = 12
  InnerRadius = 3.75
  OuterRadius = 7.5
  Placement = pos=(0,0,12) rot=(0,0,1;0rad)
FEATURE [Part::Cut] Cut484
  Base = -> Tube120
  Tool = -> Compound943
FEATURE [Part::Cut] Cut485
  Base = -> Cylinder1340
  Tool = -> Compound947
FEATURE [Part::Cut] Cut486
  Base = -> wormgear073
  Tool = -> Cylinder1356
FEATURE [Part::Cut] Cut489
  Base = -> Tube121
  Placement = pos=(0,0,-9) rot=(0,0,1;0rad)
  Tool = -> Compound945
FEATURE [Part::Chamfer] Chamfer036
  Base = -> Cut489
  Edges = 8 edges r=1: [Edge7,Edge8,Edge21,Edge22,Edge31,Edge32,Edge45,Edge46]
FEATURE [Part::Cut] Cut488
  Base = -> Chamfer036
  Tool = -> Compound946
FEATURE [Part::Cut] Cut487
  Base = -> Cut488
  Tool = -> Compound942
FEATURE [Part::Compound] Compound944  label="J-midi-thin_inner-planeo-m1.5-reinforced_v5.6"
  Links = -> [Cut486,Cut487,Cut485,Cut484]
  Placement = pos=(0,0,-4) rot=(0,0,1;0rad)
FEATURE [Part::FeaturePython] Tube122  label="ZKL-61816-005"  # WARN: FeaturePython — macro-defined, semantics opaque (R4)
  AttacherType = Attacher::AttachEngine3D
  Height = 10
  InnerRadius = 40
  OuterRadius = 50
  Placement = pos=(0,0,29) rot=(0,0,1;0rad)
FEATURE [Part::Cylinder] Cylinder1357  label="Válec1357"
  Angle = 360
  AttacherType = Attacher::AttachEngine3D
  Height = 32
  Placement = pos=(-29.6985,-29.6985,33.5) rot=(0,0,-1;0.785398rad)
  Radius = 1.5
FEATURE [Part::Cylinder] Cylinder1358  label="Válec1358"
  Angle = 360
  AttacherType = Attacher::AttachEngine3D
  Height = 32
  Placement = pos=(-29.6985,29.6985,33.5) rot=(0,0,1;3.92699rad)
  Radius = 1.5
FEATURE [Part::Box] Box568  label="Krychle568"
  AttacherType = Attacher::AttachEngine3D
  Height = 2
  Length = 6
  Placement = pos=(-34.6482,-30.4056,33) rot=(0,0,-1;0.785398rad)
  Width = 8
FEATURE [Part::Box] Box569  label="Krychle569"
  AttacherType = Attacher::AttachEngine3D
  Height = 2
  Length = 6
  Placement = pos=(-3,-46,33) rot=(0,0,1;0rad)
  Width = 8
FEATURE [Part::Box] Box570  label="Krychle570"
  AttacherType = Attacher::AttachEngine3D
  Height = 2
  Length = 6
  Placement = pos=(46,-3,33) rot=(0,0,1;1.5708rad)
  Width = 8
FEATURE [Part::Box] Box571  label="Krychle571"
  AttacherType = Attacher::AttachEngine3D
  Height = 2
  Length = 6
  Placement = pos=(-30.4056,34.6482,33) rot=(0,0,1;3.92699rad)
  Width = 8
FEATURE [Part::Cylinder] Cylinder1359  label="Válec1359"
  Angle = 360
  AttacherType = Attacher::AttachEngine3D
  Height = 32
  Placement = pos=(0,-42,33.5) rot=(0,0,1;0rad)
  Radius = 1.5
FEATURE [Part::Cylinder] Cylinder1360  label="Válec1360"
  Angle = 360
  AttacherType = Attacher::AttachEngine3D
  Height = 32
  Placement = pos=(-1.4e-14,42,33.5) rot=(0,0,1;3.14159rad)
  Radius = 1.5
FEATURE [Part::Box] Box572  label="Krychle572"
  AttacherType = Attacher::AttachEngine3D
  Height = 2
  Length = 6
  Placement = pos=(30.4056,-34.6482,33) rot=(0,0,1;0.785398rad)
  Width = 8
FEATURE [Part::Box] Box573  label="Krychle573"
  AttacherType = Attacher::AttachEngine3D
  Height = 2
  Length = 6
  Placement = pos=(34.6482,30.4056,33) rot=(0,0,1;2.35619rad)
  Width = 8
FEATURE [Part::Cylinder] Cylinder1361  label="Válec1361"
  Angle = 360
  AttacherType = Attacher::AttachEngine3D
  Height = 32
  Placement = pos=(29.6985,-29.6985,33.5) rot=(0,0,1;0.785398rad)
  Radius = 1.5
FEATURE [Part::Cylinder] Cylinder1362  label="Válec1362"
  Angle = 360
  AttacherType = Attacher::AttachEngine3D
  Height = 32
  Placement = pos=(29.6985,29.6985,33.5) rot=(0,0,1;2.35619rad)
  Radius = 1.5
FEATURE [Part::Cylinder] Cylinder1363  label="Válec1363"
  Angle = 360
  AttacherType = Attacher::AttachEngine3D
  Height = 32
  Placement = pos=(-42,-2.4e-14,33.5) rot=(0,0,-1;1.5708rad)
  Radius = 1.5
FEATURE [Part::Cylinder] Cylinder1364  label="Válec1364"
  Angle = 360
  AttacherType = Attacher::AttachEngine3D
  Height = 32
  Placement = pos=(42,6e-15,33.5) rot=(0,0,1;1.5708rad)
  Radius = 1.5
FEATURE [Part::Box] Box574  label="Krychle574"
  AttacherType = Attacher::AttachEngine3D
  Height = 2
  Length = 6
  Placement = pos=(3,46,33) rot=(0,0,1;3.14159rad)
  Width = 8
FEATURE [Part::Box] Box575  label="Krychle575"
  AttacherType = Attacher::AttachEngine3D
  Height = 2
  Length = 6
  Placement = pos=(-46,3,33) rot=(0,0,-1;1.5708rad)
  Width = 8
FEATURE [Part::Compound] Compound948
  Links = -> [Box568,Box572,Box570,Box569,Box573,Box574,Box571,Box575]
  Placement = pos=(0,0,4.4) rot=(0,0,1;0.392699rad)
FEATURE [Part::FeaturePython] Tube123  # WARN: FeaturePython — macro-defined, semantics opaque (R4)
  AttacherType = Attacher::AttachEngine3D
  Height = 16
  InnerRadius = 40
  OuterRadius = 46
  Placement = pos=(0,0,26) rot=(0,0,1;0rad)
FEATURE [Part::FeaturePython] Tube124  label="ZKL-61816-006"  # WARN: FeaturePython — macro-defined, semantics opaque (R4)
  AttacherType = Attacher::AttachEngine3D
  Height = 11
  InnerRadius = 40
  OuterRadius = 50
  Placement = pos=(0,0,25.4) rot=(0,0,1;0rad)
FEATURE [Part::Cut] Cut493
  Base = -> Tube123
  Tool = -> Tube124
FEATURE [Part::FeaturePython] wormgear074  # WARN: FeaturePython — macro-defined, semantics opaque (R4)
  AttacherType = Attacher::AttachEngine3D
  Placement = pos=(0,0,0) rot=(0,0,1;0.10472rad)
  beta = 38.5565
  clearance = 0.25
  diameter = 67.75
  head = 0
  height = 14
  module = 1.5
  pressure_angle = 20
  reverse_pitch = true
  teeth = 36
  version = 0.0.3
FEATURE [Part::FeaturePython] wormgear075  # WARN: FeaturePython — macro-defined, semantics opaque (R4)
  AttacherType = Attacher::AttachEngine3D
  Placement = pos=(0,0,0) rot=(0,0,-1;0.1309rad)
  beta = 38.5565
  clearance = 0.25
  diameter = 67.75
  head = 0
  height = 14
  module = 1.5
  pressure_angle = 20
  reverse_pitch = false
  teeth = 36
  version = 0.0.3
FEATURE [Part::FeaturePython] Tube125  label="ZKL-61816-007"  # WARN: FeaturePython — macro-defined, semantics opaque (R4)
  AttacherType = Attacher::AttachEngine3D
  Height = 11
  InnerRadius = 40
  OuterRadius = 50
  Placement = pos=(0,0,25) rot=(0,0,1;0rad)
FEATURE [Part::Compound] Compound949
  Links = -> [Cylinder1359,Cylinder1361,Cylinder1364,Cylinder1362,Cylinder1360,Cylinder1358,Cylinder1363,Cylinder1357]
  Placement = pos=(0,0,0) rot=(0,0,1;0.392699rad)
FEATURE [Part::Cut] Cut495
  Base = -> Cut493
  Tool = -> Compound949
FEATURE [Part::Cut] Cut496
  Base = -> Cut495
  Placement = pos=(0,0,3) rot=(0,0,1;0rad)
  Tool = -> Compound948
FEATURE [Part::Box] Box576  label="Krychle576"
  AttacherType = Attacher::AttachEngine3D
  Height = 2
  Length = 6
  Placement = pos=(3,46,33) rot=(0,0,1;3.14159rad)
  Width = 8
FEATURE [Part::Box] Box577  label="Krychle577"
  AttacherType = Attacher::AttachEngine3D
  Height = 2
  Length = 6
  Placement = pos=(30.4056,-34.6482,33) rot=(0,0,1;0.785398rad)
  Width = 8
FEATURE [Part::Cylinder] Cylinder1365  label="Válec1365"
  Angle = 360
  AttacherType = Attacher::AttachEngine3D
  Height = 8
  Radius = 40
FEATURE [Part::Cut] Cut490
  Base = -> Cylinder1365
  Placement = pos=(0,0,25) rot=(0,0,1;0.294961rad)
  Tool = -> wormgear075
FEATURE [Part::Box] Box578  label="Krychle578"
  AttacherType = Attacher::AttachEngine3D
  Height = 2
  Length = 6
  Placement = pos=(-34.6482,-30.4056,33) rot=(0,0,-1;0.785398rad)
  Width = 8
FEATURE [Part::Box] Box579  label="Krychle579"
  AttacherType = Attacher::AttachEngine3D
  Height = 2
  Length = 6
  Placement = pos=(34.6482,30.4056,33) rot=(0,0,1;2.35619rad)
  Width = 8
FEATURE [Part::Box] Box580  label="Krychle580"
  AttacherType = Attacher::AttachEngine3D
  Height = 2
  Length = 6
  Placement = pos=(-3,-46,33) rot=(0,0,1;0rad)
  Width = 8
FEATURE [Part::Box] Box581  label="Krychle581"
  AttacherType = Attacher::AttachEngine3D
  Height = 2
  Length = 6
  Placement = pos=(-30.4056,34.6482,33) rot=(0,0,1;3.92699rad)
  Width = 8
FEATURE [Part::Cylinder] Cylinder1366  label="Válec1366"
  Angle = 360
  AttacherType = Attacher::AttachEngine3D
  Height = 8
  Radius = 40
FEATURE [Part::Cut] Cut491
  Base = -> Cylinder1366
  Placement = pos=(0,0,33) rot=(0,0,1;0.53058rad)
  Tool = -> wormgear074
FEATURE [Part::Box] Box582  label="Krychle582"
  AttacherType = Attacher::AttachEngine3D
  Height = 2
  Length = 6
  Placement = pos=(-46,3,33) rot=(0,0,-1;1.5708rad)
  Width = 8
FEATURE [Part::Box] Box583  label="Krychle583"
  AttacherType = Attacher::AttachEngine3D
  Height = 2
  Length = 6
  Placement = pos=(46,-3,33) rot=(0,0,1;1.5708rad)
  Width = 8
FEATURE [Part::Compound] Compound950
  Links = -> [Box578,Box577,Box583,Box580,Box579,Box576,Box581,Box582]
  Placement = pos=(0,0,3.4) rot=(0,0,1;0.392699rad)
FEATURE [Part::Cut] Cut492
  Base = -> Cut491
  Tool = -> Compound950
FEATURE [Part::Compound] Compound951
  Links = -> [Cut492,Cut490]
  Placement = pos=(0,0,4) rot=(0,0,1;0rad)
FEATURE [Part::Cut] Cut494
  Base = -> Compound951
  Tool = -> Tube125
FEATURE [Part::FeaturePython] Tube126  label="ZKL-61816-subwasher001"  # WARN: FeaturePython — macro-defined, semantics opaque (R4)
  AttacherType = Attacher::AttachEngine3D
  Height = 0.4
  InnerRadius = 40
  OuterRadius = 42
  Placement = pos=(0,0,38) rot=(0,0,1;0rad)
FEATURE [Part::Cylinder] Cylinder1367  label="Válec1367"
  Angle = 360
  AttacherType = Attacher::AttachEngine3D
  Height = 32
  Placement = pos=(-29.6985,-29.6985,33.5) rot=(0,0,-1;0.785398rad)
  Radius = 1.5
FEATURE [Part::Cylinder] Cylinder1368  label="Válec1368"
  Angle = 360
  AttacherType = Attacher::AttachEngine3D
  Height = 32
  Placement = pos=(-29.6985,29.6985,33.5) rot=(0,0,1;3.92699rad)
  Radius = 1.5
FEATURE [Part::Cylinder] Cylinder1369  label="Válec1369"
  Angle = 360
  AttacherType = Attacher::AttachEngine3D
  Height = 32
  Placement = pos=(0,-42,33.5) rot=(0,0,1;0rad)
  Radius = 1.5
FEATURE [Part::Cylinder] Cylinder1370  label="Válec1370"
  Angle = 360
  AttacherType = Attacher::AttachEngine3D
  Height = 32
  Placement = pos=(-1.4e-14,42,33.5) rot=(0,0,1;3.14159rad)
  Radius = 1.5
FEATURE [Part::Cylinder] Cylinder1371  label="Válec1371"
  Angle = 360
  AttacherType = Attacher::AttachEngine3D
  Height = 32
  Placement = pos=(29.6985,-29.6985,33.5) rot=(0,0,1;0.785398rad)
  Radius = 1.5
FEATURE [Part::Cylinder] Cylinder1372  label="Válec1372"
  Angle = 360
  AttacherType = Attacher::AttachEngine3D
  Height = 32
  Placement = pos=(29.6985,29.6985,33.5) rot=(0,0,1;2.35619rad)
  Radius = 1.5
FEATURE [Part::Cylinder] Cylinder1373  label="Válec1373"
  Angle = 360
  AttacherType = Attacher::AttachEngine3D
  Height = 32
  Placement = pos=(-42,-2.4e-14,33.5) rot=(0,0,-1;1.5708rad)
  Radius = 1.5
FEATURE [Part::Cylinder] Cylinder1374  label="Válec1374"
  Angle = 360
  AttacherType = Attacher::AttachEngine3D
  Height = 32
  Placement = pos=(42,6e-15,33.5) rot=(0,0,1;1.5708rad)
  Radius = 1.5
FEATURE [Part::Compound] Compound952
  Links = -> [Cylinder1369,Cylinder1371,Cylinder1374,Cylinder1372,Cylinder1370,Cylinder1368,Cylinder1373,Cylinder1367]
  Placement = pos=(0,0,0) rot=(0,0,1;0.392699rad)
FEATURE [Part::Cut] Cut497
  Base = -> Tube126
  Placement = pos=(0,0,1) rot=(0,0,1;0rad)
  Tool = -> Compound952
FEATURE [Part::Compound] Compound953  label="J-midi-thin_actuator_v1.5"
  Links = -> [Cut497,Cut496,Cut494]
FEATURE [Part::Wedge] Wedge048  label="Klín048"
  AttacherType = Attacher::AttachEngine3D
  Placement = pos=(0,0,12) rot=(0,0,1;1.5708rad)
  X2max = 0
  X2min = 0
  Xmax = 10
  Xmin = -10
  Ymax = 0
  Ymin = -32
  Z2max = 12
  Z2min = 0
  Zmax = 12
  Zmin = 0
FEATURE [Part::Wedge] Wedge049  label="Klín049"
  AttacherType = Attacher::AttachEngine3D
  Placement = pos=(0,0,12) rot=(0,0,-1;1.5708rad)
  X2max = 0
  X2min = 0
  Xmax = 10
  Xmin = -10
  Ymax = 0
  Ymin = -32
  Z2max = 12
  Z2min = 0
  Zmax = 12
  Zmin = 0
FEATURE [Part::Wedge] Wedge050  label="Klín050"
  AttacherType = Attacher::AttachEngine3D
  Placement = pos=(0,0,12) rot=(0,0,1;0rad)
  X2max = 0
  X2min = 0
  Xmax = 10
  Xmin = -10
  Ymax = 0
  Ymin = -32
  Z2max = 12
  Z2min = 0
  Zmax = 12
  Zmin = 0
FEATURE [Part::Wedge] Wedge051  label="Klín051"
  AttacherType = Attacher::AttachEngine3D
  Placement = pos=(0,0,12) rot=(0,0,1;3.14159rad)
  X2max = 0
  X2min = 0
  Xmax = 10
  Xmin = -10
  Ymax = 0
  Ymin = -32
  Z2max = 12
  Z2min = 0
  Zmax = 12
  Zmin = 0
FEATURE [Part::Cylinder] Cylinder1375  label="Válec1375"
  Angle = 360
  AttacherType = Attacher::AttachEngine3D
  Height = 20
  Placement = pos=(4,4,-88) rot=(0,0,1;3.14159rad)
  Radius = 1
FEATURE [Part::Cylinder] Cylinder1376  label="Válec1376"
  Angle = 360
  AttacherType = Attacher::AttachEngine3D
  Height = 4
  Placement = pos=(0,0,15) rot=(0,0,1;0rad)
  Radius = 7.5
FEATURE [Part::Cylinder] Cylinder1377  label="Válec1377"
  Angle = 360
  AttacherType = Attacher::AttachEngine3D
  Height = 20
  Placement = pos=(-4,4,-88) rot=(0,0,-1;1.5708rad)
  Radius = 1
FEATURE [Part::Cylinder] Cylinder1378  label="Válec1378"
  Angle = 360
  AttacherType = Attacher::AttachEngine3D
  Height = 20
  Placement = pos=(4,-4,-88) rot=(0,0,1;1.5708rad)
  Radius = 1
FEATURE [Part::Cylinder] Cylinder1379  label="Válec1379"
  Angle = 360
  AttacherType = Attacher::AttachEngine3D
  Height = 20
  Placement = pos=(-4,4,-88) rot=(0,0,-1;1.5708rad)
  Radius = 1
FEATURE [Part::Cylinder] Cylinder1380  label="Válec1380"
  Angle = 360
  AttacherType = Attacher::AttachEngine3D
  Height = 2
  Placement = pos=(-4,-4,-88) rot=(0,0,1;0rad)
  Radius = 2
FEATURE [Part::Cylinder] Cylinder1381  label="Válec1381"
  Angle = 360
  AttacherType = Attacher::AttachEngine3D
  Height = 20
  Placement = pos=(-4,-4,-88) rot=(0,0,1;0rad)
  Radius = 1
FEATURE [Part::Cylinder] Cylinder1382  label="Válec1382"
  Angle = 360
  AttacherType = Attacher::AttachEngine3D
  Height = 2
  Placement = pos=(-4,4,-88) rot=(0,0,-1;1.5708rad)
  Radius = 2
FEATURE [Part::Cylinder] Cylinder1383  label="Válec1383"
  Angle = 360
  AttacherType = Attacher::AttachEngine3D
  Height = 2
  Placement = pos=(4,4,-88) rot=(0,0,1;3.14159rad)
  Radius = 2
FEATURE [Part::Cylinder] Cylinder1384  label="Válec1384"
  Angle = 360
  AttacherType = Attacher::AttachEngine3D
  Height = 20
  Placement = pos=(4,-4,-88) rot=(0,0,1;1.5708rad)
  Radius = 1
FEATURE [Part::Cylinder] Cylinder1385  label="Válec1385"
  Angle = 360
  AttacherType = Attacher::AttachEngine3D
  Height = 20
  Placement = pos=(4,-4,-88) rot=(0,0,1;1.5708rad)
  Radius = 1
FEATURE [Part::Cylinder] Cylinder1386  label="Válec1386"
  Angle = 360
  AttacherType = Attacher::AttachEngine3D
  Height = 2
  Placement = pos=(4,-4,-88) rot=(0,0,1;1.5708rad)
  Radius = 2
FEATURE [Part::Cylinder] Cylinder1387  label="Válec1387"
  Angle = 360
  AttacherType = Attacher::AttachEngine3D
  Height = 20
  Placement = pos=(4,4,-88) rot=(0,0,1;3.14159rad)
  Radius = 1
FEATURE [Part::Cylinder] Cylinder1388  label="Válec1388"
  Angle = 360
  AttacherType = Attacher::AttachEngine3D
  Height = 20
  Placement = pos=(-4,4,-88) rot=(0,0,-1;1.5708rad)
  Radius = 1
FEATURE [Part::Compound] Compound955
  Links = -> [Cylinder1381,Cylinder1385,Cylinder1387,Cylinder1388]
  Placement = pos=(0,0,91) rot=(0,0,1;0rad)
FEATURE [Part::Cylinder] Cylinder1389  label="Válec1389"
  Angle = 360
  AttacherType = Attacher::AttachEngine3D
  Height = 20
  Placement = pos=(4,4,-88) rot=(0,0,1;3.14159rad)
  Radius = 1
FEATURE [Part::Cylinder] Cylinder1390  label="Válec1390"
  Angle = 360
  AttacherType = Attacher::AttachEngine3D
  Height = 20
  Placement = pos=(-4,-4,-88) rot=(0,0,1;0rad)
  Radius = 1
FEATURE [Part::Compound] Compound954
  Links = -> [Cylinder1390,Cylinder1378,Cylinder1375,Cylinder1377]
  Placement = pos=(0,0,91) rot=(0,0,1;0rad)
FEATURE [Part::Cylinder] Cylinder1391  label="Válec1391"
  Angle = 360
  AttacherType = Attacher::AttachEngine3D
  Height = 20
  Placement = pos=(-4,-4,-88) rot=(0,0,1;0rad)
  Radius = 1
FEATURE [Part::Cylinder] Cylinder1392  label="Válec1392"
  Angle = 360
  AttacherType = Attacher::AttachEngine3D
  Height = 60
  Placement = pos=(0,0,-10) rot=(0,0,1;0rad)
  Radius = 2.75
FEATURE [Part::Compound] Compound957
  Links = -> [Wedge050,Wedge048,Wedge051,Wedge049]
FEATURE [Part::Compound] Compound958
  Links = -> [Cylinder1380,Cylinder1386,Cylinder1383,Cylinder1382]
  Placement = pos=(0,0,91) rot=(0,0,1;0rad)
FEATURE [Part::Compound] Compound959
  Links = -> [Cylinder1391,Cylinder1384,Cylinder1389,Cylinder1379]
  Placement = pos=(0,0,91) rot=(0,0,1;0rad)
FEATURE [Part::Cut] Cut499
  Base = -> Cylinder1376
  Tool = -> Compound959
FEATURE [Part::FeaturePython] Tube127  # WARN: FeaturePython — macro-defined, semantics opaque (R4)
  AttacherType = Attacher::AttachEngine3D
  Height = 10
  InnerRadius = 2.75
  OuterRadius = 7.5
  Placement = pos=(0,0,19) rot=(0,0,1;0rad)
FEATURE [Part::Cut] Cut498
  Base = -> Tube127
  Tool = -> Compound955
FEATURE [Part::FeaturePython] wormgear076  # WARN: FeaturePython — macro-defined, semantics opaque (R4)
  AttacherType = Attacher::AttachEngine3D
  Placement = pos=(0,0,29) rot=(0,0,1;0.994838rad)
  beta = 41.9872
  clearance = 0.25
  diameter = 20
  head = 0.25
  height = 8
  module = 1.5
  pressure_angle = 20
  reverse_pitch = false
  teeth = 12
  version = 0.0.3
FEATURE [Part::Cut] Cut500
  Base = -> wormgear076
  Tool = -> Cylinder1392
FEATURE [Part::FeaturePython] Tube128  # WARN: FeaturePython — macro-defined, semantics opaque (R4)
  AttacherType = Attacher::AttachEngine3D
  Height = 12
  InnerRadius = 3.75
  OuterRadius = 7.5
  Placement = pos=(0,0,12) rot=(0,0,1;0rad)
FEATURE [Part::Cut] Cut503
  Base = -> Tube128
  Placement = pos=(0,0,-9) rot=(0,0,1;0rad)
  Tool = -> Compound957
FEATURE [Part::Chamfer] Chamfer037
  Base = -> Cut503
  Edges = 8 edges r=1: [Edge7,Edge8,Edge21,Edge22,Edge31,Edge32,Edge45,Edge46]
FEATURE [Part::Cut] Cut502
  Base = -> Chamfer037
  Tool = -> Compound958
FEATURE [Part::Cut] Cut501
  Base = -> Cut502
  Tool = -> Compound954
FEATURE [Part::Compound] Compound956  label="J-midi-thin_inner-planeo-m1.5-reinforced_v5.7"
  Links = -> [Cut500,Cut501,Cut499,Cut498]
  Placement = pos=(0,0,-4) rot=(0,0,1;0rad)
FEATURE [Part::Wedge] Wedge052  label="Klín052"
  AttacherType = Attacher::AttachEngine3D
  Placement = pos=(0,0,12) rot=(0,0,1;1.5708rad)
  X2max = 0
  X2min = 0
  Xmax = 10
  Xmin = -10
  Ymax = 0
  Ymin = -32
  Z2max = 12
  Z2min = 0
  Zmax = 12
  Zmin = 0
FEATURE [Part::Wedge] Wedge053  label="Klín053"
  AttacherType = Attacher::AttachEngine3D
  Placement = pos=(0,0,12) rot=(0,0,-1;1.5708rad)
  X2max = 0
  X2min = 0
  Xmax = 10
  Xmin = -10
  Ymax = 0
  Ymin = -32
  Z2max = 12
  Z2min = 0
  Zmax = 12
  Zmin = 0
FEATURE [Part::Wedge] Wedge054  label="Klín054"
  AttacherType = Attacher::AttachEngine3D
  Placement = pos=(0,0,12) rot=(0,0,1;0rad)
  X2max = 0
  X2min = 0
  Xmax = 10
  Xmin = -10
  Ymax = 0
  Ymin = -32
  Z2max = 12
  Z2min = 0
  Zmax = 12
  Zmin = 0
FEATURE [Part::Wedge] Wedge055  label="Klín055"
  AttacherType = Attacher::AttachEngine3D
  Placement = pos=(0,0,12) rot=(0,0,1;3.14159rad)
  X2max = 0
  X2min = 0
  Xmax = 10
  Xmin = -10
  Ymax = 0
  Ymin = -32
  Z2max = 12
  Z2min = 0
  Zmax = 12
  Zmin = 0
FEATURE [Part::Cylinder] Cylinder1393  label="Válec1393"
  Angle = 360
  AttacherType = Attacher::AttachEngine3D
  Height = 20
  Placement = pos=(4,4,-88) rot=(0,0,1;3.14159rad)
  Radius = 1
FEATURE [Part::Cylinder] Cylinder1394  label="Válec1394"
  Angle = 360
  AttacherType = Attacher::AttachEngine3D
  Height = 4
  Placement = pos=(0,0,15) rot=(0,0,1;0rad)
  Radius = 7.5
FEATURE [Part::Cylinder] Cylinder1395  label="Válec1395"
  Angle = 360
  AttacherType = Attacher::AttachEngine3D
  Height = 20
  Placement = pos=(-4,4,-88) rot=(0,0,-1;1.5708rad)
  Radius = 1
FEATURE [Part::Cylinder] Cylinder1396  label="Válec1396"
  Angle = 360
  AttacherType = Attacher::AttachEngine3D
  Height = 20
  Placement = pos=(4,-4,-88) rot=(0,0,1;1.5708rad)
  Radius = 1
FEATURE [Part::Cylinder] Cylinder1397  label="Válec1397"
  Angle = 360
  AttacherType = Attacher::AttachEngine3D
  Height = 20
  Placement = pos=(-4,4,-88) rot=(0,0,-1;1.5708rad)
  Radius = 1
FEATURE [Part::Cylinder] Cylinder1398  label="Válec1398"
  Angle = 360
  AttacherType = Attacher::AttachEngine3D
  Height = 2
  Placement = pos=(-4,-4,-88) rot=(0,0,1;0rad)
  Radius = 2
FEATURE [Part::Cylinder] Cylinder1399  label="Válec1399"
  Angle = 360
  AttacherType = Attacher::AttachEngine3D
  Height = 20
  Placement = pos=(-4,-4,-88) rot=(0,0,1;0rad)
  Radius = 1
FEATURE [Part::Cylinder] Cylinder1400  label="Válec1400"
  Angle = 360
  AttacherType = Attacher::AttachEngine3D
  Height = 2
  Placement = pos=(-4,4,-88) rot=(0,0,-1;1.5708rad)
  Radius = 2
FEATURE [Part::Cylinder] Cylinder1401  label="Válec1401"
  Angle = 360
  AttacherType = Attacher::AttachEngine3D
  Height = 2
  Placement = pos=(4,4,-88) rot=(0,0,1;3.14159rad)
  Radius = 2
FEATURE [Part::Cylinder] Cylinder1402  label="Válec1402"
  Angle = 360
  AttacherType = Attacher::AttachEngine3D
  Height = 20
  Placement = pos=(4,-4,-88) rot=(0,0,1;1.5708rad)
  Radius = 1
FEATURE [Part::Cylinder] Cylinder1403  label="Válec1403"
  Angle = 360
  AttacherType = Attacher::AttachEngine3D
  Height = 20
  Placement = pos=(4,-4,-88) rot=(0,0,1;1.5708rad)
  Radius = 1
FEATURE [Part::Cylinder] Cylinder1404  label="Válec1404"
  Angle = 360
  AttacherType = Attacher::AttachEngine3D
  Height = 2
  Placement = pos=(4,-4,-88) rot=(0,0,1;1.5708rad)
  Radius = 2
FEATURE [Part::Cylinder] Cylinder1405  label="Válec1405"
  Angle = 360
  AttacherType = Attacher::AttachEngine3D
  Height = 20
  Placement = pos=(4,4,-88) rot=(0,0,1;3.14159rad)
  Radius = 1
FEATURE [Part::Cylinder] Cylinder1406  label="Válec1406"
  Angle = 360
  AttacherType = Attacher::AttachEngine3D
  Height = 20
  Placement = pos=(-4,4,-88) rot=(0,0,-1;1.5708rad)
  Radius = 1
FEATURE [Part::Cylinder] Cylinder1407  label="Válec1407"
  Angle = 360
  AttacherType = Attacher::AttachEngine3D
  Height = 20
  Placement = pos=(4,4,-88) rot=(0,0,1;3.14159rad)
  Radius = 1
FEATURE [Part::Cylinder] Cylinder1408  label="Válec1408"
  Angle = 360
  AttacherType = Attacher::AttachEngine3D
  Height = 20
  Placement = pos=(-4,-4,-88) rot=(0,0,1;0rad)
  Radius = 1
FEATURE [Part::Compound] Compound960
  Links = -> [Cylinder1408,Cylinder1396,Cylinder1393,Cylinder1395]
  Placement = pos=(0,0,91) rot=(0,0,1;0rad)
FEATURE [Part::Cylinder] Cylinder1409  label="Válec1409"
  Angle = 360
  AttacherType = Attacher::AttachEngine3D
  Height = 20
  Placement = pos=(-4,-4,-88) rot=(0,0,1;0rad)
  Radius = 1
FEATURE [Part::Compound] Compound961
  Links = -> [Cylinder1399,Cylinder1403,Cylinder1405,Cylinder1406]
  Placement = pos=(0,0,91) rot=(0,0,1;0rad)
FEATURE [Part::Compound] Compound963
  Links = -> [Wedge054,Wedge052,Wedge055,Wedge053]
FEATURE [Part::Compound] Compound964
  Links = -> [Cylinder1398,Cylinder1404,Cylinder1401,Cylinder1400]
  Placement = pos=(0,0,91) rot=(0,0,1;0rad)
FEATURE [Part::FeaturePython] Tube129  # WARN: FeaturePython — macro-defined, semantics opaque (R4)
  AttacherType = Attacher::AttachEngine3D
  Height = 10
  InnerRadius = 2.75
  OuterRadius = 7.5
  Placement = pos=(0,0,19) rot=(0,0,1;0rad)
FEATURE [Part::Cut] Cut504
  Base = -> Tube129
  Tool = -> Compound961
FEATURE [Part::FeaturePython] wormgear077  # WARN: FeaturePython — macro-defined, semantics opaque (R4)
  AttacherType = Attacher::AttachEngine3D
  Placement = pos=(0,0,29) rot=(0,0,1;0.994838rad)
  beta = 43.4518
  clearance = 0.25
  diameter = 19
  head = 0.25
  height = 8
  module = 1.5
  pressure_angle = 20
  reverse_pitch = false
  teeth = 12
  version = 0.0.3
FEATURE [Part::FeaturePython] Tube130  # WARN: FeaturePython — macro-defined, semantics opaque (R4)
  AttacherType = Attacher::AttachEngine3D
  Height = 12
  InnerRadius = 3.75
  OuterRadius = 7.5
  Placement = pos=(0,0,12) rot=(0,0,1;0rad)
FEATURE [Part::Cylinder] Cylinder1410  label="Válec1410"
  Angle = 360
  AttacherType = Attacher::AttachEngine3D
  Height = 60
  Placement = pos=(0,0,-10) rot=(0,0,1;0rad)
  Radius = 2.75
FEATURE [Part::Cut] Cut506
  Base = -> wormgear077
  Tool = -> Cylinder1410
FEATURE [Part::Compound] Compound965
  Links = -> [Cylinder1409,Cylinder1402,Cylinder1407,Cylinder1397]
  Placement = pos=(0,0,91) rot=(0,0,1;0rad)
FEATURE [Part::Cut] Cut505
  Base = -> Cylinder1394
  Tool = -> Compound965
FEATURE [Part::Cut] Cut509
  Base = -> Tube130
  Placement = pos=(0,0,-9) rot=(0,0,1;0rad)
  Tool = -> Compound963
FEATURE [Part::Chamfer] Chamfer038
  Base = -> Cut509
  Edges = 8 edges r=1: [Edge7,Edge8,Edge21,Edge22,Edge31,Edge32,Edge45,Edge46]
FEATURE [Part::Cut] Cut508
  Base = -> Chamfer038
  Tool = -> Compound964
FEATURE [Part::Cut] Cut507
  Base = -> Cut508
  Tool = -> Compound960
FEATURE [Part::Compound] Compound962  label="J-midi-thin_inner-planeo-m1.5-reinforced_v5.8"
  Links = -> [Cut506,Cut507,Cut505,Cut504]
  Placement = pos=(0,0,-4) rot=(0,0,1;0rad)
FEATURE [Part::Cylinder] Cylinder1411  label="Válec1411"
  Angle = 360
  AttacherType = Attacher::AttachEngine3D
  Height = 32
  Placement = pos=(-29.6985,-29.6985,33.5) rot=(0,0,-1;0.785398rad)
  Radius = 1.5
FEATURE [Part::Cylinder] Cylinder1412  label="Válec1412"
  Angle = 360
  AttacherType = Attacher::AttachEngine3D
  Height = 32
  Placement = pos=(-29.6985,29.6985,33.5) rot=(0,0,1;3.92699rad)
  Radius = 1.5
FEATURE [Part::Box] Box584  label="Krychle584"
  AttacherType = Attacher::AttachEngine3D
  Height = 2
  Length = 6
  Placement = pos=(-34.6482,-30.4056,33) rot=(0,0,-1;0.785398rad)
  Width = 8
FEATURE [Part::Box] Box585  label="Krychle585"
  AttacherType = Attacher::AttachEngine3D
  Height = 2
  Length = 6
  Placement = pos=(-3,-46,33) rot=(0,0,1;0rad)
  Width = 8
FEATURE [Part::Box] Box586  label="Krychle586"
  AttacherType = Attacher::AttachEngine3D
  Height = 2
  Length = 6
  Placement = pos=(46,-3,33) rot=(0,0,1;1.5708rad)
  Width = 8
FEATURE [Part::Box] Box587  label="Krychle587"
  AttacherType = Attacher::AttachEngine3D
  Height = 2
  Length = 6
  Placement = pos=(-30.4056,34.6482,33) rot=(0,0,1;3.92699rad)
  Width = 8
FEATURE [Part::Cylinder] Cylinder1413  label="Válec1413"
  Angle = 360
  AttacherType = Attacher::AttachEngine3D
  Height = 32
  Placement = pos=(0,-42,33.5) rot=(0,0,1;0rad)
  Radius = 1.5
FEATURE [Part::Cylinder] Cylinder1414  label="Válec1414"
  Angle = 360
  AttacherType = Attacher::AttachEngine3D
  Height = 32
  Placement = pos=(-1.4e-14,42,33.5) rot=(0,0,1;3.14159rad)
  Radius = 1.5
FEATURE [Part::Box] Box588  label="Krychle588"
  AttacherType = Attacher::AttachEngine3D
  Height = 2
  Length = 6
  Placement = pos=(30.4056,-34.6482,33) rot=(0,0,1;0.785398rad)
  Width = 8
FEATURE [Part::Box] Box589  label="Krychle589"
  AttacherType = Attacher::AttachEngine3D
  Height = 2
  Length = 6
  Placement = pos=(34.6482,30.4056,33) rot=(0,0,1;2.35619rad)
  Width = 8
FEATURE [Part::Cylinder] Cylinder1415  label="Válec1415"
  Angle = 360
  AttacherType = Attacher::AttachEngine3D
  Height = 32
  Placement = pos=(29.6985,-29.6985,33.5) rot=(0,0,1;0.785398rad)
  Radius = 1.5
FEATURE [Part::Cylinder] Cylinder1416  label="Válec1416"
  Angle = 360
  AttacherType = Attacher::AttachEngine3D
  Height = 32
  Placement = pos=(29.6985,29.6985,33.5) rot=(0,0,1;2.35619rad)
  Radius = 1.5
FEATURE [Part::Cylinder] Cylinder1417  label="Válec1417"
  Angle = 360
  AttacherType = Attacher::AttachEngine3D
  Height = 32
  Placement = pos=(-42,-2.4e-14,33.5) rot=(0,0,-1;1.5708rad)
  Radius = 1.5
FEATURE [Part::Cylinder] Cylinder1418  label="Válec1418"
  Angle = 360
  AttacherType = Attacher::AttachEngine3D
  Height = 32
  Placement = pos=(42,6e-15,33.5) rot=(0,0,1;1.5708rad)
  Radius = 1.5
FEATURE [Part::Compound] Compound967
  Links = -> [Cylinder1413,Cylinder1415,Cylinder1418,Cylinder1416,Cylinder1414,Cylinder1412,Cylinder1417,Cylinder1411]
  Placement = pos=(0,0,0) rot=(0,0,1;0.392699rad)
FEATURE [Part::Box] Box590  label="Krychle590"
  AttacherType = Attacher::AttachEngine3D
  Height = 2
  Length = 6
  Placement = pos=(3,46,33) rot=(0,0,1;3.14159rad)
  Width = 8
FEATURE [Part::Box] Box591  label="Krychle591"
  AttacherType = Attacher::AttachEngine3D
  Height = 2
  Length = 6
  Placement = pos=(-46,3,33) rot=(0,0,-1;1.5708rad)
  Width = 8
FEATURE [Part::Compound] Compound966
  Links = -> [Box584,Box588,Box586,Box585,Box589,Box590,Box587,Box591]
  Placement = pos=(0,0,4.4) rot=(0,0,1;0.392699rad)
FEATURE [Part::Box] Box592  label="Krychle592"
  AttacherType = Attacher::AttachEngine3D
  Height = 2
  Length = 6
  Placement = pos=(3,46,33) rot=(0,0,1;3.14159rad)
  Width = 8
FEATURE [Part::Box] Box593  label="Krychle593"
  AttacherType = Attacher::AttachEngine3D
  Height = 2
  Length = 6
  Placement = pos=(30.4056,-34.6482,33) rot=(0,0,1;0.785398rad)
  Width = 8
FEATURE [Part::FeaturePython] Tube131  # WARN: FeaturePython — macro-defined, semantics opaque (R4)
  AttacherType = Attacher::AttachEngine3D
  Height = 16
  InnerRadius = 40
  OuterRadius = 46
  Placement = pos=(0,0,26) rot=(0,0,1;0rad)
FEATURE [Part::FeaturePython] Tube132  label="ZKL-61816-008"  # WARN: FeaturePython — macro-defined, semantics opaque (R4)
  AttacherType = Attacher::AttachEngine3D
  Height = 11
  InnerRadius = 40
  OuterRadius = 50
  Placement = pos=(0,0,25.4) rot=(0,0,1;0rad)
FEATURE [Part::Cut] Cut513
  Base = -> Tube131
  Tool = -> Tube132
FEATURE [Part::Cut] Cut515
  Base = -> Cut513
  Tool = -> Compound967
FEATURE [Part::Cut] Cut516
  Base = -> Cut515
  Placement = pos=(0,0,3) rot=(0,0,1;0rad)
  Tool = -> Compound966
FEATURE [Part::FeaturePython] wormgear078  # WARN: FeaturePython — macro-defined, semantics opaque (R4)
  AttacherType = Attacher::AttachEngine3D
  Placement = pos=(0,0,0) rot=(0,0,1;0.10472rad)
  beta = 38.5565
  clearance = 0.25
  diameter = 67.75
  head = 0
  height = 14
  module = 1.5
  pressure_angle = 20
  reverse_pitch = true
  teeth = 36
  version = 0.0.3
FEATURE [Part::FeaturePython] wormgear079  # WARN: FeaturePython — macro-defined, semantics opaque (R4)
  AttacherType = Attacher::AttachEngine3D
  Placement = pos=(0,0,0) rot=(0,0,-1;0.1309rad)
  beta = 38.5565
  clearance = 0.25
  diameter = 67.75
  head = 0
  height = 14
  module = 1.5
  pressure_angle = 20
  reverse_pitch = false
  teeth = 36
  version = 0.0.3
FEATURE [Part::FeaturePython] Tube133  label="ZKL-61816-009"  # WARN: FeaturePython — macro-defined, semantics opaque (R4)
  AttacherType = Attacher::AttachEngine3D
  Height = 11
  InnerRadius = 40
  OuterRadius = 50
  Placement = pos=(0,0,25) rot=(0,0,1;0rad)
FEATURE [Part::FeaturePython] Tube134  label="ZKL-61816-subwasher002"  # WARN: FeaturePython — macro-defined, semantics opaque (R4)
  AttacherType = Attacher::AttachEngine3D
  Height = 0.4
  InnerRadius = 40
  OuterRadius = 42
  Placement = pos=(0,0,38) rot=(0,0,1;0rad)
FEATURE [Part::Cylinder] Cylinder1419  label="Válec1419"
  Angle = 360
  AttacherType = Attacher::AttachEngine3D
  Height = 8
  Radius = 40
FEATURE [Part::Cut] Cut510
  Base = -> Cylinder1419
  Placement = pos=(0,0,25) rot=(0,0,1;0.294961rad)
  Tool = -> wormgear079
FEATURE [Part::Box] Box594  label="Krychle594"
  AttacherType = Attacher::AttachEngine3D
  Height = 2
  Length = 6
  Placement = pos=(-34.6482,-30.4056,33) rot=(0,0,-1;0.785398rad)
  Width = 8
FEATURE [Part::Box] Box595  label="Krychle595"
  AttacherType = Attacher::AttachEngine3D
  Height = 2
  Length = 6
  Placement = pos=(34.6482,30.4056,33) rot=(0,0,1;2.35619rad)
  Width = 8
FEATURE [Part::Box] Box596  label="Krychle596"
  AttacherType = Attacher::AttachEngine3D
  Height = 2
  Length = 6
  Placement = pos=(-3,-46,33) rot=(0,0,1;0rad)
  Width = 8
FEATURE [Part::Box] Box597  label="Krychle597"
  AttacherType = Attacher::AttachEngine3D
  Height = 2
  Length = 6
  Placement = pos=(-30.4056,34.6482,33) rot=(0,0,1;3.92699rad)
  Width = 8
FEATURE [Part::Cylinder] Cylinder1420  label="Válec1420"
  Angle = 360
  AttacherType = Attacher::AttachEngine3D
  Height = 8
  Radius = 40
FEATURE [Part::Cut] Cut511
  Base = -> Cylinder1420
  Placement = pos=(0,0,33) rot=(0,0,1;0.53058rad)
  Tool = -> wormgear078
FEATURE [Part::Box] Box598  label="Krychle598"
  AttacherType = Attacher::AttachEngine3D
  Height = 2
  Length = 6
  Placement = pos=(-46,3,33) rot=(0,0,-1;1.5708rad)
  Width = 8
FEATURE [Part::Box] Box599  label="Krychle599"
  AttacherType = Attacher::AttachEngine3D
  Height = 2
  Length = 6
  Placement = pos=(46,-3,33) rot=(0,0,1;1.5708rad)
  Width = 8
FEATURE [Part::Compound] Compound968
  Links = -> [Box594,Box593,Box599,Box596,Box595,Box592,Box597,Box598]
  Placement = pos=(0,0,3.4) rot=(0,0,1;0.392699rad)
FEATURE [Part::Cut] Cut512
  Base = -> Cut511
  Tool = -> Compound968
FEATURE [Part::Compound] Compound969
  Links = -> [Cut512,Cut510]
  Placement = pos=(0,0,4) rot=(0,0,1;0rad)
FEATURE [Part::Cut] Cut514
  Base = -> Compound969
  Tool = -> Tube133
FEATURE [Part::Cylinder] Cylinder1421  label="Válec1421"
  Angle = 360
  AttacherType = Attacher::AttachEngine3D
  Height = 32
  Placement = pos=(-29.6985,-29.6985,33.5) rot=(0,0,-1;0.785398rad)
  Radius = 1.5
FEATURE [Part::Cylinder] Cylinder1422  label="Válec1422"
  Angle = 360
  AttacherType = Attacher::AttachEngine3D
  Height = 32
  Placement = pos=(-29.6985,29.6985,33.5) rot=(0,0,1;3.92699rad)
  Radius = 1.5
FEATURE [Part::Cylinder] Cylinder1423  label="Válec1423"
  Angle = 360
  AttacherType = Attacher::AttachEngine3D
  Height = 32
  Placement = pos=(0,-42,33.5) rot=(0,0,1;0rad)
  Radius = 1.5
FEATURE [Part::Cylinder] Cylinder1424  label="Válec1424"
  Angle = 360
  AttacherType = Attacher::AttachEngine3D
  Height = 32
  Placement = pos=(-1.4e-14,42,33.5) rot=(0,0,1;3.14159rad)
  Radius = 1.5
FEATURE [Part::Cylinder] Cylinder1425  label="Válec1425"
  Angle = 360
  AttacherType = Attacher::AttachEngine3D
  Height = 32
  Placement = pos=(29.6985,-29.6985,33.5) rot=(0,0,1;0.785398rad)
  Radius = 1.5
FEATURE [Part::Cylinder] Cylinder1426  label="Válec1426"
  Angle = 360
  AttacherType = Attacher::AttachEngine3D
  Height = 32
  Placement = pos=(29.6985,29.6985,33.5) rot=(0,0,1;2.35619rad)
  Radius = 1.5
FEATURE [Part::Cylinder] Cylinder1427  label="Válec1427"
  Angle = 360
  AttacherType = Attacher::AttachEngine3D
  Height = 32
  Placement = pos=(-42,-2.4e-14,33.5) rot=(0,0,-1;1.5708rad)
  Radius = 1.5
FEATURE [Part::Cylinder] Cylinder1428  label="Válec1428"
  Angle = 360
  AttacherType = Attacher::AttachEngine3D
  Height = 32
  Placement = pos=(42,6e-15,33.5) rot=(0,0,1;1.5708rad)
  Radius = 1.5
FEATURE [Part::Compound] Compound970
  Links = -> [Cylinder1423,Cylinder1425,Cylinder1428,Cylinder1426,Cylinder1424,Cylinder1422,Cylinder1427,Cylinder1421]
  Placement = pos=(0,0,0) rot=(0,0,1;0.392699rad)
FEATURE [Part::Cut] Cut517
  Base = -> Tube134
  Placement = pos=(0,0,1) rot=(0,0,1;0rad)
  Tool = -> Compound970
FEATURE [Part::Compound] Compound971  label="J-midi-thin_actuator_v1.6"
  Links = -> [Cut517,Cut516,Cut514]
FEATURE [Part::FeaturePython] wormgear080  # WARN: FeaturePython — macro-defined, semantics opaque (R4)
  AttacherType = Attacher::AttachEngine3D
  beta = 39.0939
  clearance = 0.25
  diameter = 72
  head = 0
  height = 20
  module = 1.5
  pressure_angle = 20
  reverse_pitch = false
  teeth = 39
  version = 0.0.3
FEATURE [Part::FeaturePython] wormgear081  # WARN: FeaturePython — macro-defined, semantics opaque (R4)
  AttacherType = Attacher::AttachEngine3D
  Placement = pos=(0,0,0) rot=(0,0,-1;0.176278rad)
  beta = 39.0939
  clearance = 0.25
  diameter = 72
  head = 0
  height = 20
  module = 1.5
  pressure_angle = 20
  reverse_pitch = true
  teeth = 39
  version = 0.0.3
FEATURE [Part::Cylinder] Cylinder1429  label="Válec1429"
  Angle = 360
  AttacherType = Attacher::AttachEngine3D
  Height = 10
  Radius = 46
FEATURE [Part::Cylinder] Cylinder1430  label="Válec1430"
  Angle = 360
  AttacherType = Attacher::AttachEngine3D
  Height = 10
  Radius = 54
FEATURE [Part::Cut] Cut518
  Base = -> Cylinder1429
  Placement = pos=(0,0,2) rot=(0,0,1;0rad)
  Tool = -> wormgear080
FEATURE [Part::Cut] Cut519
  Base = -> Cylinder1430
  Placement = pos=(0,0,12) rot=(0,0,1;0.034907rad)
  Tool = -> wormgear081
FEATURE [Part::Compound] Compound972
  Links = -> [Cut519,Cut518]
FEATURE [Part::Cylinder] Cylinder1431  label="Válec1431"
  Angle = 360
  AttacherType = Attacher::AttachEngine3D
  Height = 50
  Placement = pos=(-7e-15,52,0) rot=(0,0,1;1.5708rad)
  Radius = 1.5
FEATURE [Part::Cylinder] Cylinder1432  label="Válec1432"
  Angle = 360
  AttacherType = Attacher::AttachEngine3D
  Height = 50
  Placement = pos=(52,0,0) rot=(0,0,1;0rad)
  Radius = 1.5
FEATURE [Part::Cylinder] Cylinder1433  label="Válec1433"
  Angle = 360
  AttacherType = Attacher::AttachEngine3D
  Height = 50
  Placement = pos=(36.7696,36.7696,0) rot=(0,0,1;0.785398rad)
  Radius = 1.5
FEATURE [Part::Cylinder] Cylinder1434  label="Válec1434"
  Angle = 360
  AttacherType = Attacher::AttachEngine3D
  Height = 50
  Placement = pos=(-52,-2.1e-14,0) rot=(0,0,1;3.14159rad)
  Radius = 1.5
FEATURE [Part::Cylinder] Cylinder1435  label="Válec1435"
  Angle = 360
  AttacherType = Attacher::AttachEngine3D
  Height = 50
  Placement = pos=(-36.7696,-36.7696,0) rot=(0,0,1;3.92699rad)
  Radius = 1.5
FEATURE [Part::Cylinder] Cylinder1436  label="Válec1436"
  Angle = 360
  AttacherType = Attacher::AttachEngine3D
  Height = 50
  Placement = pos=(2e-14,-52,0) rot=(0,0,-1;1.5708rad)
  Radius = 1.5
FEATURE [Part::Cylinder] Cylinder1437  label="Válec1437"
  Angle = 360
  AttacherType = Attacher::AttachEngine3D
  Height = 50
  Placement = pos=(36.7696,-36.7696,0) rot=(0,0,-1;0.785398rad)
  Radius = 1.5
FEATURE [Part::Cylinder] Cylinder1438  label="Válec1438"
  Angle = 360
  AttacherType = Attacher::AttachEngine3D
  Height = 50
  Placement = pos=(-36.7696,36.7696,0) rot=(0,0,1;2.35619rad)
  Radius = 1.5
FEATURE [Part::Compound] Compound973
  Links = -> [Cylinder1432,Cylinder1433,Cylinder1431,Cylinder1438,Cylinder1434,Cylinder1435,Cylinder1436,Cylinder1437]
  Placement = pos=(0,0,-7) rot=(0,0,1;0rad)
FEATURE [Part::Box] Box600  label="Krychle600"
  AttacherType = Attacher::AttachEngine3D
  Height = 10
  Length = 4
  Placement = pos=(51,-6,12) rot=(0,0,1;0rad)
  Width = 12
FEATURE [Part::Chamfer] Chamfer039
  Base = -> Box600
  Edges = 2 edges r=2: [Edge5,Edge7]
FEATURE [Part::Chamfer] Chamfer040
  Base = -> Box600
  Edges = 2 edges r=2: [Edge5,Edge7]
  Placement = pos=(0,0,0) rot=(0,0,1;0.785398rad)
FEATURE [Part::Chamfer] Chamfer041
  Base = -> Box600
  Edges = 2 edges r=2: [Edge5,Edge7]
  Placement = pos=(0,0,0) rot=(0,0,1;1.5708rad)
FEATURE [Part::Chamfer] Chamfer042
  Base = -> Box600
  Edges = 2 edges r=2: [Edge5,Edge7]
  Placement = pos=(0,0,0) rot=(0,0,1;2.35619rad)
FEATURE [Part::Chamfer] Chamfer043
  Base = -> Box600
  Edges = 2 edges r=2: [Edge5,Edge7]
  Placement = pos=(0,0,0) rot=(0,0,1;3.14159rad)
FEATURE [Part::Chamfer] Chamfer044
  Base = -> Box600
  Edges = 2 edges r=2: [Edge5,Edge7]
  Placement = pos=(0,0,0) rot=(0,0,1;3.92699rad)
FEATURE [Part::Chamfer] Chamfer045
  Base = -> Box600
  Edges = 2 edges r=2: [Edge5,Edge7]
  Placement = pos=(0,0,0) rot=(0,0,-1;1.5708rad)
FEATURE [Part::Cylinder] Cylinder1439  label="Válec1439"
  Angle = 360
  AttacherType = Attacher::AttachEngine3D
  Height = 50
  Placement = pos=(36.7696,36.7696,0) rot=(0,0,1;0.785398rad)
  Radius = 1.5
FEATURE [Part::Cylinder] Cylinder1440  label="Válec1440"
  Angle = 360
  AttacherType = Attacher::AttachEngine3D
  Height = 50
  Placement = pos=(36.7696,-36.7696,0) rot=(0,0,-1;0.785398rad)
  Radius = 1.5
FEATURE [Part::Cylinder] Cylinder1441  label="Válec1441"
  Angle = 360
  AttacherType = Attacher::AttachEngine3D
  Height = 50
  Placement = pos=(52,0,0) rot=(0,0,1;0rad)
  Radius = 1.5
FEATURE [Part::Cylinder] Cylinder1442  label="Válec1442"
  Angle = 360
  AttacherType = Attacher::AttachEngine3D
  Height = 50
  Placement = pos=(-52,-2.1e-14,0) rot=(0,0,1;3.14159rad)
  Radius = 1.5
FEATURE [Part::Cylinder] Cylinder1443  label="Válec1443"
  Angle = 360
  AttacherType = Attacher::AttachEngine3D
  Height = 50
  Placement = pos=(-36.7696,-36.7696,0) rot=(0,0,1;3.92699rad)
  Radius = 1.5
FEATURE [Part::Cylinder] Cylinder1444  label="Válec1444"
  Angle = 360
  AttacherType = Attacher::AttachEngine3D
  Height = 50
  Placement = pos=(-7e-15,52,0) rot=(0,0,1;1.5708rad)
  Radius = 1.5
FEATURE [Part::Cylinder] Cylinder1445  label="Válec1445"
  Angle = 360
  AttacherType = Attacher::AttachEngine3D
  Height = 50
  Placement = pos=(2e-14,-52,0) rot=(0,0,-1;1.5708rad)
  Radius = 1.5
FEATURE [Part::Cylinder] Cylinder1446  label="Válec1446"
  Angle = 360
  AttacherType = Attacher::AttachEngine3D
  Height = 50
  Placement = pos=(-36.7696,36.7696,0) rot=(0,0,1;2.35619rad)
  Radius = 1.5
FEATURE [Part::Cylinder] Cylinder1447  label="Válec1447"
  Angle = 360
  AttacherType = Attacher::AttachEngine3D
  Height = 40
  Placement = pos=(214,56,-30) rot=(0,0,1;0rad)
  Radius = 12
FEATURE [Part::Cylinder] Cylinder1448  label="Válec1448"
  Angle = 360
  AttacherType = Attacher::AttachEngine3D
  Height = 40
  Placement = pos=(202,50,-28) rot=(0,0,1;0rad)
  Radius = 12
FEATURE [Part::Cylinder] Cylinder1449  label="Válec1449"
  Angle = 360
  AttacherType = Attacher::AttachEngine3D
  Height = 40
  Placement = pos=(202,50,-28) rot=(0,0,1;0rad)
  Radius = 12
FEATURE [Part::Box] Box601  label="Krychle601"
  AttacherType = Attacher::AttachEngine3D
  Height = 28
  Length = 6
  Placement = pos=(26,28,-6) rot=(0,0,1;0rad)
  Width = 10
FEATURE [Part::Cylinder] Cylinder1450  label="Válec1450"
  Angle = 360
  AttacherType = Attacher::AttachEngine3D
  Height = 40
  Placement = pos=(256,0,-30) rot=(0,0,1;0rad)
  Radius = 10
FEATURE [Part::Box] Box602  label="Krychle602"
  AttacherType = Attacher::AttachEngine3D
  Height = 28
  Length = 8
  Placement = pos=(238,0,-6) rot=(0,0,1;0rad)
  Width = 38
FEATURE [Part::Box] Box603  label="Krychle603"
  AttacherType = Attacher::AttachEngine3D
  Height = 2
  Length = 8
  Placement = pos=(37,-3,-4) rot=(0,0,1;0rad)
  Width = 6
FEATURE [Part::Box] Box604  label="Krychle604"
  AttacherType = Attacher::AttachEngine3D
  Height = 28
  Length = 6
  Placement = pos=(32,24,-6) rot=(0,0,1;0rad)
  Width = 14
FEATURE [Part::Cylinder] Cylinder1451  label="Válec1451"
  Angle = 360
  AttacherType = Attacher::AttachEngine3D
  Height = 40
  Placement = pos=(214,56,-30) rot=(0,0,1;0rad)
  Radius = 12
FEATURE [Part::Box] Box605  label="Krychle605"
  AttacherType = Attacher::AttachEngine3D
  Height = 28
  Length = 46
  Placement = pos=(200,38,-6) rot=(0,0,1;0rad)
  Width = 16
FEATURE [Part::Box] Box606  label="Krychle606"
  AttacherType = Attacher::AttachEngine3D
  Height = 28
  Length = 8
  Placement = pos=(238,0,-6) rot=(0,0,1;0rad)
  Width = 38
FEATURE [Part::Box] Box607  label="Krychle607"
  AttacherType = Attacher::AttachEngine3D
  Height = 28
  Length = 6
  Placement = pos=(26,28,-6) rot=(0,0,1;0rad)
  Width = 10
FEATURE [Part::Box] Box608  label="Krychle608"
  AttacherType = Attacher::AttachEngine3D
  Height = 28
  Length = 6
  Placement = pos=(32,24,-6) rot=(0,0,1;0rad)
  Width = 14
FEATURE [Part::Cylinder] Cylinder1452  label="Válec1452"
  Angle = 360
  AttacherType = Attacher::AttachEngine3D
  Height = 60
  Placement = pos=(1.2e-14,-41,-54) rot=(0,0,-1;1.5708rad)
  Radius = 1.5
FEATURE [Part::Box] Box609  label="Krychle609"
  AttacherType = Attacher::AttachEngine3D
  Height = 2
  Length = 8
  Placement = pos=(3,37,-4) rot=(0,0,1;1.5708rad)
  Width = 6
FEATURE [Part::Chamfer] Chamfer046
  Base = -> Box600
  Edges = 2 edges r=2: [Edge5,Edge7]
  Placement = pos=(0,0,0) rot=(0,0,-1;0.785398rad)
FEATURE [Part::Compound] Compound974
  Links = -> [Chamfer039,Chamfer040,Chamfer041,Chamfer042,Chamfer043,Chamfer044,Chamfer045,Chamfer046]
FEATURE [Part::Cut] Cut520
  Base = -> Compound974
  Tool = -> Compound973
FEATURE [Part::Compound] Compound975
  Links = -> [Cylinder1441,Cylinder1439,Cylinder1444,Cylinder1446,Cylinder1442,Cylinder1443,Cylinder1445,Cylinder1440]
  Placement = pos=(0,0,-7) rot=(0,0,1;0rad)
FEATURE [Part::Cut] Cut521
  Base = -> Compound972
  Tool = -> Compound975
FEATURE [Part::Compound] Compound980
  Links = -> [Box601,Box604]
FEATURE [Part::Compound] Compound981
  Links = -> [Cylinder1450,Cylinder1451]
  Placement = pos=(0,0,2) rot=(0,0,1;0rad)
FEATURE [Part::Compound] Compound983
  Links = -> [Box606,Box605]
FEATURE [Part::Cut] Cut523
  Base = -> Compound983
  Tool = -> Compound981
FEATURE [Part::Compound] Compound986
  Links = -> [Box607,Box608]
FEATURE [Part::Cut] Cut528
  Base = -> Cut523
  Placement = pos=(-200,0,0) rot=(0,0,1;0rad)
  Tool = -> Cylinder1448
FEATURE [Part::Compound] Compound984
  Links = -> [Cut528,Compound986]
FEATURE [Part::Box] Box610  label="Krychle610"
  AttacherType = Attacher::AttachEngine3D
  Height = 2
  Length = 8
  Placement = pos=(28.2843,24.0416,-4) rot=(0,0,1;0.785398rad)
  Width = 6
FEATURE [Part::Box] Box611  label="Krychle611"
  AttacherType = Attacher::AttachEngine3D
  Height = 2
  Length = 8
  Placement = pos=(-24.0416,28.2843,-4) rot=(0,0,1;2.35619rad)
  Width = 6
FEATURE [Part::Box] Box612  label="Krychle612"
  AttacherType = Attacher::AttachEngine3D
  Height = 2
  Length = 8
  Placement = pos=(-3,-37,-4) rot=(0,0,-1;1.5708rad)
  Width = 6
FEATURE [Part::Cylinder] Cylinder1453  label="Válec1453"
  Angle = 360
  AttacherType = Attacher::AttachEngine3D
  Height = 40
  Placement = pos=(256,0,-30) rot=(0,0,1;0rad)
  Radius = 10
FEATURE [Part::Compound] Compound985
  Links = -> [Cylinder1453,Cylinder1447]
  Placement = pos=(0,0,2) rot=(0,0,1;0rad)
FEATURE [Part::Box] Box613  label="Krychle613"
  AttacherType = Attacher::AttachEngine3D
  Height = 28
  Length = 46
  Placement = pos=(200,38,-6) rot=(0,0,1;0rad)
  Width = 16
FEATURE [Part::Compound] Compound982
  Links = -> [Box602,Box613]
FEATURE [Part::Cut] Cut524
  Base = -> Compound982
  Tool = -> Compound985
FEATURE [Part::Cut] Cut526
  Base = -> Cut524
  Placement = pos=(-200,0,0) rot=(0,0,1;0rad)
  Tool = -> Cylinder1449
FEATURE [Part::Compound] Compound979
  Links = -> [Cut526,Compound980]
FEATURE [Part::Mirroring] mirror014  label="Compound196 (mirrored)003"
  Base = (0,0,0)
  Normal = (1e-16,-1,0)
  Source = -> Compound979
FEATURE [Part::Cylinder] Cylinder1454  label="Válec1454"
  Angle = 360
  AttacherType = Attacher::AttachEngine3D
  Height = 60
  Placement = pos=(28.9914,-28.9914,-54) rot=(0,0,-1;0.785398rad)
  Radius = 1.5
FEATURE [Part::Cylinder] Cylinder1455  label="Válec1455"
  Angle = 360
  AttacherType = Attacher::AttachEngine3D
  Height = 60
  Placement = pos=(41,0,-54) rot=(0,0,1;0rad)
  Radius = 1.5
FEATURE [Part::Box] Box614  label="Krychle614"
  AttacherType = Attacher::AttachEngine3D
  Height = 2
  Length = 8
  Placement = pos=(24.0416,-28.2843,-4) rot=(0,0,-1;0.785398rad)
  Width = 6
FEATURE [Part::Cylinder] Cylinder1456  label="Válec1456"
  Angle = 360
  AttacherType = Attacher::AttachEngine3D
  Height = 60
  Placement = pos=(28.9914,28.9914,-54) rot=(0,0,1;0.785398rad)
  Radius = 1.5
FEATURE [Part::Box] Box615  label="Krychle615"
  AttacherType = Attacher::AttachEngine3D
  Height = 2
  Length = 8
  Placement = pos=(-37,3,-4) rot=(0,0,1;3.14159rad)
  Width = 6
FEATURE [Part::Cylinder] Cylinder1457  label="Válec1457"
  Angle = 360
  AttacherType = Attacher::AttachEngine3D
  Height = 60
  Placement = pos=(-28.9914,28.9914,-54) rot=(0,0,1;2.35619rad)
  Radius = 1.5
FEATURE [Part::Box] Box616  label="Krychle616"
  AttacherType = Attacher::AttachEngine3D
  Height = 2
  Length = 8
  Placement = pos=(-28.2843,-24.0416,-4) rot=(0,0,1;3.92699rad)
  Width = 6
FEATURE [Part::Cylinder] Cylinder1458  label="Válec1458"
  Angle = 360
  AttacherType = Attacher::AttachEngine3D
  Height = 60
  Placement = pos=(-4e-15,41,-54) rot=(0,0,1;1.5708rad)
  Radius = 1.5
FEATURE [Part::Cylinder] Cylinder1459  label="Válec1459"
  Angle = 360
  AttacherType = Attacher::AttachEngine3D
  Height = 60
  Placement = pos=(-28.9914,-28.9914,-54) rot=(0,0,1;3.92699rad)
  Radius = 1.5
FEATURE [Part::Cylinder] Cylinder1460  label="Válec1460"
  Angle = 360
  AttacherType = Attacher::AttachEngine3D
  Height = 60
  Placement = pos=(-41,-1.1e-14,-54) rot=(0,0,1;3.14159rad)
  Radius = 1.5
FEATURE [Part::Compound] Compound978
  Links = -> [Cylinder1456,Cylinder1458,Cylinder1457,Cylinder1460,Cylinder1459,Cylinder1452,Cylinder1454,Cylinder1455]
  Placement = pos=(0,0,0) rot=(0,0,1;0.392699rad)
FEATURE [Part::Cylinder] Cylinder1461  label="Válec1461"
  Angle = 360
  AttacherType = Attacher::AttachEngine3D
  Height = 60
  Placement = pos=(32,51,7) rot=(0,1,0;1.5708rad)
  Radius = 1.5
FEATURE [Part::Box] Box617  label="Krychle617"
  AttacherType = Attacher::AttachEngine3D
  Height = 6
  Length = 2
  Placement = pos=(36,-54,4) rot=(0,0,1;0rad)
  Width = 6
FEATURE [Part::Box] Box618  label="Krychle618"
  AttacherType = Attacher::AttachEngine3D
  Height = 6
  Length = 2
  Placement = pos=(36,-26,-8) rot=(0,0,1;0rad)
  Width = 6
FEATURE [Part::Box] Box619  label="Krychle619"
  AttacherType = Attacher::AttachEngine3D
  Height = 6
  Length = 2
  Placement = pos=(36,20,-8) rot=(0,0,1;0rad)
  Width = 6
FEATURE [Part::Cylinder] Cylinder1462  label="Válec1462"
  Angle = 360
  AttacherType = Attacher::AttachEngine3D
  Height = 50
  Placement = pos=(36.77,36.77,-40) rot=(0,0,1;0.785398rad)
  Radius = 4
FEATURE [Part::Cylinder] Cylinder1463  label="Válec1463"
  Angle = 360
  AttacherType = Attacher::AttachEngine3D
  Height = 60
  Placement = pos=(32,23,-5) rot=(0,1,0;1.5708rad)
  Radius = 1.5
FEATURE [Part::Cylinder] Cylinder1464  label="Válec1464"
  Angle = 360
  AttacherType = Attacher::AttachEngine3D
  Height = 60
  Placement = pos=(32,-23,-5) rot=(0,1,0;1.5708rad)
  Radius = 1.5
FEATURE [Part::Cylinder] Cylinder1465  label="Válec1465"
  Angle = 360
  AttacherType = Attacher::AttachEngine3D
  Height = 60
  Placement = pos=(32,-51,7) rot=(0,1,0;1.5708rad)
  Radius = 1.5
FEATURE [Part::Compound] Compound976
  Links = -> [Cylinder1463,Cylinder1464,Cylinder1461,Cylinder1465]
  Placement = pos=(0,0,2) rot=(0,0,1;0rad)
FEATURE [Part::Cylinder] Cylinder1466  label="Válec1466"
  Angle = 360
  AttacherType = Attacher::AttachEngine3D
  Height = 50
  Placement = pos=(36.77,-36.77,-40) rot=(0,0,1;0.785398rad)
  Radius = 4
FEATURE [Part::Compound] Compound977
  Links = -> [Cylinder1462,Cylinder1466]
  Placement = pos=(0,0,2) rot=(0,0,1;0rad)
FEATURE [Part::Box] Box620  label="Krychle620"
  AttacherType = Attacher::AttachEngine3D
  Height = 6
  Length = 2
  Placement = pos=(36,48,4) rot=(0,0,1;0rad)
  Width = 6
FEATURE [Part::Cylinder] Cylinder1467  label="Válec1467"
  Angle = 360
  AttacherType = Attacher::AttachEngine3D
  Height = 50
  Placement = pos=(-36.7696,36.7696,0) rot=(0,0,1;2.35619rad)
  Radius = 1.5
FEATURE [Part::Cylinder] Cylinder1468  label="Válec1468"
  Angle = 360
  AttacherType = Attacher::AttachEngine3D
  Height = 50
  Placement = pos=(36.7696,36.7696,0) rot=(0,0,1;0.785398rad)
  Radius = 1.5
FEATURE [Part::Cylinder] Cylinder1469  label="Válec1469"
  Angle = 360
  AttacherType = Attacher::AttachEngine3D
  Height = 50
  Placement = pos=(36.7696,-36.7696,0) rot=(0,0,-1;0.785398rad)
  Radius = 1.5
FEATURE [Part::Cylinder] Cylinder1470  label="Válec1470"
  Angle = 360
  AttacherType = Attacher::AttachEngine3D
  Height = 50
  Placement = pos=(-52,-2.1e-14,0) rot=(0,0,1;3.14159rad)
  Radius = 1.5
FEATURE [Part::Cylinder] Cylinder1471  label="Válec1471"
  Angle = 360
  AttacherType = Attacher::AttachEngine3D
  Height = 50
  Placement = pos=(-36.7696,-36.7696,0) rot=(0,0,1;3.92699rad)
  Radius = 1.5
FEATURE [Part::Cylinder] Cylinder1472  label="Válec1472"
  Angle = 360
  AttacherType = Attacher::AttachEngine3D
  Height = 50
  Placement = pos=(52,0,0) rot=(0,0,1;0rad)
  Radius = 1.5
FEATURE [Part::Cylinder] Cylinder1473  label="Válec1473"
  Angle = 360
  AttacherType = Attacher::AttachEngine3D
  Height = 50
  Placement = pos=(-7e-15,52,0) rot=(0,0,1;1.5708rad)
  Radius = 1.5
FEATURE [Part::Cylinder] Cylinder1474  label="Válec1474"
  Angle = 360
  AttacherType = Attacher::AttachEngine3D
  Height = 50
  Placement = pos=(2e-14,-52,0) rot=(0,0,-1;1.5708rad)
  Radius = 1.5
FEATURE [Part::Compound] Compound987
  Links = -> [Cylinder1472,Cylinder1468,Cylinder1473,Cylinder1467,Cylinder1470,Cylinder1471,Cylinder1474,Cylinder1469]
FEATURE [Part::Compound] Compound988
  Links = -> [Box619,Box618,Box620,Box617]
  Placement = pos=(0,0,2) rot=(0,0,1;0rad)
FEATURE [Part::Compound] Compound989
  Links = -> [mirror014,Compound984]
FEATURE [Part::Compound] Compound990
  Links = -> [Box610,Box609,Box611,Box615,Box616,Box612,Box614,Box603]
  Placement = pos=(0,0,2) rot=(0,0,1;0.392699rad)
FEATURE [Part::Cut] Cut525
  Base = -> Compound989
  Tool = -> Compound990
FEATURE [Part::Cut] Cut529
  Base = -> Cut525
  Tool = -> Compound978
FEATURE [Part::Cut] Cut530
  Base = -> Cut529
  Tool = -> Compound987
FEATURE [Part::Cut] Cut527
  Base = -> Cut530
  Tool = -> Compound988
FEATURE [Part::Cut] Cut522
  Base = -> Cut527
  Tool = -> Compound976
FEATURE [Part::Cut] Cut531
  Base = -> Cut522
  Tool = -> Compound977
FEATURE [Part::Fillet] Fillet023
  Base = -> Cut531
  Edges = 2 edges r=12: [Edge83,Edge290]
FEATURE [Part::Cylinder] Cylinder1475  label="Válec1475"
  Angle = 360
  AttacherType = Attacher::AttachEngine3D
  Height = 60
  Placement = pos=(41,0,-54) rot=(0,0,1;0rad)
  Radius = 1.5
FEATURE [Part::Box] Box621  label="Krychle621"
  AttacherType = Attacher::AttachEngine3D
  Height = 2
  Length = 8
  Placement = pos=(37,-3,-4) rot=(0,0,1;0rad)
  Width = 6
FEATURE [Part::Cylinder] Cylinder1476  label="Válec1476"
  Angle = 360
  AttacherType = Attacher::AttachEngine3D
  Height = 60
  Placement = pos=(-41,-1.1e-14,-54) rot=(0,0,1;3.14159rad)
  Radius = 1.5
FEATURE [Part::Cylinder] Cylinder1477  label="Válec1477"
  Angle = 360
  AttacherType = Attacher::AttachEngine3D
  Height = 60
  Placement = pos=(-28.9914,-28.9914,-54) rot=(0,0,1;3.92699rad)
  Radius = 1.5
FEATURE [Part::Box] Box622  label="Krychle622"
  AttacherType = Attacher::AttachEngine3D
  Height = 2
  Length = 8
  Placement = pos=(3,37,-4) rot=(0,0,1;1.5708rad)
  Width = 6
FEATURE [Part::Box] Box623  label="Krychle623"
  AttacherType = Attacher::AttachEngine3D
  Height = 2
  Length = 8
  Placement = pos=(-37,3,-4) rot=(0,0,1;3.14159rad)
  Width = 6
FEATURE [Part::Cylinder] Cylinder1478  label="Válec1478"
  Angle = 360
  AttacherType = Attacher::AttachEngine3D
  Height = 60
  Placement = pos=(28.9914,-28.9914,-54) rot=(0,0,-1;0.785398rad)
  Radius = 1.5
FEATURE [Part::Box] Box624  label="Krychle624"
  AttacherType = Attacher::AttachEngine3D
  Height = 2
  Length = 8
  Placement = pos=(28.2843,24.0416,-4) rot=(0,0,1;0.785398rad)
  Width = 6
FEATURE [Part::Box] Box625  label="Krychle625"
  AttacherType = Attacher::AttachEngine3D
  Height = 2
  Length = 8
  Placement = pos=(-28.2843,-24.0416,-4) rot=(0,0,1;3.92699rad)
  Width = 6
FEATURE [Part::Cylinder] Cylinder1479  label="Válec1479"
  Angle = 360
  AttacherType = Attacher::AttachEngine3D
  Height = 60
  Placement = pos=(28.9914,28.9914,-54) rot=(0,0,1;0.785398rad)
  Radius = 1.5
FEATURE [Part::Box] Box626  label="Krychle626"
  AttacherType = Attacher::AttachEngine3D
  Height = 2
  Length = 8
  Placement = pos=(-3,-37,-4) rot=(0,0,-1;1.5708rad)
  Width = 6
FEATURE [Part::Box] Box627  label="Krychle627"
  AttacherType = Attacher::AttachEngine3D
  Height = 2
  Length = 8
  Placement = pos=(24.0416,-28.2843,-4) rot=(0,0,-1;0.785398rad)
  Width = 6
FEATURE [Part::Cylinder] Cylinder1480  label="Válec1480"
  Angle = 360
  AttacherType = Attacher::AttachEngine3D
  Height = 60
  Placement = pos=(1.2e-14,-41,-54) rot=(0,0,-1;1.5708rad)
  Radius = 1.5
FEATURE [Part::Box] Box628  label="Krychle628"
  AttacherType = Attacher::AttachEngine3D
  Height = 2
  Length = 8
  Placement = pos=(-24.0416,28.2843,-4) rot=(0,0,1;2.35619rad)
  Width = 6
FEATURE [Part::Compound] Compound993
  Links = -> [Box624,Box622,Box628,Box623,Box625,Box626,Box627,Box621]
  Placement = pos=(0,0,0) rot=(0,0,1;0.392699rad)
FEATURE [Part::Cylinder] Cylinder1481  label="Válec1481"
  Angle = 360
  AttacherType = Attacher::AttachEngine3D
  Height = 60
  Placement = pos=(-28.9914,28.9914,-54) rot=(0,0,1;2.35619rad)
  Radius = 1.5
FEATURE [Part::Cylinder] Cylinder1482  label="Válec1482"
  Angle = 360
  AttacherType = Attacher::AttachEngine3D
  Height = 60
  Placement = pos=(-4e-15,41,-54) rot=(0,0,1;1.5708rad)
  Radius = 1.5
FEATURE [Part::Compound] Compound991
  Links = -> [Cylinder1479,Cylinder1482,Cylinder1481,Cylinder1476,Cylinder1477,Cylinder1480,Cylinder1478,Cylinder1475]
  Placement = pos=(0,0,0) rot=(0,0,1;0.392699rad)
FEATURE [Part::Box] Box629  label="Krychle629"
  AttacherType = Attacher::AttachEngine3D
  Height = 6
  Length = 2
  Placement = pos=(36,20,-8) rot=(0,0,1;0rad)
  Width = 6
FEATURE [Part::Cylinder] Cylinder1483  label="Válec1483"
  Angle = 360
  AttacherType = Attacher::AttachEngine3D
  Height = 60
  Placement = pos=(28,-51,7) rot=(0,1,0;1.5708rad)
  Radius = 1.5
FEATURE [Part::Cylinder] Cylinder1484  label="Válec1484"
  Angle = 360
  AttacherType = Attacher::AttachEngine3D
  Height = 60
  Placement = pos=(32,-23,-5) rot=(0,1,0;1.5708rad)
  Radius = 1.5
FEATURE [Part::Cylinder] Cylinder1485  label="Válec1485"
  Angle = 360
  AttacherType = Attacher::AttachEngine3D
  Height = 60
  Placement = pos=(32,23,-5) rot=(0,1,0;1.5708rad)
  Radius = 1.5
FEATURE [Part::Box] Box630  label="Krychle630"
  AttacherType = Attacher::AttachEngine3D
  Height = 6
  Length = 2
  Placement = pos=(32,-54,4) rot=(0,0,1;0rad)
  Width = 6
FEATURE [Part::Box] Box631  label="Krychle631"
  AttacherType = Attacher::AttachEngine3D
  Height = 6
  Length = 2
  Placement = pos=(32,48,4) rot=(0,0,1;0rad)
  Width = 6
FEATURE [Part::Box] Box632  label="Krychle632"
  AttacherType = Attacher::AttachEngine3D
  Height = 6
  Length = 2
  Placement = pos=(36,-26,-8) rot=(0,0,1;0rad)
  Width = 6
FEATURE [Part::Compound] Compound994
  Links = -> [Box629,Box632,Box631,Box630]
FEATURE [Part::Cylinder] Cylinder1486  label="Válec1486"
  Angle = 360
  AttacherType = Attacher::AttachEngine3D
  Height = 60
  Placement = pos=(28,51,7) rot=(0,1,0;1.5708rad)
  Radius = 1.5
FEATURE [Part::Compound] Compound992
  Links = -> [Cylinder1485,Cylinder1484,Cylinder1486,Cylinder1483]
FEATURE [Part::Cylinder] Cylinder1487  label="Válec1487"
  Angle = 360
  AttacherType = Attacher::AttachEngine3D
  Height = 60
  Placement = pos=(41,0,-54) rot=(0,0,1;0rad)
  Radius = 1.5
FEATURE [Part::Cylinder] Cylinder1488  label="Válec1488"
  Angle = 360
  AttacherType = Attacher::AttachEngine3D
  Height = 60
  Placement = pos=(-41,-1.1e-14,-54) rot=(0,0,1;3.14159rad)
  Radius = 1.5
FEATURE [Part::Cylinder] Cylinder1489  label="Válec1489"
  Angle = 360
  AttacherType = Attacher::AttachEngine3D
  Height = 60
  Placement = pos=(-28.9914,-28.9914,-54) rot=(0,0,1;3.92699rad)
  Radius = 1.5
FEATURE [Part::Cylinder] Cylinder1490  label="Válec1490"
  Angle = 360
  AttacherType = Attacher::AttachEngine3D
  Height = 60
  Placement = pos=(28.9914,-28.9914,-54) rot=(0,0,-1;0.785398rad)
  Radius = 1.5
FEATURE [Part::Cylinder] Cylinder1491  label="Válec1491"
  Angle = 360
  AttacherType = Attacher::AttachEngine3D
  Height = 60
  Placement = pos=(28.9914,28.9914,-54) rot=(0,0,1;0.785398rad)
  Radius = 1.5
FEATURE [Part::Cylinder] Cylinder1492  label="Válec1492"
  Angle = 360
  AttacherType = Attacher::AttachEngine3D
  Height = 60
  Placement = pos=(-28.9914,28.9914,-54) rot=(0,0,1;2.35619rad)
  Radius = 1.5
FEATURE [Part::Cylinder] Cylinder1493  label="Válec1493"
  Angle = 360
  AttacherType = Attacher::AttachEngine3D
  Height = 60
  Placement = pos=(1.2e-14,-41,-54) rot=(0,0,-1;1.5708rad)
  Radius = 1.5
FEATURE [Part::Cylinder] Cylinder1494  label="Válec1494"
  Angle = 360
  AttacherType = Attacher::AttachEngine3D
  Height = 60
  Placement = pos=(-4e-15,41,-54) rot=(0,0,1;1.5708rad)
  Radius = 1.5
FEATURE [Part::Compound] Compound995
  Links = -> [Cylinder1491,Cylinder1494,Cylinder1492,Cylinder1488,Cylinder1489,Cylinder1493,Cylinder1490,Cylinder1487]
  Placement = pos=(0,0,0) rot=(0,0,1;0.392699rad)
FEATURE [Part::Cut] Cut536
  Base = -> Cut521
  Tool = -> Compound995
FEATURE [Part::FeaturePython] Tube135  # WARN: FeaturePython — macro-defined, semantics opaque (R4)
  AttacherType = Attacher::AttachEngine3D
  Height = 8
  InnerRadius = 38
  OuterRadius = 46
  Placement = pos=(0,0,-8) rot=(0,0,1;0rad)
FEATURE [Part::Cut] Cut532
  Base = -> Tube135
  Tool = -> Compound991
FEATURE [Part::Cut] Cut533
  Base = -> Cut532
  Tool = -> Compound993
FEATURE [Part::Cut] Cut534
  Base = -> Cut533
  Tool = -> Compound994
FEATURE [Part::Cut] Cut535
  Base = -> Cut534
  Placement = pos=(0,0,2) rot=(0,0,1;0rad)
  Tool = -> Compound992
FEATURE [Part::FeaturePython] Tube136  label="ZKL-61816-010"  # WARN: FeaturePython — macro-defined, semantics opaque (R4)
  AttacherType = Attacher::AttachEngine3D
  Height = 11
  InnerRadius = 40
  OuterRadius = 50
  Placement = pos=(0,0,25.4) rot=(0,0,1;0rad)
FEATURE [Part::FeaturePython] Tube137  label="ZKL-61816-011"  # WARN: FeaturePython — macro-defined, semantics opaque (R4)
  AttacherType = Attacher::AttachEngine3D
  Height = 11
  InnerRadius = 40
  OuterRadius = 50
  Placement = pos=(0,0,25) rot=(0,0,1;0rad)
FEATURE [Part::FeaturePython] wormgear082  # WARN: FeaturePython — macro-defined, semantics opaque (R4)
  AttacherType = Attacher::AttachEngine3D
  Placement = pos=(0,0,0) rot=(0,0,-1;0.1309rad)
  beta = 38.9725
  clearance = 0.25
  diameter = 66.75
  head = 0.5
  height = 14
  module = 1.5
  pressure_angle = 20
  reverse_pitch = false
  teeth = 36
  version = 0.0.3
FEATURE [Part::FeaturePython] Tube138  # WARN: FeaturePython — macro-defined, semantics opaque (R4)
  AttacherType = Attacher::AttachEngine3D
  Height = 16
  InnerRadius = 40
  OuterRadius = 46
  Placement = pos=(0,0,26) rot=(0,0,1;0rad)
FEATURE [Part::Cut] Cut538
  Base = -> Tube138
  Tool = -> Tube136
FEATURE [Part::FeaturePython] wormgear083  # WARN: FeaturePython — macro-defined, semantics opaque (R4)
  AttacherType = Attacher::AttachEngine3D
  Placement = pos=(0,0,0) rot=(0,0,1;0.10472rad)
  beta = 38.9725
  clearance = 0.25
  diameter = 66.75
  head = 0.5
  height = 14
  module = 1.5
  pressure_angle = 20
  reverse_pitch = true
  teeth = 36
  version = 0.0.3
FEATURE [Part::FeaturePython] Tube139  label="ZKL-61816-subwasher003"  # WARN: FeaturePython — macro-defined, semantics opaque (R4)
  AttacherType = Attacher::AttachEngine3D
  Height = 0.4
  InnerRadius = 40
  OuterRadius = 42
  Placement = pos=(0,0,38) rot=(0,0,1;0rad)
FEATURE [Part::Box] Box633  label="Krychle633"
  AttacherType = Attacher::AttachEngine3D
  Height = 2
  Length = 6
  Placement = pos=(-34.6482,-30.4056,33) rot=(0,0,-1;0.785398rad)
  Width = 8
FEATURE [Part::Cylinder] Cylinder1495  label="Válec1495"
  Angle = 360
  AttacherType = Attacher::AttachEngine3D
  Height = 32
  Placement = pos=(-29.6985,29.6985,33.5) rot=(0,0,1;3.92699rad)
  Radius = 1.5
FEATURE [Part::Cylinder] Cylinder1496  label="Válec1496"
  Angle = 360
  AttacherType = Attacher::AttachEngine3D
  Height = 32
  Placement = pos=(29.6985,29.6985,33.5) rot=(0,0,1;2.35619rad)
  Radius = 1.5
FEATURE [Part::Cylinder] Cylinder1497  label="Válec1497"
  Angle = 360
  AttacherType = Attacher::AttachEngine3D
  Height = 32
  Placement = pos=(-29.6985,-29.6985,33.5) rot=(0,0,-1;0.785398rad)
  Radius = 1.5
FEATURE [Part::Box] Box634  label="Krychle634"
  AttacherType = Attacher::AttachEngine3D
  Height = 2
  Length = 6
  Placement = pos=(30.4056,-34.6482,33) rot=(0,0,1;0.785398rad)
  Width = 8
FEATURE [Part::Box] Box635  label="Krychle635"
  AttacherType = Attacher::AttachEngine3D
  Height = 2
  Length = 6
  Placement = pos=(34.6482,30.4056,33) rot=(0,0,1;2.35619rad)
  Width = 8
FEATURE [Part::Cylinder] Cylinder1498  label="Válec1498"
  Angle = 360
  AttacherType = Attacher::AttachEngine3D
  Height = 32
  Placement = pos=(0,-42,33.5) rot=(0,0,1;0rad)
  Radius = 1.5
FEATURE [Part::Box] Box636  label="Krychle636"
  AttacherType = Attacher::AttachEngine3D
  Height = 2
  Length = 6
  Placement = pos=(46,-3,33) rot=(0,0,1;1.5708rad)
  Width = 8
FEATURE [Part::Box] Box637  label="Krychle637"
  AttacherType = Attacher::AttachEngine3D
  Height = 2
  Length = 6
  Placement = pos=(-30.4056,34.6482,33) rot=(0,0,1;3.92699rad)
  Width = 8
FEATURE [Part::Cylinder] Cylinder1499  label="Válec1499"
  Angle = 360
  AttacherType = Attacher::AttachEngine3D
  Height = 32
  Placement = pos=(-42,-2.4e-14,33.5) rot=(0,0,-1;1.5708rad)
  Radius = 1.5
FEATURE [Part::Box] Box638  label="Krychle638"
  AttacherType = Attacher::AttachEngine3D
  Height = 2
  Length = 6
  Placement = pos=(-46,3,33) rot=(0,0,-1;1.5708rad)
  Width = 8
FEATURE [Part::Box] Box639  label="Krychle639"
  AttacherType = Attacher::AttachEngine3D
  Height = 2
  Length = 6
  Placement = pos=(3,46,33) rot=(0,0,1;3.14159rad)
  Width = 8
FEATURE [Part::Box] Box640  label="Krychle640"
  AttacherType = Attacher::AttachEngine3D
  Height = 2
  Length = 6
  Placement = pos=(-3,-46,33) rot=(0,0,1;0rad)
  Width = 8
FEATURE [Part::Box] Box641  label="Krychle641"
  AttacherType = Attacher::AttachEngine3D
  Height = 2
  Length = 6
  Placement = pos=(-34.6482,-30.4056,33) rot=(0,0,-1;0.785398rad)
  Width = 8
FEATURE [Part::Box] Box642  label="Krychle642"
  AttacherType = Attacher::AttachEngine3D
  Height = 2
  Length = 6
  Placement = pos=(30.4056,-34.6482,33) rot=(0,0,1;0.785398rad)
  Width = 8
FEATURE [Part::Cylinder] Cylinder1500  label="Válec1500"
  Angle = 360
  AttacherType = Attacher::AttachEngine3D
  Height = 32
  Placement = pos=(-1.4e-14,42,33.5) rot=(0,0,1;3.14159rad)
  Radius = 1.5
FEATURE [Part::Box] Box643  label="Krychle643"
  AttacherType = Attacher::AttachEngine3D
  Height = 2
  Length = 6
  Placement = pos=(34.6482,30.4056,33) rot=(0,0,1;2.35619rad)
  Width = 8
FEATURE [Part::Cylinder] Cylinder1501  label="Válec1501"
  Angle = 360
  AttacherType = Attacher::AttachEngine3D
  Height = 32
  Placement = pos=(29.6985,-29.6985,33.5) rot=(0,0,1;0.785398rad)
  Radius = 1.5
FEATURE [Part::Cylinder] Cylinder1502  label="Válec1502"
  Angle = 360
  AttacherType = Attacher::AttachEngine3D
  Height = 32
  Placement = pos=(42,6e-15,33.5) rot=(0,0,1;1.5708rad)
  Radius = 1.5
FEATURE [Part::Compound] Compound999
  Links = -> [Cylinder1498,Cylinder1501,Cylinder1502,Cylinder1496,Cylinder1500,Cylinder1495,Cylinder1499,Cylinder1497]
  Placement = pos=(0,0,0) rot=(0,0,1;0.392699rad)
FEATURE [Part::Cut] Cut543
  Base = -> Cut538
  Tool = -> Compound999
FEATURE [Part::Box] Box644  label="Krychle644"
  AttacherType = Attacher::AttachEngine3D
  Height = 2
  Length = 6
  Placement = pos=(3,46,33) rot=(0,0,1;3.14159rad)
  Width = 8
FEATURE [Part::Compound] Compound1001
  Links = -> [Box633,Box642,Box636,Box640,Box643,Box644,Box637,Box638]
  Placement = pos=(0,0,4.4) rot=(0,0,1;0.392699rad)
FEATURE [Part::Cut] Cut544
  Base = -> Cut543
  Placement = pos=(0,0,3) rot=(0,0,1;0rad)
  Tool = -> Compound1001
FEATURE [Part::Cylinder] Cylinder1503  label="Válec1503"
  Angle = 360
  AttacherType = Attacher::AttachEngine3D
  Height = 8
  Radius = 40
FEATURE [Part::Cut] Cut540
  Base = -> Cylinder1503
  Placement = pos=(0,0,25) rot=(0,0,1;0.294961rad)
  Tool = -> wormgear082
FEATURE [Part::Box] Box645  label="Krychle645"
  AttacherType = Attacher::AttachEngine3D
  Height = 2
  Length = 6
  Placement = pos=(-46,3,33) rot=(0,0,-1;1.5708rad)
  Width = 8
FEATURE [Part::Cylinder] Cylinder1504  label="Válec1504"
  Angle = 360
  AttacherType = Attacher::AttachEngine3D
  Height = 32
  Placement = pos=(0,-42,33.5) rot=(0,0,1;0rad)
  Radius = 1.5
FEATURE [Part::Cylinder] Cylinder1505  label="Válec1505"
  Angle = 360
  AttacherType = Attacher::AttachEngine3D
  Height = 32
  Placement = pos=(-29.6985,-29.6985,33.5) rot=(0,0,-1;0.785398rad)
  Radius = 1.5
FEATURE [Part::Box] Box646  label="Krychle646"
  AttacherType = Attacher::AttachEngine3D
  Height = 2
  Length = 6
  Placement = pos=(46,-3,33) rot=(0,0,1;1.5708rad)
  Width = 8
FEATURE [Part::Cylinder] Cylinder1506  label="Válec1506"
  Angle = 360
  AttacherType = Attacher::AttachEngine3D
  Height = 32
  Placement = pos=(29.6985,-29.6985,33.5) rot=(0,0,1;0.785398rad)
  Radius = 1.5
FEATURE [Part::Cylinder] Cylinder1507  label="Válec1507"
  Angle = 360
  AttacherType = Attacher::AttachEngine3D
  Height = 8
  Radius = 40
FEATURE [Part::Cut] Cut542
  Base = -> Cylinder1507
  Placement = pos=(0,0,33) rot=(0,0,1;0.53058rad)
  Tool = -> wormgear083
FEATURE [Part::Cylinder] Cylinder1508  label="Válec1508"
  Angle = 360
  AttacherType = Attacher::AttachEngine3D
  Height = 32
  Placement = pos=(-29.6985,29.6985,33.5) rot=(0,0,1;3.92699rad)
  Radius = 1.5
FEATURE [Part::Cylinder] Cylinder1509  label="Válec1509"
  Angle = 360
  AttacherType = Attacher::AttachEngine3D
  Height = 32
  Placement = pos=(42,6e-15,33.5) rot=(0,0,1;1.5708rad)
  Radius = 1.5
FEATURE [Part::Box] Box647  label="Krychle647"
  AttacherType = Attacher::AttachEngine3D
  Height = 2
  Length = 6
  Placement = pos=(-3,-46,33) rot=(0,0,1;0rad)
  Width = 8
FEATURE [Part::Cylinder] Cylinder1510  label="Válec1510"
  Angle = 360
  AttacherType = Attacher::AttachEngine3D
  Height = 32
  Placement = pos=(29.6985,29.6985,33.5) rot=(0,0,1;2.35619rad)
  Radius = 1.5
FEATURE [Part::Box] Box648  label="Krychle648"
  AttacherType = Attacher::AttachEngine3D
  Height = 2
  Length = 6
  Placement = pos=(-30.4056,34.6482,33) rot=(0,0,1;3.92699rad)
  Width = 8
FEATURE [Part::Compound] Compound998
  Links = -> [Box641,Box634,Box646,Box647,Box635,Box639,Box648,Box645]
  Placement = pos=(0,0,3.4) rot=(0,0,1;0.392699rad)
FEATURE [Part::Cut] Cut539
  Base = -> Cut542
  Tool = -> Compound998
FEATURE [Part::Compound] Compound1002
  Links = -> [Cut539,Cut540]
  Placement = pos=(0,0,4) rot=(0,0,1;0rad)
FEATURE [Part::Cut] Cut541
  Base = -> Compound1002
  Tool = -> Tube137
FEATURE [Part::Cylinder] Cylinder1511  label="Válec1511"
  Angle = 360
  AttacherType = Attacher::AttachEngine3D
  Height = 32
  Placement = pos=(-1.4e-14,42,33.5) rot=(0,0,1;3.14159rad)
  Radius = 1.5
FEATURE [Part::Cylinder] Cylinder1512  label="Válec1512"
  Angle = 360
  AttacherType = Attacher::AttachEngine3D
  Height = 32
  Placement = pos=(-42,-2.4e-14,33.5) rot=(0,0,-1;1.5708rad)
  Radius = 1.5
FEATURE [Part::Compound] Compound1000
  Links = -> [Cylinder1504,Cylinder1506,Cylinder1509,Cylinder1510,Cylinder1511,Cylinder1508,Cylinder1512,Cylinder1505]
  Placement = pos=(0,0,0) rot=(0,0,1;0.392699rad)
FEATURE [Part::Cut] Cut537
  Base = -> Tube139
  Placement = pos=(0,0,1) rot=(0,0,1;0rad)
  Tool = -> Compound1000
FEATURE [Part::Compound] Compound997  label="J-midi-thin_actuator_v1.7"
  Links = -> [Cut537,Cut544,Cut541]
FEATURE [Part::Box] Box649  label="Krychle649"
  AttacherType = Attacher::AttachEngine3D
  Height = 2
  Length = 8
  Placement = pos=(-24.0416,28.2843,-4) rot=(0,0,1;2.35619rad)
  Width = 6
FEATURE [Part::Box] Box650  label="Krychle650"
  AttacherType = Attacher::AttachEngine3D
  Height = 2
  Length = 8
  Placement = pos=(3,37,-4) rot=(0,0,1;1.5708rad)
  Width = 6
FEATURE [Part::Box] Box651  label="Krychle651"
  AttacherType = Attacher::AttachEngine3D
  Height = 2
  Length = 8
  Placement = pos=(-37,3,-4) rot=(0,0,1;3.14159rad)
  Width = 6
FEATURE [Part::Box] Box652  label="Krychle652"
  AttacherType = Attacher::AttachEngine3D
  Height = 2
  Length = 8
  Placement = pos=(28.2843,24.0416,-4) rot=(0,0,1;0.785398rad)
  Width = 6
FEATURE [Part::Box] Box653  label="Krychle653"
  AttacherType = Attacher::AttachEngine3D
  Height = 2
  Length = 8
  Placement = pos=(-28.2843,-24.0416,-4) rot=(0,0,1;3.92699rad)
  Width = 6
FEATURE [Part::Box] Box654  label="Krychle654"
  AttacherType = Attacher::AttachEngine3D
  Height = 2
  Length = 8
  Placement = pos=(37,-3,-4) rot=(0,0,1;0rad)
  Width = 6
FEATURE [Part::Box] Box655  label="Krychle655"
  AttacherType = Attacher::AttachEngine3D
  Height = 2
  Length = 8
  Placement = pos=(-3,-37,-4) rot=(0,0,-1;1.5708rad)
  Width = 6
FEATURE [Part::Box] Box656  label="Krychle656"
  AttacherType = Attacher::AttachEngine3D
  Height = 2
  Length = 8
  Placement = pos=(24.0416,-28.2843,-4) rot=(0,0,-1;0.785398rad)
  Width = 6
FEATURE [Part::Compound] Compound1003
  Links = -> [Box652,Box650,Box649,Box651,Box653,Box655,Box656,Box654]
  Placement = pos=(0,0,0) rot=(0,0,1;0.392699rad)
FEATURE [Part::Compound] Compound1004  label="J-midi-thin_monoblok_v1.1"
  Links = -> [Cut520,Fillet023,Cut535,Cut536]
FEATURE [Mesh::Feature] Mesh  label="J-midi-thin_monoblok_v1.1 (Meshed)"
